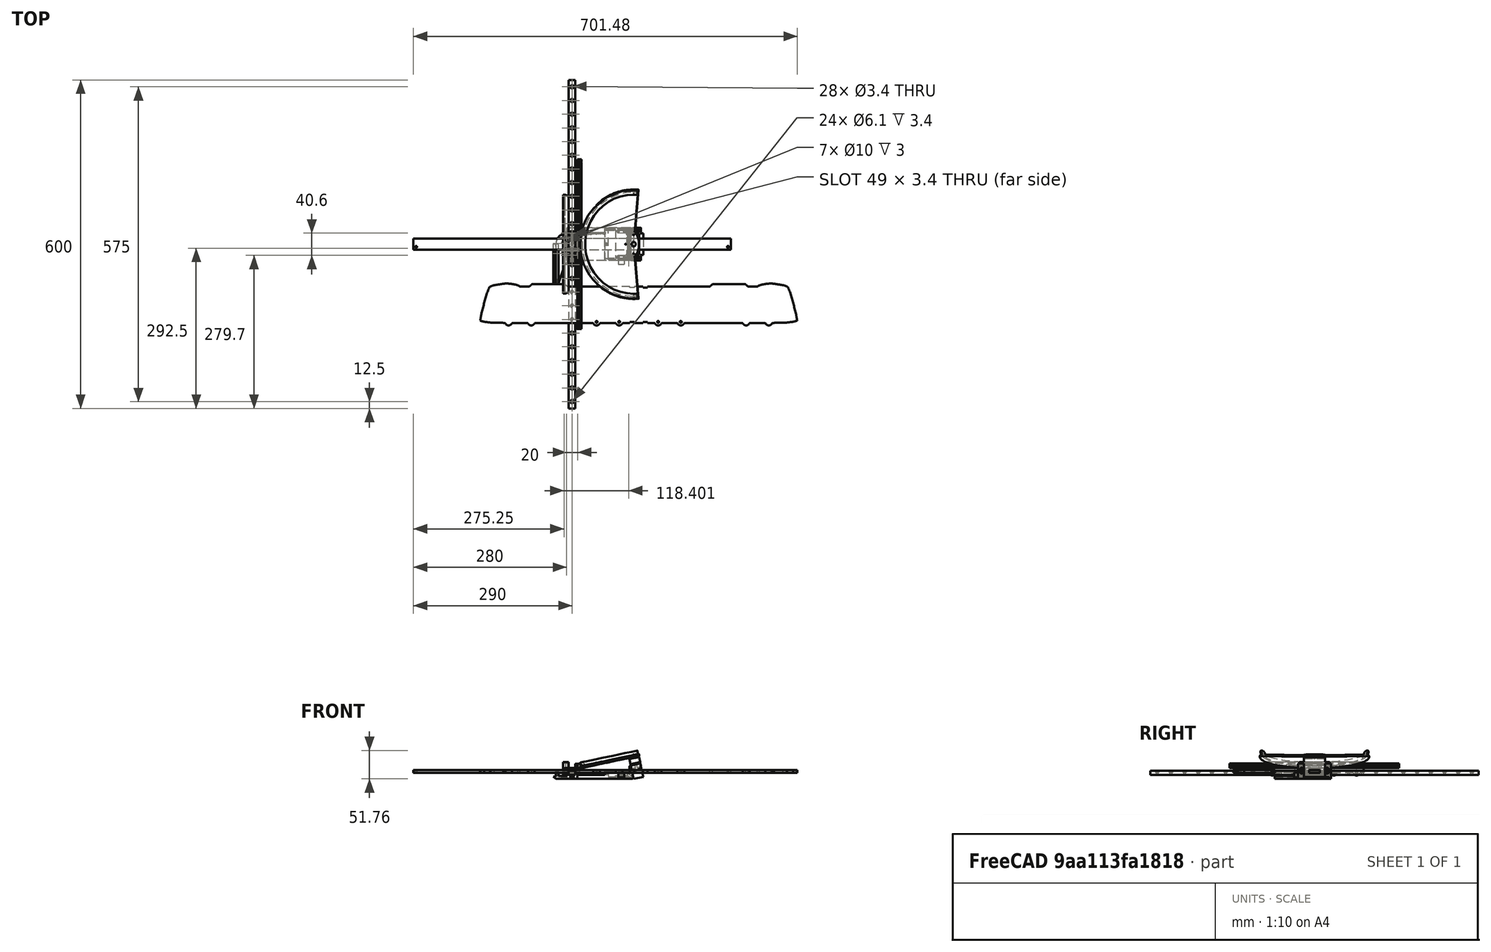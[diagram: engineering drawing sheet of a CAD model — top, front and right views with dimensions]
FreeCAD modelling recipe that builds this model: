
FCSTD DOCUMENT  (FreeCAD 1.0R39319 (Git))
Label: mechanism
License: All rights reserved
LicenseURL: https://en.wikipedia.org/wiki/All_rights_reserved
objects: Sketcher::SketchObject×61, PartDesign::Pad×27, PartDesign::SubShapeBinder×24, PartDesign::Pocket×22, App::Link×15, App::FeaturePython×15, PartDesign::Body×13, PartDesign::Hole×12, PartDesign::Mirrored×3, PartDesign::Fillet×3, PartDesign::LinearPattern×1, PartDesign::Revolution×1, PartDesign::SubtractivePipe×1, PartDesign::FeatureBase×1, Part::FeaturePython×1, Assembly::JointGroup×1, Assembly::AssemblyObject×1
note: 368 computed .brp shape members not serialized (recipe doc carries the construction recipe); baked Part::Feature solids carry a one-line shape summary decoded from their .brp

FEATURE [Sketcher::SketchObject] Sketch  label="Rail Cross-Section"
  ArcFitTolerance = 1e-06
  AttachmentSupport = -> [XZ_Plane]
  FullyConstrained = true
  MakeInternals = false
  MapMode = 5
  Placement = pos=(0,0,0) rot=(1,0,0;1.5708rad)
  sketch-geometry (11):
    g0: LineSegment StartX=-6 StartY=4 StartZ=0 EndX=-6 EndY=-3.35 EndZ=0
    g1: LineSegment StartX=-5.35 StartY=-4 StartZ=0 EndX=5.35 EndY=-4 EndZ=0
    g2: LineSegment StartX=6 StartY=-3.35 StartZ=0 EndX=6 EndY=4 EndZ=0
    g3: LineSegment StartX=6 StartY=4 StartZ=0 EndX=-6 EndY=4 EndZ=0
    g4: GeomPoint [constr] X=0 Y=0 Z=0
    g5: GeomPoint [constr] X=-6 Y=4 Z=0
    g6: GeomPoint [constr] X=6 Y=4 Z=0
    g7: ArcOfCircle CenterX=5.35 CenterY=-3.35 CenterZ=0 NormalX=0 NormalY=0 NormalZ=1 AngleXU=0 Radius=0.65 StartAngle=4.71239 EndAngle=6.28319
    g8: GeomPoint [constr] X=6 Y=-4 Z=0
    g9: ArcOfCircle CenterX=-5.35 CenterY=-3.35 CenterZ=0 NormalX=0 NormalY=0 NormalZ=1 AngleXU=0 Radius=0.65 StartAngle=3.14159 EndAngle=4.71239
    g10: GeomPoint [constr] X=-6 Y=-4 Z=0
  constraints (22):
    c: Vertical(g0)
    c: Vertical(g2)
    c: Horizontal(g1)
    c: Horizontal(g3)
    c: Symmetric(g8,g5,g4)
    c: Coincident(g4,g-1)
    c: DistanceX(g5,g6) = 12  'Wr'
    c: DistanceY(g8,g6) = 8  'Hr'
    c: PointOnObject(g8,g2)
    c: PointOnObject(g8,g1)
    c: Tangent(g2,g7) = -1.5708
    c: Tangent(g1,g7) = -1.5708
    c: PointOnObject(g10,g1)
    c: PointOnObject(g10,g0)
    c: Tangent(g1,g9) = -1.5708
    c: Tangent(g0,g9) = -1.5708
    c: Equal(g9,g7)
    c: Coincident(g2,g6)
    c: Coincident(g3,g2)
    c: Coincident(g0,g5)
    c: Coincident(g3,g0)
    c: Radius(g9) = 0.65  'radius'
FEATURE [PartDesign::Pad] Pad  label="Rail Extrusion"
  Direction = (0,-1,2e-16)
  Length = 600
  Length2 = 10
  Midplane = true
  Placement = pos=(0,0,0) rot=(1,0,0;1.5708rad)
  Profile = -> Sketch
  ReferenceAxis = -> Sketch [N_Axis]
  Refine = true
  Suppressed = false
  Type = 0
FEATURE [PartDesign::SubShapeBinder] Binder  label="SubShapeBinder"
  BindCopyOnChange = 0
  BindMode = 0
  ClaimChildren = false
  Context = -> Body001 [Binder.]
  Fuse = false
  MakeFace = true
  OffsetFill = false
  OffsetIntersection = false
  OffsetJoinType = 0
  OffsetOpenResult = false
  PartialLoad = false
  Refine = true
  Relative = true
  Support = -> [Body[Sketch.]]
  _Version = 2
FEATURE [Sketcher::SketchObject] Sketch001  label="Block Cross-Section"
  ArcFitTolerance = 1e-06
  AttachmentSupport = -> [Binder]
  ExternalGeometry = -> [Binder]
  FullyConstrained = true
  MakeInternals = false
  MapMode = 5
  Placement = pos=(0,0,0) rot=(0,0.707107,0.707107;3.14159rad)
  sketch-geometry (17):
    g0: LineSegment StartX=-13.5 StartY=8.5 StartZ=0 EndX=-13.5 EndY=-0.5 EndZ=0
    g1: LineSegment StartX=-13 StartY=-1 StartZ=0 EndX=-6 EndY=-1 EndZ=0
    g2: LineSegment StartX=13.5 StartY=-0.5 StartZ=0 EndX=13.5 EndY=8.5 EndZ=0
    g3: LineSegment StartX=13 StartY=9 StartZ=0 EndX=-13 EndY=9 EndZ=0
    g4: GeomPoint [constr] X=0 Y=4 Z=0
    g5: LineSegment StartX=-6 StartY=-1 StartZ=0 EndX=-6 EndY=4 EndZ=0
    g6: LineSegment StartX=-6 StartY=4 StartZ=0 EndX=6 EndY=4 EndZ=0
    g7: LineSegment StartX=6 StartY=4 StartZ=0 EndX=6 EndY=-1 EndZ=0
    g8: LineSegment StartX=6 StartY=-1 StartZ=0 EndX=13 EndY=-1 EndZ=0
    g9: ArcOfCircle CenterX=-13 CenterY=8.5 CenterZ=0 NormalX=0 NormalY=0 NormalZ=1 AngleXU=0 Radius=0.5 StartAngle=1.5708 EndAngle=3.14159
    g10: GeomPoint [constr] X=-13.5 Y=9 Z=0
    g11: ArcOfCircle CenterX=13 CenterY=8.5 CenterZ=0 NormalX=0 NormalY=0 NormalZ=1 AngleXU=0 Radius=0.5 StartAngle=-1.8e-15 EndAngle=1.5708
    g12: GeomPoint [constr] X=13.5 Y=9 Z=0
    g13: ArcOfCircle CenterX=13 CenterY=-0.5 CenterZ=0 NormalX=0 NormalY=0 NormalZ=1 AngleXU=0 Radius=0.5 StartAngle=4.71239 EndAngle=6.28319
    g14: GeomPoint [constr] X=13.5 Y=-1 Z=0
    g15: ArcOfCircle CenterX=-13 CenterY=-0.5 CenterZ=0 NormalX=0 NormalY=0 NormalZ=1 AngleXU=0 Radius=0.5 StartAngle=3.14159 EndAngle=4.71239
    g16: GeomPoint [constr] X=-13.5 Y=-1 Z=0
  constraints (41):
    c: Vertical(g0)
    c: Vertical(g2)
    c: Horizontal(g1)
    c: Horizontal(g3)
    c: Symmetric(g14,g10,g4)
    c: PointOnObject(g4,g-2)
    c: Vertical(g5)
    c: Coincident(g5,g6)
    c: Coincident(g6,g7)
    c: PointOnObject(g7,g8)
    c: Vertical(g7)
    c: Coincident(g1,g5)
    c: PointOnObject(g8,g7)
    c: Symmetric(g6,g5,g-2)
    c: PointOnObject(g1,g-3)
    c: PointOnObject(g5,g-4)
    c: DistanceY(g-5,g10) = 13  'Height'
    c: DistanceY(g-5,g16) = 3  'H1'
    c: Horizontal(g7,g1)
    c: Horizontal(g8)
    c: DistanceX(g10,g12) = 27  'W'
    c: PointOnObject(g10,g0)
    c: PointOnObject(g10,g3)
    c: Tangent(g0,g9) = -1.5708
    c: Tangent(g3,g9) = -1.5708
    c: PointOnObject(g12,g3)
    c: PointOnObject(g12,g2)
    c: Tangent(g3,g11) = -1.5708
    c: Tangent(g2,g11) = -1.5708
    c: PointOnObject(g14,g8)
    c: PointOnObject(g14,g2)
    c: Tangent(g8,g13) = -1.5708
    c: Tangent(g2,g13) = -1.5708
    c: PointOnObject(g16,g1)
    c: PointOnObject(g16,g0)
    c: Tangent(g1,g15) = -1.5708
    c: Tangent(g0,g15) = -1.5708
    c: Equal(g9,g15)
    c: Equal(g15,g11)
    c: Equal(g11,g13)
    c: Radius(g9) = 0.5
FEATURE [PartDesign::Pad] Pad001
  Direction = (0,1,-2e-16)
  Length = 32.4
  Length2 = 10
  Midplane = true
  Profile = -> Sketch001
  ReferenceAxis = -> Sketch001 [N_Axis]
  Refine = true
  Suppressed = false
  Type = 0
FEATURE [Sketcher::SketchObject] Sketch002
  ArcFitTolerance = 1e-06
  AttachmentSupport = -> [XZ_Plane001]
  ExternalGeometry = -> [Sketch001]
  FullyConstrained = true
  MakeInternals = false
  MapMode = 5
  Placement = pos=(0,0,0) rot=(1,0,0;1.5708rad)
  sketch-geometry (8):
    g0: LineSegment StartX=-13 StartY=8.5 StartZ=0 EndX=-13 EndY=-0.5 EndZ=0
    g1: LineSegment StartX=-13 StartY=-0.5 StartZ=0 EndX=-6 EndY=-0.5 EndZ=0
    g2: LineSegment StartX=-6 StartY=-0.5 StartZ=0 EndX=-6 EndY=4 EndZ=0
    g3: LineSegment StartX=-6 StartY=4 StartZ=0 EndX=6 EndY=4 EndZ=0
    g4: LineSegment StartX=6 StartY=4 StartZ=0 EndX=6 EndY=-0.5 EndZ=0
    g5: LineSegment StartX=6 StartY=-0.5 StartZ=0 EndX=13 EndY=-0.5 EndZ=0
    g6: LineSegment StartX=13 StartY=-0.5 StartZ=0 EndX=13 EndY=8.5 EndZ=0
    g7: LineSegment StartX=13 StartY=8.5 StartZ=0 EndX=-13 EndY=8.5 EndZ=0
  constraints (22):
    c: Vertical(g0)
    c: Coincident(g0,g1)
    c: PointOnObject(g1,g-7)
    c: Horizontal(g1)
    c: Coincident(g1,g2)
    c: Coincident(g2,g-7)
    c: Coincident(g2,g3)
    c: Coincident(g3,g-6)
    c: Coincident(g3,g4)
    c: Coincident(g4,g5)
    c: Horizontal(g5)
    c: Coincident(g5,g6)
    c: Vertical(g6)
    c: Coincident(g6,g7)
    c: Coincident(g7,g0)
    c: Horizontal(g7)
    c: Vertical(g-3,g0)
    c: Horizontal(g0,g-4)
    c: Horizontal(g-4,g0)
    c: Vertical(g4)
    c: Horizontal(g5,g-5)
    c: Vertical(g-3,g6)
FEATURE [PartDesign::Pad] Pad002  label="BlockExtent"
  BaseFeature = -> Pad001
  Direction = (0,-1,2e-16)
  Length = 45.4
  Length2 = 10
  Midplane = true
  Profile = -> Sketch002
  ReferenceAxis = -> Sketch002 [N_Axis]
  Refine = true
  Suppressed = false
  Type = 0
FEATURE [Sketcher::SketchObject] Sketch004
  ArcFitTolerance = 1e-06
  AttachmentSupport = -> [Pad001]
  FullyConstrained = false
  MakeInternals = false
  MapMode = 5
  Placement = pos=(0,2e-15,9) rot=(0,0,1;0rad)
  sketch-geometry (9):
    g0: Circle CenterX=-10 CenterY=10 CenterZ=0 NormalX=0 NormalY=0 NormalZ=1 AngleXU=0 Radius=2.53403
    g1: Circle CenterX=10 CenterY=10 CenterZ=0 NormalX=0 NormalY=0 NormalZ=1 AngleXU=0 Radius=2.44373
    g2: Circle CenterX=-10 CenterY=-10 CenterZ=0 NormalX=0 NormalY=0 NormalZ=1 AngleXU=0 Radius=2.20024
    g3: Circle CenterX=10 CenterY=-10 CenterZ=0 NormalX=0 NormalY=0 NormalZ=1 AngleXU=0 Radius=2.23133
    g4: LineSegment [constr] StartX=-10 StartY=10 StartZ=0 EndX=-10 EndY=-10 EndZ=0
    g5: LineSegment [constr] StartX=-10 StartY=-10 StartZ=0 EndX=10 EndY=-10 EndZ=0
    g6: LineSegment [constr] StartX=10 StartY=-10 StartZ=0 EndX=10 EndY=10 EndZ=0
    g7: LineSegment [constr] StartX=10 StartY=10 StartZ=0 EndX=-10 EndY=10 EndZ=0
    g8: GeomPoint [constr] X=0 Y=0 Z=0
  constraints (16):
    c: Coincident(g4,g5)
    c: Coincident(g5,g6)
    c: Coincident(g6,g7)
    c: Coincident(g7,g4)
    c: Vertical(g4)
    c: Vertical(g6)
    c: Horizontal(g5)
    c: Horizontal(g7)
    c: Symmetric(g6,g4,g8)
    c: Coincident(g8,g-1)
    c: DistanceX(g7,g7) = 20  'B'
    c: DistanceY(g6,g6) = 20  'C'
    c: Coincident(g0,g4)
    c: Coincident(g1,g6)
    c: Coincident(g5,g3)
    c: Coincident(g4,g2)
FEATURE [PartDesign::Hole] Hole
  BaseFeature = -> Pad002
  CustomThreadClearance = 0
  Depth = 3.5
  DepthType = 0
  Diameter = 2.5
  DrillForDepth = false
  DrillPoint = 1
  DrillPointAngle = 118
  HoleCutCountersinkAngle = 90
  HoleCutCustomValues = false
  HoleCutDepth = 0
  HoleCutDiameter = 6.1
  HoleCutType = 0
  ModelThread = false
  Profile = -> Sketch004
  Refine = true
  Suppressed = false
  Tapered = false
  TaperedAngle = 90
  ThreadClass = 0
  ThreadDepth = 3.5
  ThreadDepthType = 0
  ThreadDirection = 0
  ThreadFit = 0
  ThreadSize = 9
  ThreadType = 1
  Threaded = true
  UseCustomThreadClearance = false
FEATURE [PartDesign::Body] Body001  label="Block"
  AllowCompound = false
  Group = -> [Binder,Sketch001,Pad001,Sketch002,Pad002,Sketch004,Hole]
  Origin = -> Origin001
  Tip = -> Hole
FEATURE [Sketcher::SketchObject] Sketch005  label="RailHolePosition"
  ArcFitTolerance = 1e-06
  AttachmentSupport = -> [Pad]
  ExternalGeometry = -> [Pad]
  FullyConstrained = false
  MakeInternals = false
  MapMode = 5
  Placement = pos=(0,1.8e-15,4) rot=(0,0,1;3.14159rad)
  sketch-geometry (1):
    g0: Circle CenterX=0 CenterY=-287.5 CenterZ=0 NormalX=0 NormalY=0 NormalZ=1 AngleXU=0 Radius=2.44176
  constraints (2):
    c: PointOnObject(g0,g-2)
    c: DistanceY(g-3,g0) = 12.5  'E'
FEATURE [PartDesign::Hole] Hole001
  BaseFeature = -> Pad
  CustomThreadClearance = 0
  Depth = 1212.35
  DepthType = 1
  Diameter = 3.4
  DrillForDepth = false
  DrillPoint = 1
  DrillPointAngle = 118
  HoleCutCountersinkAngle = 90
  HoleCutCustomValues = false
  HoleCutDepth = 3.4
  HoleCutDiameter = 6.1
  HoleCutType = 1
  ModelThread = false
  Placement = pos=(0,0,0) rot=(1,0,0;1.5708rad)
  Profile = -> Sketch005
  Refine = true
  Suppressed = false
  Tapered = false
  TaperedAngle = 90
  ThreadClass = 0
  ThreadDepth = 1212.35
  ThreadDepthType = 0
  ThreadDirection = 0
  ThreadFit = 0
  ThreadSize = 9
  ThreadType = 1
  Threaded = false
  UseCustomThreadClearance = false
FEATURE [PartDesign::LinearPattern] LinearPattern
  BaseFeature = -> Hole001
  Direction = -> Y_Axis
  Length = 575
  Mode = 1
  Occurrences = 24
  Offset = 25
  Originals = -> [Hole001]
  Placement = pos=(0,0,0) rot=(1,0,0;1.5708rad)
  Refine = true
  Reversed = true
  Suppressed = false
  TransformMode = 0
  expr: Occurrences = <<Rail Extrusion>>.Length / 25
FEATURE [PartDesign::Body] Body  label="Rail"
  AllowCompound = false
  Group = -> [Sketch,Pad,Sketch005,Hole001,LinearPattern]
  Origin = -> Origin
  Tip = -> LinearPattern
FEATURE [PartDesign::SubShapeBinder] Binder001
  BindCopyOnChange = 0
  BindMode = 0
  ClaimChildren = false
  Context = -> Body002 [Binder001.]
  Fuse = false
  MakeFace = true
  OffsetFill = false
  OffsetIntersection = false
  OffsetJoinType = 0
  OffsetOpenResult = false
  PartialLoad = false
  Refine = true
  Relative = true
  Support = -> [Body[Sketch.]]
  _Version = 2
FEATURE [PartDesign::SubShapeBinder] Binder002
  BindCopyOnChange = 0
  BindMode = 0
  ClaimChildren = false
  Context = -> Body002 [Binder002.]
  Fuse = false
  MakeFace = true
  OffsetFill = false
  OffsetIntersection = false
  OffsetJoinType = 0
  OffsetOpenResult = false
  PartialLoad = false
  Refine = true
  Relative = true
  Support = -> [Body001[Sketch001.]]
  _Version = 2
FEATURE [Sketcher::SketchObject] Sketch006  label="FootProfile"
  ArcFitTolerance = 1e-06
  AttachmentSupport = -> [XZ_Plane002]
  ExternalGeometry = -> [Binder001,Binder002]
  FullyConstrained = true
  MakeInternals = false
  MapMode = 5
  Placement = pos=(0,0,0) rot=(1,0,0;1.5708rad)
  sketch-geometry (12):
    g0: LineSegment StartX=-9.7 StartY=-4 StartZ=0 EndX=-9.7 EndY=-11 EndZ=0
    g1: LineSegment StartX=-6.1 StartY=-4 StartZ=0 EndX=-6.1 EndY=-2.6 EndZ=0
    g2: LineSegment StartX=-6.7 StartY=-2 StartZ=0 EndX=-7.7 EndY=-2 EndZ=0
    g3: LineSegment StartX=-6.1 StartY=-4 StartZ=0 EndX=0 EndY=-4 EndZ=0
    g4: LineSegment StartX=0 StartY=-4 StartZ=0 EndX=0 EndY=-11 EndZ=0
    g5: LineSegment StartX=0 StartY=-11 StartZ=0 EndX=-9.7 EndY=-11 EndZ=0
    g6: ArcOfCircle [constr] CenterX=-6.7 CenterY=-2.6 CenterZ=0 NormalX=0 NormalY=0 NormalZ=1 AngleXU=0 Radius=0.6 StartAngle=1e-16 EndAngle=1.5708
    g7: GeomPoint [constr] X=-6.1 Y=-2 Z=0
    g8: LineSegment StartX=-6.1 StartY=-2.6 StartZ=0 EndX=-6.7 EndY=-2 EndZ=0
    g9: ArcOfCircle [constr] CenterX=-7.7 CenterY=-4 CenterZ=0 NormalX=0 NormalY=0 NormalZ=1 AngleXU=0 Radius=2 StartAngle=1.5708 EndAngle=3.14159
    g10: GeomPoint [constr] X=-9.7 Y=-2 Z=0
    g11: LineSegment StartX=-7.7 StartY=-2 StartZ=0 EndX=-9.7 EndY=-4 EndZ=0
  constraints (30):
    c: Vertical(g0)
    c: Vertical(g1)
    c: Horizontal(g2)
    c: Distance(g-3,g1) = 0.1
    c: Distance(g-4,g2) = 1
    c: Coincident(g3,g1)
    c: PointOnObject(g3,g-2)
    c: Horizontal(g3)
    c: Coincident(g4,g3)
    c: Vertical(g4)
    c: Coincident(g5,g4)
    c: Coincident(g5,g0)
    c: Horizontal(g5)
    c: Distance(g4,g4) = 7  'BaseThickness'
    c: PointOnObject(g1,g-5)
    c: PointOnObject(g7,g2)
    c: PointOnObject(g7,g1)
    c: Tangent(g2,g6) = -1.5708
    c: Tangent(g1,g6) = -1.5708
    c: Coincident(g8,g2)
    c: Coincident(g8,g1)
    c: PointOnObject(g10,g2)
    c: PointOnObject(g10,g0)
    c: Tangent(g2,g9) = -1.5708
    c: Tangent(g0,g9) = -1.5708
    c: Coincident(g11,g2)
    c: Coincident(g11,g0)
    c: Distance(g1,g7) = 0.6
    c: Distance(g2,g2) = 1
    c: Horizontal(g9,g1)
FEATURE [PartDesign::Pad] Pad003
  Direction = (0,-1,2e-16)
  Length = 20
  Length2 = 5
  Midplane = true
  Placement = pos=(0,0,0) rot=(1,0,0;1.5708rad)
  Profile = -> Sketch006
  ReferenceAxis = -> Sketch006 [N_Axis]
  Refine = true
  Suppressed = false
  Type = 4
FEATURE [PartDesign::Mirrored] Mirrored
  BaseFeature = -> Pad003
  MirrorPlane = -> Sketch006 [V_Axis]
  Originals = -> [Pad003]
  Placement = pos=(0,0,0) rot=(1,0,0;1.5708rad)
  Refine = true
  Suppressed = false
  TransformMode = 0
FEATURE [Sketcher::SketchObject] Sketch007
  ArcFitTolerance = 1e-06
  AttachmentSupport = -> [Mirrored]
  FullyConstrained = false
  MakeInternals = false
  MapMode = 5
  Placement = pos=(0,-1.8e-15,-4) rot=(0,0,1;3.14159rad)
  sketch-geometry (1):
    g0: Circle CenterX=0 CenterY=0 CenterZ=0 NormalX=0 NormalY=0 NormalZ=1 AngleXU=0 Radius=1.1986
  constraints (1):
    c: Coincident(g0,g-1)
FEATURE [PartDesign::Hole] Hole002  label="FootHole"
  BaseFeature = -> Mirrored
  CustomThreadClearance = 0
  Depth = 109.851
  DepthType = 1
  Diameter = 4.4
  DrillForDepth = false
  DrillPoint = 1
  DrillPointAngle = 118
  HoleCutCountersinkAngle = 90
  HoleCutCustomValues = false
  HoleCutDepth = 0
  HoleCutDiameter = 6.1
  HoleCutType = 0
  ModelThread = false
  Placement = pos=(0,0,0) rot=(1,0,0;1.5708rad)
  Profile = -> Sketch007
  Refine = true
  Suppressed = false
  Tapered = false
  TaperedAngle = 90
  ThreadClass = 0
  ThreadDepth = 109.851
  ThreadDepthType = 0
  ThreadDirection = 0
  ThreadFit = 0
  ThreadSize = 0
  ThreadType = 0
  Threaded = false
  UseCustomThreadClearance = false
FEATURE [PartDesign::SubShapeBinder] Binder003
  BindCopyOnChange = 0
  BindMode = 0
  ClaimChildren = false
  Context = -> Body003 [Binder003.]
  Fuse = false
  MakeFace = true
  OffsetFill = false
  OffsetIntersection = false
  OffsetJoinType = 0
  OffsetOpenResult = false
  PartialLoad = false
  Refine = true
  Relative = true
  Support = -> [Body002[Sketch006.]]
  _Version = 2
FEATURE [PartDesign::SubShapeBinder] Binder004
  BindCopyOnChange = 0
  BindMode = 0
  ClaimChildren = false
  Context = -> Body003 [Binder004.]
  Fuse = false
  MakeFace = true
  OffsetFill = false
  OffsetIntersection = false
  OffsetJoinType = 0
  OffsetOpenResult = false
  PartialLoad = false
  Refine = true
  Relative = true
  Support = -> [Body001[Sketch001.]]
  _Version = 2
FEATURE [Sketcher::SketchObject] Sketch008
  ArcFitTolerance = 1e-06
  AttachmentSupport = -> [XZ_Plane003]
  ExternalGeometry = -> [Binder004,Binder003]
  FullyConstrained = true
  MakeInternals = false
  MapMode = 5
  Placement = pos=(0,0,0) rot=(1,0,0;1.5708rad)
  sketch-geometry (7):
    g0: LineSegment StartX=-6 StartY=9 StartZ=0 EndX=-13.5 EndY=9 EndZ=0
    g1: LineSegment StartX=-13.5 StartY=9 StartZ=0 EndX=-13.5 EndY=-6 EndZ=0
    g2: LineSegment StartX=-13.5 StartY=-6 StartZ=0 EndX=-16.5 EndY=-6 EndZ=0
    g3: LineSegment StartX=-16.5 StartY=-6 StartZ=0 EndX=-16.5 EndY=19.5 EndZ=0
    g4: LineSegment StartX=-16.5 StartY=19.5 StartZ=0 EndX=-6 EndY=19.5 EndZ=0
    g5: LineSegment StartX=-6 StartY=19.5 StartZ=0 EndX=-6 EndY=9 EndZ=0
    g6: LineSegment [constr] StartX=-11.25 StartY=19.5 StartZ=0 EndX=-11.25 EndY=7 EndZ=0
  constraints (21):
    c: PointOnObject(g0,g-4)
    c: Horizontal(g0)
    c: Coincident(g0,g1)
    c: PointOnObject(g1,g-6)
    c: Vertical(g1)
    c: Coincident(g1,g2)
    c: Horizontal(g2)
    c: Coincident(g2,g3)
    c: Vertical(g3)
    c: Coincident(g3,g4)
    c: Horizontal(g4)
    c: Coincident(g4,g5)
    c: Coincident(g5,g0)
    c: Vertical(g5)
    c: Distance(g2,g-5) = 5
    c: Distance(g2,g2) = 3
    c: PointOnObject(g0,g-7)
    c: Symmetric(g4,g4,g6)
    c: Vertical(g6)
    c: Distance(g6,g0) = 2
    c: DistanceY(g6,g6) = 12.5
FEATURE [PartDesign::Pad] Pad004
  Direction = (0,-1,2e-16)
  Length = 180
  Length2 = 10
  Midplane = true
  Placement = pos=(0,0,0) rot=(1,0,0;1.5708rad)
  Profile = -> Sketch008
  ReferenceAxis = -> Sketch008 [N_Axis]
  Refine = true
  Suppressed = false
  Type = 0
FEATURE [PartDesign::SubShapeBinder] Binder005
  BindCopyOnChange = 0
  BindMode = 0
  ClaimChildren = false
  Context = -> Body003 [Binder005.]
  Fuse = false
  MakeFace = true
  OffsetFill = false
  OffsetIntersection = false
  OffsetJoinType = 0
  OffsetOpenResult = false
  PartialLoad = false
  Refine = true
  Relative = true
  Support = -> [Body001[Pad002.Face14,Pad002.Face19]]
  _Version = 2
FEATURE [PartDesign::SubShapeBinder] Binder006
  BindCopyOnChange = 0
  BindMode = 0
  ClaimChildren = false
  Context = -> Body003 [Binder006.]
  Fuse = false
  MakeFace = true
  OffsetFill = false
  OffsetIntersection = false
  OffsetJoinType = 0
  OffsetOpenResult = false
  PartialLoad = false
  Refine = true
  Relative = true
  Support = -> [Body001[Sketch004.]]
  _Version = 2
FEATURE [Sketcher::SketchObject] Sketch010
  ArcFitTolerance = 1e-06
  AttachmentSupport = -> [Pad004]
  ExternalGeometry = -> [Binder006]
  FullyConstrained = true
  MakeInternals = false
  MapMode = 5
  Placement = pos=(0,8.6e-15,19.5) rot=(0,0,1;3.14159rad)
  sketch-geometry (2):
    g0: Circle CenterX=10 CenterY=-10 CenterZ=0 NormalX=0 NormalY=0 NormalZ=1 AngleXU=0 Radius=2.53403
    g1: Circle CenterX=10 CenterY=10 CenterZ=0 NormalX=0 NormalY=0 NormalZ=1 AngleXU=0 Radius=2.20024
  constraints (4):
    c: Coincident(g0,g-3)
    c: Equal(g0,g-3)
    c: Coincident(g1,g-4)
    c: Equal(g1,g-4)
FEATURE [PartDesign::SubShapeBinder] Binder008
  BindCopyOnChange = 0
  BindMode = 0
  ClaimChildren = false
  Context = -> Body004 [Binder008.]
  Fuse = false
  MakeFace = true
  OffsetFill = false
  OffsetIntersection = false
  OffsetJoinType = 0
  OffsetOpenResult = false
  PartialLoad = false
  Refine = true
  Relative = true
  Support = -> [Body001[Sketch001.]]
  _Version = 2
FEATURE [Sketcher::SketchObject] Sketch012  label="RackProfile"
  ArcFitTolerance = 1e-06
  AttachmentSupport = -> [XZ_Plane004]
  ExternalGeometry = -> [Binder008]
  FullyConstrained = true
  MakeInternals = false
  MapMode = 5
  Placement = pos=(0,0,0) rot=(1,0,0;1.5708rad)
  sketch-geometry (6):
    g0: LineSegment StartX=13.5 StartY=9 StartZ=0 EndX=17 EndY=12.5 EndZ=0
    g1: ArcOfCircle CenterX=17.5 CenterY=13 CenterZ=0 NormalX=0 NormalY=0 NormalZ=1 AngleXU=0 Radius=0.707107 StartAngle=2.35619 EndAngle=3.92699
    g2: LineSegment StartX=17 StartY=13.5 StartZ=0 EndX=13.5 EndY=17 EndZ=0
    g3: ArcOfCircle CenterX=13.5 CenterY=13 CenterZ=0 NormalX=0 NormalY=0 NormalZ=1 AngleXU=0 Radius=4 StartAngle=1.5708 EndAngle=3.14159
    g4: LineSegment StartX=9.5 StartY=13 StartZ=0 EndX=9.5 EndY=9 EndZ=0
    g5: LineSegment StartX=9.5 StartY=9 StartZ=0 EndX=13.5 EndY=9 EndZ=0
  constraints (18):
    c: Perpendicular(g0,g1) = 4.71239
    c: Coincident(g1,g2)
    c: Coincident(g3,g2)
    c: PointOnObject(g1,g2)
    c: Equal(g2,g0)
    c: PointOnObject(g0,g-4)
    c: Vertical(g2,g0)
    c: Horizontal(g-3,g0)
    c: Distance(g1,g0) = 1
    c: DistanceY(g0,g2) = 8
    c: Symmetric(g2,g0,g3)
    c: Horizontal(g3,g3)
    c: Coincident(g3,g4)
    c: PointOnObject(g4,g-3)
    c: Vertical(g4)
    c: Coincident(g4,g5)
    c: Coincident(g5,g0)
    c: Angle(g5,g0) = 0.785398
FEATURE [PartDesign::Pad] Pad005  label="RackExtrusion"
  Direction = (0,-1,2e-16)
  Length = 310
  Length2 = 10
  Midplane = true
  Placement = pos=(0,0,0) rot=(1,0,0;1.5708rad)
  Profile = -> Sketch012
  ReferenceAxis = -> Sketch012 [N_Axis]
  Refine = true
  Suppressed = false
  Type = 0
FEATURE [PartDesign::SubShapeBinder] Binder009
  BindCopyOnChange = 0
  BindMode = 0
  ClaimChildren = false
  Context = -> Body004 [Binder009.]
  Fuse = false
  MakeFace = true
  OffsetFill = false
  OffsetIntersection = false
  OffsetJoinType = 0
  OffsetOpenResult = false
  PartialLoad = false
  Refine = true
  Relative = true
  Support = -> [Body001[Sketch004.]]
  _Version = 2
FEATURE [Sketcher::SketchObject] Sketch015
  ArcFitTolerance = 1e-06
  AttachmentSupport = -> [XZ_Plane004]
  ExternalGeometry = -> [Pad005,Binder008]
  FullyConstrained = true
  MakeInternals = false
  MapMode = 5
  Placement = pos=(0,0,0) rot=(1,0,0;1.5708rad)
  sketch-geometry (4):
    g0: LineSegment StartX=6 StartY=16.5 StartZ=0 EndX=6 EndY=9 EndZ=0
    g1: LineSegment StartX=6 StartY=9 StartZ=0 EndX=13.5 EndY=9 EndZ=0
    g2: LineSegment StartX=13.5 StartY=9 StartZ=0 EndX=13.5 EndY=16.5 EndZ=0
    g3: LineSegment StartX=13.5 StartY=16.5 StartZ=0 EndX=6 EndY=16.5 EndZ=0
  constraints (11):
    c: Coincident(g0,g1)
    c: Coincident(g1,g2)
    c: Coincident(g2,g3)
    c: Coincident(g3,g0)
    c: Vertical(g0)
    c: Vertical(g2)
    c: Horizontal(g1)
    c: Horizontal(g3)
    c: Coincident(g1,g-3)
    c: Vertical(g0,g-4)
    c: Distance(g0,g0) = 7.5
FEATURE [PartDesign::Pad] Pad006
  BaseFeature = -> Pad005
  Direction = (0,-1,2e-16)
  Length = 45.4
  Length2 = 10
  Midplane = true
  Placement = pos=(0,0,0) rot=(1,0,0;1.5708rad)
  Profile = -> Sketch015
  ReferenceAxis = -> Sketch015 [N_Axis]
  Refine = true
  Suppressed = false
  Type = 0
  expr: Length = <<BlockExtent>>.Length
FEATURE [Sketcher::SketchObject] Sketch016
  ArcFitTolerance = 1e-06
  AttachmentSupport = -> [Pad006]
  ExternalGeometry = -> [Binder009]
  FullyConstrained = true
  MakeInternals = false
  MapMode = 5
  Placement = pos=(0,7.3e-15,16.5) rot=(0,0,1;3.14159rad)
  sketch-geometry (2):
    g0: Circle CenterX=-10 CenterY=10 CenterZ=0 NormalX=0 NormalY=0 NormalZ=1 AngleXU=0 Radius=2.23133
    g1: Circle CenterX=-10 CenterY=-10 CenterZ=0 NormalX=0 NormalY=0 NormalZ=1 AngleXU=0 Radius=2.44373
  constraints (4):
    c: Coincident(g0,g-3)
    c: Equal(g0,g-3)
    c: Coincident(g1,g-4)
    c: Equal(g1,g-4)
FEATURE [PartDesign::Hole] Hole004
  BaseFeature = -> Pad006
  CustomThreadClearance = 0
  Depth = 25
  DepthType = 0
  Diameter = 3.4
  DrillForDepth = false
  DrillPoint = 1
  DrillPointAngle = 118
  HoleCutCountersinkAngle = 90
  HoleCutCustomValues = false
  HoleCutDepth = 2
  HoleCutDiameter = 6.1
  HoleCutType = 1
  ModelThread = false
  Placement = pos=(0,0,0) rot=(1,0,0;1.5708rad)
  Profile = -> Sketch016
  Refine = true
  Suppressed = false
  Tapered = false
  TaperedAngle = 90
  ThreadClass = 0
  ThreadDepth = 25
  ThreadDepthType = 0
  ThreadDirection = 0
  ThreadFit = 0
  ThreadSize = 9
  ThreadType = 1
  Threaded = false
  UseCustomThreadClearance = false
FEATURE [Sketcher::SketchObject] Sketch017
  ArcFitTolerance = 1e-06
  AttachmentSupport = -> [Hole004]
  ExternalGeometry = -> [Hole004]
  FullyConstrained = true
  MakeInternals = false
  MapMode = 5
  Placement = pos=(0,7.3e-15,16.5) rot=(0,0,1;3.14159rad)
  sketch-geometry (2):
    g0: Circle CenterX=-10 CenterY=10 CenterZ=0 NormalX=0 NormalY=0 NormalZ=1 AngleXU=0 Radius=3.05
    g1: Circle CenterX=-10 CenterY=-10 CenterZ=0 NormalX=0 NormalY=0 NormalZ=1 AngleXU=0 Radius=3.05
  constraints (4):
    c: Coincident(g0,g-3)
    c: Equal(g0,g-3)
    c: Coincident(g1,g-4)
    c: Equal(g1,g-4)
FEATURE [PartDesign::Pocket] Pocket002
  BaseFeature = -> Hole004
  Direction = (0,0,-1)
  Length = 5
  Length2 = 5
  Placement = pos=(0,0,0) rot=(1,0,0;1.5708rad)
  Profile = -> Sketch017
  ReferenceAxis = -> Sketch017 [N_Axis]
  Refine = true
  Reversed = true
  Suppressed = false
  Type = 1
FEATURE [Sketcher::SketchObject] Sketch018  label="RackStringEnds"
  ArcFitTolerance = 1e-06
  AttachmentSupport = -> [Pocket002]
  ExternalGeometry = -> [Pocket002]
  FullyConstrained = true
  MakeInternals = false
  MapMode = 5
  Placement = pos=(9.5,0,0) rot=(0.707107,0,-0.707107;3.14159rad)
  sketch-geometry (3):
    g0: Circle CenterX=-13 CenterY=150 CenterZ=0 NormalX=0 NormalY=0 NormalZ=1 AngleXU=0 Radius=0.75
    g1: Circle CenterX=-13 CenterY=-150 CenterZ=0 NormalX=0 NormalY=0 NormalZ=1 AngleXU=0 Radius=0.75
    g2: GeomPoint [constr] X=-13 Y=-155 Z=0
  constraints (6):
    c: Symmetric(g1,g0,g-1)
    c: Equal(g0,g1)
    c: Symmetric(g-4,g-3,g2)
    c: Vertical(g2,g1)
    c: Diameter(g1) = 1.5  'stringHoleDiameter'
    c: DistanceY(g1,g0) = 300  'Length'
FEATURE [PartDesign::Pocket] Pocket003
  BaseFeature = -> Pocket002
  Direction = (1,0,2e-16)
  Length = 5
  Length2 = 5
  Placement = pos=(0,0,0) rot=(1,0,0;1.5708rad)
  Profile = -> Sketch018
  ReferenceAxis = -> Sketch018 [N_Axis]
  Refine = true
  Suppressed = false
  Type = 1
FEATURE [PartDesign::SubShapeBinder] Binder010
  BindCopyOnChange = 0
  BindMode = 0
  ClaimChildren = false
  Context = -> Body005 [Binder010.]
  Fuse = false
  MakeFace = true
  OffsetFill = false
  OffsetIntersection = false
  OffsetJoinType = 0
  OffsetOpenResult = false
  PartialLoad = false
  Refine = true
  Relative = true
  Support = -> [Body004[Sketch012.]]
  _Version = 2
FEATURE [PartDesign::SubShapeBinder] Binder011
  BindCopyOnChange = 0
  BindMode = 0
  ClaimChildren = false
  Context = -> Body005 [Binder011.]
  Fuse = false
  MakeFace = true
  OffsetFill = false
  OffsetIntersection = false
  OffsetJoinType = 0
  OffsetOpenResult = false
  PartialLoad = false
  Refine = true
  Relative = true
  Support = -> [Body002[Sketch006.]]
  _Version = 2
FEATURE [Sketcher::SketchObject] Sketch019  label="PinionCrossSection"
  ArcFitTolerance = 1e-06
  AttachmentSupport = -> [XZ_Plane005]
  ExternalGeometry = -> [Binder010,Binder011]
  FullyConstrained = true
  MakeInternals = false
  MapMode = 5
  Placement = pos=(0,0,0) rot=(1,0,0;1.5708rad)
  expr: Constraints[46] = <<RackStringEnds>>.Constraints.Length / pi
  sketch-geometry (27):
    g0: LineSegment StartX=14.9142 StartY=17 StartZ=0 EndX=18.9142 EndY=13 EndZ=0
    g1: LineSegment StartX=18.9142 StartY=13 StartZ=0 EndX=15.2909 EndY=9.37671 EndZ=0
    g2: LineSegment StartX=15.7474 StartY=8.53387 StartZ=0 EndX=113.128 EndY=29.0174 EndZ=0
    g3: LineSegment StartX=113.128 StartY=29.0174 StartZ=0 EndX=112.51 EndY=31.9532 EndZ=0
    g4: LineSegment StartX=112.51 StartY=31.9532 StartZ=0 EndX=23.9043 EndY=13.3153 EndZ=0
    g5: ArcOfCircle CenterX=16.794 CenterY=11.8197 CenterZ=0 NormalX=0 NormalY=0 NormalZ=1 AngleXU=0 Radius=7.26587 StartAngle=0.207323 EndAngle=1.64585
    g6: LineSegment StartX=14.9849 StartY=18.4849 StartZ=0 EndX=14.9142 EndY=18.4142 EndZ=0
    g7: LineSegment [constr] StartX=13.5 StartY=17 StartZ=0 EndX=17.5 EndY=13 EndZ=0
    g8: LineSegment [constr] StartX=17.5 StartY=13 StartZ=0 EndX=13.5 EndY=9 EndZ=0
    g9: ArcOfCircle [constr] CenterX=13.5 CenterY=9 CenterZ=0 NormalX=0 NormalY=0 NormalZ=-1 AngleXU=2.35619 Radius=1 StartAngle=1.5708 EndAngle=4.71239
    g10: LineSegment [constr] StartX=16.0858 StartY=13 StartZ=0 EndX=12.7929 EndY=9.70711 EndZ=0
    g11: LineSegment [constr] StartX=12.7929 StartY=16.2929 StartZ=0 EndX=16.0858 EndY=13 EndZ=0
    g12: ArcOfCircle [constr] CenterX=13.5 CenterY=17 CenterZ=0 NormalX=0 NormalY=0 NormalZ=-1 AngleXU=-2.35619 Radius=1 StartAngle=1.5708 EndAngle=4.71239
    g13: LineSegment [constr] StartX=14.2071 StartY=17.7071 StartZ=0 EndX=18.2071 EndY=13.7071 EndZ=0
    g14: ArcOfCircle [constr] CenterX=17.5 CenterY=13 CenterZ=0 NormalX=0 NormalY=0 NormalZ=-1 AngleXU=0.785398 Radius=1 StartAngle=1.5708 EndAngle=3.14159
    g15: LineSegment [constr] StartX=18.2071 StartY=12.2929 StartZ=0 EndX=14.2071 EndY=8.29289 EndZ=0
    g16: ArcOfCircle CenterX=16.3991 CenterY=17.0707 CenterZ=0 NormalX=0 NormalY=0 NormalZ=1 AngleXU=0 Radius=2 StartAngle=1.64585 EndAngle=2.35619
    g17: ArcOfCircle CenterX=15.6213 CenterY=17.7071 CenterZ=0 NormalX=0 NormalY=0 NormalZ=1 AngleXU=0 Radius=1 StartAngle=2.35619 EndAngle=3.92699
    g18: GeomPoint [constr] X=14.2071 Y=17.7071 Z=0
    g19: ArcOfCircle CenterX=15.6445 CenterY=9.02316 CenterZ=0 NormalX=0 NormalY=0 NormalZ=1 AngleXU=0 Radius=0.5 StartAngle=2.35619 EndAngle=4.91971
    g20: GeomPoint [constr] X=14.102 Y=8.18776 Z=0
    g21: LineSegment [constr] StartX=104.732 StartY=25.2077 StartZ=0 EndX=122.347 EndY=28.9128 EndZ=0
    g22: LineSegment [constr] StartX=122.347 StartY=28.9128 StartZ=0 EndX=129.963 EndY=-7.29486 EndZ=0
    g23: LineSegment [constr] StartX=129.963 StartY=-7.29486 StartZ=0 EndX=112.348 EndY=-11 EndZ=0
    g24: LineSegment [constr] StartX=112.348 StartY=-11 StartZ=0 EndX=104.732 EndY=25.2077 EndZ=0
    g25: GeomPoint [constr] X=113.539 Y=27.0602 Z=0
    g26: LineSegment [constr] StartX=13.5 StartY=9 StartZ=0 EndX=15.2909 EndY=9.37671 EndZ=0
  constraints (66):
    c: Coincident(g0,g1)
    c: Coincident(g2,g3)
    c: Coincident(g3,g4)
    c: Perpendicular(g4,g5) = 4.71239
    c: Parallel(g2,g4)
    c: Perpendicular(g2,g3)
    c: Coincident(g-3,g7)
    c: Coincident(g7,g8)
    c: Coincident(g8,g-4)
    c: PointOnObject(g-4,g8)
    c: PointOnObject(g-3,g7)
    c: Tangent(g9,g10) = -1.5708
    c: Tangent(g9,g15) = 1.5708
    c: Coincident(g10,g11)
    c: Tangent(g11,g12) = -1.5708
    c: Tangent(g12,g13) = 1.5708
    c: Tangent(g13,g14) = 1.5708
    c: Tangent(g14,g15) = 1.5708
    c: Parallel(g15,g8)
    c: Coincident(g9,g8)
    c: Parallel(g10,g8)
    c: Parallel(g11,g7)
    c: Coincident(g12,g7)
    c: Parallel(g13,g7)
    c: Coincident(g14,g7)
    c: Distance(g14,g14) = 1
    c: PointOnObject(g18,g13)
    c: PointOnObject(g0,g13)
    c: PointOnObject(g20,g15)
    c: PointOnObject(g0,g15)
    c: PointOnObject(g12,g6)
    c: Perpendicular(g6,g0)
    c: Distance(g3,g3) = 3  'thickness'
    c: Tangent(g5,g16) = -1.5708
    c: Tangent(g6,g16) = -1.5708
    c: PointOnObject(g18,g0)
    c: PointOnObject(g18,g6)
    c: Tangent(g0,g17) = -1.5708
    c: Tangent(g6,g17) = -1.5708
    c: PointOnObject(g20,g1)
    c: PointOnObject(g20,g2)
    c: Tangent(g1,g19) = -1.5708
    c: Tangent(g2,g19) = -1.5708
    c: Radius(g19) = 0.5
    c: Radius(g17) = 1
    c: Radius(g16) = 2
    c: Distance(g0,g3) = 95.493
    c: Coincident(g21,g22)
    c: Coincident(g22,g23)
    c: Coincident(g23,g24)
    c: Coincident(g24,g21)
    c: Perpendicular(g21,g24)
    c: Perpendicular(g22,g23)
    c: Perpendicular(g22,g21)
    c: Distance(g22,g22) = 37  'ServoBodyHeight'
    c: Distance(g23,g23) = 18  'ServoBodyWidth'
    c: Symmetric(g21,g21,g25)
    c: Parallel(g2,g21)
    c: PointOnObject(g25,g3)
    c: Distance(g0,g4) = 5
    c: Distance(g6,g6) = 0.1
    c: Horizontal(g-5,g23)
    c: Distance(g3,g25) = 5  'ServoShaftLength'
    c: Coincident(g26,g8)
    c: Parallel(g26,g2)
    c: Coincident(g26,g1)
FEATURE [PartDesign::Revolution] Revolution
  Angle = 190
  Angle2 = 60
  Axis = (-0.205841,2e-16,0.978585)
  Base = (113.128,6.4e-15,29.0174)
  Midplane = true
  Placement = pos=(0,0,0) rot=(1,0,0;1.5708rad)
  Profile = -> Sketch019
  ReferenceAxis = -> Sketch019 [Edge5]
  Refine = true
  Reversed = true
  Suppressed = false
  Type = 0
FEATURE [Sketcher::SketchObject] Sketch020
  ArcFitTolerance = 1e-06
  AttachmentSupport = -> [XZ_Plane005]
  ExternalGeometry = -> [Revolution]
  FullyConstrained = true
  MakeInternals = false
  MapMode = 5
  Placement = pos=(0,0,0) rot=(1,0,0;1.5708rad)
  expr: Constraints[0] = <<RackStringEnds>>.Constraints.stringHoleDiameter
  sketch-geometry (2):
    g0: Circle CenterX=112.356 CenterY=32.6871 CenterZ=0 NormalX=0 NormalY=0 NormalZ=1 AngleXU=0 Radius=0.75
    g1: GeomPoint [constr] X=112.51 Y=31.9532 Z=0
  constraints (4):
    c: Diameter(g0) = 1.5
    c: PointOnObject(g0,g-3)
    c: PointOnObject(g1,g0)
    c: Coincident(g1,g-5)
FEATURE [PartDesign::Pocket] Pocket004
  BaseFeature = -> Revolution
  Direction = (0,1,-2e-16)
  Length = 5
  Length2 = 5
  Midplane = true
  Placement = pos=(0,0,0) rot=(1,0,0;1.5708rad)
  Profile = -> Sketch020
  ReferenceAxis = -> Sketch020 [N_Axis]
  Refine = true
  Suppressed = false
  Type = 1
FEATURE [Sketcher::SketchObject] Sketch021
  ArcFitTolerance = 1e-06
  AttachmentSupport = -> [Pocket004]
  ExternalGeometry = -> [Pocket004]
  FullyConstrained = true
  MakeInternals = false
  MapMode = 5
  Placement = pos=(-1.05178,2.2e-15,5.00023) rot=(0.994632,0,0.103476;3.14159rad)
  sketch-geometry (5):
    g0: Ellipse CenterX=116.678 CenterY=-1.42e-14 CenterZ=0 NormalX=0 NormalY=0 NormalZ=1 MajorRadius=21 MinorRadius=10 AngleXU=-1.5708
    g1: LineSegment [constr] StartX=116.678 StartY=-21 StartZ=0 EndX=116.678 EndY=21 EndZ=0
    g2: LineSegment [constr] StartX=126.678 StartY=-3.26795e-06 StartZ=0 EndX=106.678 EndY=3.26795e-06 EndZ=0
    g3: GeomPoint [constr] X=116.678 Y=-18.4662 Z=0
    g4: GeomPoint [constr] X=116.678 Y=18.4662 Z=0
  constraints (5):
    c: InternalAlignment(g1-g4 -> g0) x4
    c: Distance(g0,g1) = 21
    c: Angle(g1) = 1.5708
    c: Distance(g0,g2) = 10
    c: Coincident(g0,g-3)
FEATURE [PartDesign::Pad] Pad007
  BaseFeature = -> Pocket004
  Direction = (0.205841,0,-0.978585)
  Length = 3
  Length2 = 10
  Placement = pos=(0,0,0) rot=(1,0,0;1.5708rad)
  Profile = -> Sketch021
  ReferenceAxis = -> Sketch021 [N_Axis]
  Refine = true
  Reversed = true
  Suppressed = false
  Type = 0
  expr: Length = <<PinionCrossSection>>.Constraints.thickness
FEATURE [Sketcher::SketchObject] Sketch022  label="PinionServoMountingHoles"
  ArcFitTolerance = 1e-06
  AttachmentSupport = -> [Pad007]
  ExternalGeometry = -> [Pad007]
  FullyConstrained = true
  MakeInternals = false
  MapMode = 5
  Placement = pos=(-1.6693,3.5e-15,7.93599) rot=(-0.103476,0,0.994632;3.14159rad)
  sketch-geometry (4):
    g0: Circle CenterX=-116.678 CenterY=-1.26e-14 CenterZ=0 NormalX=0 NormalY=0 NormalZ=1 AngleXU=0 Radius=4
    g1: Circle CenterX=-116.678 CenterY=17 CenterZ=0 NormalX=0 NormalY=0 NormalZ=1 AngleXU=0 Radius=0.75
    g2: Circle CenterX=-101.678 CenterY=0 CenterZ=0 NormalX=0 NormalY=0 NormalZ=1 AngleXU=0 Radius=0.75
    g3: Circle CenterX=-116.678 CenterY=-17 CenterZ=0 NormalX=0 NormalY=0 NormalZ=1 AngleXU=0 Radius=0.75
  constraints (10):
    c: Diameter(g0) = 8  'ServoShaftDiameter'
    c: PointOnObject(g2,g-1)
    c: Equal(g2,g1)
    c: Equal(g1,g3)
    c: Diameter(g1) = 1.5
    c: DistanceX(g0,g2) = 15
    c: Symmetric(g1,g3,g0)
    c: DistanceY(g3,g1) = 34
    c: Vertical(g1,g3)
    c: Coincident(g0,g-3)
FEATURE [PartDesign::Pocket] Pocket005
  BaseFeature = -> Pad007
  Direction = (0.205841,0,-0.978585)
  Length = 5
  Length2 = 5
  Placement = pos=(0,0,0) rot=(1,0,0;1.5708rad)
  Profile = -> Sketch022
  ReferenceAxis = -> Sketch022 [N_Axis]
  Refine = true
  Suppressed = false
  Type = 1
FEATURE [PartDesign::Body] Body005  label="Pinion"
  AllowCompound = false
  Group = -> [Binder010,Binder011,Sketch019,Revolution,Sketch020,Pocket004,Sketch021,Pad007,Sketch022,Pocket005]
  Origin = -> Origin005
  Tip = -> Pocket005
FEATURE [PartDesign::SubShapeBinder] Binder012
  BindCopyOnChange = 0
  BindMode = 0
  ClaimChildren = false
  Context = -> Body006 [Binder012.]
  Fuse = false
  MakeFace = true
  OffsetFill = false
  OffsetIntersection = false
  OffsetJoinType = 0
  OffsetOpenResult = false
  PartialLoad = false
  Refine = true
  Relative = true
  Support = -> [Body002[Sketch006.]]
  _Version = 2
FEATURE [PartDesign::Pad] Pad008  label="StandFootPad"
  Direction = (0,1,0)
  Length = 60
  Length2 = 10
  Midplane = true
  Profile = -> Binder012
  Refine = true
  Suppressed = false
  Type = 0
FEATURE [PartDesign::Mirrored] Mirrored003
  BaseFeature = -> Pad008
  MirrorPlane = -> YZ_Plane006
  Originals = -> [Pad008]
  Refine = true
  Suppressed = false
  TransformMode = 0
FEATURE [PartDesign::SubShapeBinder] Binder013
  BindCopyOnChange = 0
  BindMode = 0
  ClaimChildren = false
  Context = -> Body006 [Binder013.]
  Fuse = false
  MakeFace = true
  OffsetFill = false
  OffsetIntersection = false
  OffsetJoinType = 0
  OffsetOpenResult = false
  PartialLoad = false
  Refine = true
  Relative = true
  Support = -> [Body005[Sketch019.]]
  _Version = 2
FEATURE [Sketcher::SketchObject] Sketch023  label="StandCrossSection"
  ArcFitTolerance = 1e-06
  AttachmentSupport = -> [XZ_Plane006]
  ExternalGeometry = -> [Mirrored003,Binder013]
  FullyConstrained = true
  MakeInternals = false
  MapMode = 5
  Placement = pos=(0,0,0) rot=(1,0,0;1.5708rad)
  expr: Constraints[18] = <<PinionCrossSection>>.Constraints.ServoBodyWidth
  expr: Constraints[8] = <<PinionCrossSection>>.Constraints.ServoShaftLength
  sketch-geometry (26):
    g0: LineSegment StartX=9.7 StartY=-11 StartZ=0 EndX=108.652 EndY=-11 EndZ=0
    g1: LineSegment StartX=59.8197 StartY=-4 StartZ=0 EndX=9.7 EndY=-4 EndZ=0
    g2: LineSegment StartX=9.7 StartY=-4 StartZ=0 EndX=9.7 EndY=-11 EndZ=0
    g3: LineSegment [constr] StartX=112.51 StartY=31.9532 StartZ=0 EndX=113.539 EndY=27.0602 EndZ=0
    g4: LineSegment [constr] StartX=104.732 StartY=25.2077 StartZ=0 EndX=122.347 EndY=28.9128 EndZ=0
    g5: LineSegment [constr] StartX=122.347 StartY=28.9128 StartZ=0 EndX=129.963 EndY=-7.29486 EndZ=0
    g6: LineSegment [constr] StartX=129.963 StartY=-7.29486 StartZ=0 EndX=112.348 EndY=-11 EndZ=0
    g7: LineSegment [constr] StartX=112.348 StartY=-11 StartZ=0 EndX=104.732 EndY=25.2077 EndZ=0
    g8: LineSegment [constr] StartX=106.688 StartY=15.9111 StartZ=0 EndX=124.302 EndY=19.6162 EndZ=0
    g9: LineSegment [constr] StartX=124.817 StartY=17.1698 StartZ=0 EndX=107.202 EndY=13.4646 EndZ=0
    g10: LineSegment StartX=107.202 StartY=13.4646 StartZ=0 EndX=124.817 EndY=17.1698 EndZ=0
    g11: LineSegment StartX=124.817 StartY=17.1698 StartZ=0 EndX=125.64 EndY=13.2554 EndZ=0
    g12: LineSegment StartX=123.187 StartY=7.04679 StartZ=0 EndX=112.054 EndY=-0.748697 EndZ=0
    g13: LineSegment StartX=110.839 StartY=-3.82368 StartZ=0 EndX=111.587 EndY=-7.38248 EndZ=0
    g14: ArcOfCircle CenterX=108.652 CenterY=-8 CenterZ=0 NormalX=0 NormalY=0 NormalZ=1 AngleXU=0 Radius=3 StartAngle=4.71239 EndAngle=6.49051
    g15: GeomPoint [constr] X=112.348 Y=-11 Z=0
    g16: ArcOfCircle CenterX=113.774 CenterY=-3.20615 CenterZ=0 NormalX=0 NormalY=0 NormalZ=1 AngleXU=0 Radius=3 StartAngle=2.18166 EndAngle=3.34892
    g17: GeomPoint [constr] X=110.431 Y=-1.88501 Z=0
    g18: ArcOfCircle CenterX=119.713 CenterY=12.0086 CenterZ=0 NormalX=0 NormalY=0 NormalZ=1 AngleXU=0 Radius=6.05726 StartAngle=5.32325 EndAngle=6.49051
    g19: GeomPoint [constr] X=126.463 Y=9.3411 Z=0
    g20: ArcOfCircle CenterX=107.82 CenterY=10.5289 CenterZ=0 NormalX=0 NormalY=0 NormalZ=1 AngleXU=0 Radius=3 StartAngle=1.77812 EndAngle=3.14159
    g21: LineSegment StartX=104.82 StartY=4 StartZ=0 EndX=61.8197 EndY=4 EndZ=0
    g22: LineSegment StartX=59.8197 StartY=-4 StartZ=0 EndX=59.8197 EndY=2 EndZ=0
    g23: ArcOfCircle CenterX=61.8197 CenterY=2 CenterZ=0 NormalX=0 NormalY=0 NormalZ=1 AngleXU=0 Radius=2 StartAngle=1.5708 EndAngle=3.14159
    g24: GeomPoint [constr] X=59.8197 Y=4 Z=0
    g25: LineSegment StartX=104.82 StartY=10.5289 StartZ=0 EndX=104.82 EndY=4 EndZ=0
  constraints (65):
    c: Coincident(g1,g2)
    c: Coincident(g2,g0)
    c: Horizontal(g0)
    c: Horizontal(g1)
    c: Coincident(g0,g-3)
    c: Coincident(g-3,g1)
    c: Coincident(g3,g-4)
    c: PointOnObject(g-4,g3)
    c: Distance(g3,g3) = 5
    c: Coincident(g4,g5)
    c: Coincident(g5,g6)
    c: Coincident(g6,g7)
    c: Coincident(g7,g4)
    c: Perpendicular(g4,g7)
    c: Perpendicular(g5,g4)
    c: Perpendicular(g6,g5)
    c: Parallel(g3,g7)
    c: Symmetric(g4,g4,g3)
    c: Distance(g6,g6) = 18
    c: PointOnObject(g8,g7)
    c: PointOnObject(g8,g5)
    c: PointOnObject(g9,g5)
    c: PointOnObject(g9,g7)
    c: Perpendicular(g8,g7)
    c: Perpendicular(g7,g9)
    c: Distance(g8,g9) = 2.5  'ServoFlangeThickness'
    c: Distance(g9,g5) = 25  'ServoUnderFlangeHeight'
    c: Coincident(g15,g6)
    c: Coincident(g10,g9)
    c: Coincident(g11,g9)
    c: PointOnObject(g19,g5)
    c: PointOnObject(g17,g7)
    c: Distance(g11,g19) = 8
    c: PointOnObject(g15,g0)
    c: PointOnObject(g15,g13)
    c: Tangent(g0,g14) = -1.5708
    c: Tangent(g13,g14) = 1.5708
    c: Radius(g14) = 3
    c: PointOnObject(g17,g13)
    c: PointOnObject(g17,g12)
    c: Tangent(g13,g16) = -1.5708
    c: Tangent(g12,g16) = -1.5708
    c: Radius(g16) = 3
    c: PointOnObject(g19,g12)
    c: Tangent(g11,g18) = 1.5708
    c: Tangent(g12,g18) = 1.5708
    c: Symmetric(g9,g19,g11)
    c: Horizontal(g21)
    c: Coincident(g22,g1)
    c: Vertical(g22)
    c: Coincident(g10,g9)
    c: Tangent(g20,g10) = 1.5708
    c: PointOnObject(g24,g22)
    c: PointOnObject(g24,g21)
    c: Tangent(g22,g23) = 1.5708
    c: Tangent(g21,g23) = -1.5708
    c: Radius(g23) = 2
    c: Distance(g24,g0) = 15
    c: Radius(g20) = 3
    c: Coincident(g25,g20)
    c: Coincident(g25,g21)
    c: Vertical(g25)
    c: DistanceX(g24,g21) = 45
    c: Horizontal(g20,g20)
    c: Angle(g12,g25) = 0.959931
FEATURE [PartDesign::Pad] Pad009
  BaseFeature = -> Mirrored003
  Direction = (0,-1,2e-16)
  Length = 60
  Length2 = 10
  Midplane = true
  Profile = -> Sketch023
  ReferenceAxis = -> Sketch023 [N_Axis]
  Refine = true
  Suppressed = false
  Type = 0
  expr: Length = <<StandFootPad>>.Length
FEATURE [Sketcher::SketchObject] Sketch024  label="ServoCutout"
  ArcFitTolerance = 1e-06
  AttachmentSupport = -> [Pad009]
  ExternalGeometry = -> [Pad009]
  FullyConstrained = true
  MakeInternals = false
  MapMode = 5
  Placement = pos=(1.83,-2e-15,-8.69996) rot=(0,-1,0;0.207323rad)
  sketch-geometry (4):
    g0: LineSegment StartX=107.678 StartY=19.5 StartZ=0 EndX=107.678 EndY=-19.5 EndZ=0
    g1: LineSegment StartX=107.678 StartY=-19.5 StartZ=0 EndX=125.678 EndY=-19.5 EndZ=0
    g2: LineSegment StartX=125.678 StartY=-19.5 StartZ=0 EndX=125.678 EndY=19.5 EndZ=0
    g3: LineSegment StartX=125.678 StartY=19.5 StartZ=0 EndX=107.678 EndY=19.5 EndZ=0
  constraints (11):
    c: Coincident(g0,g1)
    c: Coincident(g1,g2)
    c: Coincident(g2,g3)
    c: Coincident(g3,g0)
    c: Vertical(g0)
    c: Horizontal(g1)
    c: Horizontal(g3)
    c: PointOnObject(g0,g-3)
    c: PointOnObject(g1,g-4)
    c: DistanceY(g2,g2) = 39  'ServoDepth'
    c: Symmetric(g2,g1,g-1)
FEATURE [PartDesign::Pocket] Pocket006
  BaseFeature = -> Pad009
  Direction = (0.205841,0,-0.978585)
  Length = 5
  Length2 = 5
  Profile = -> Sketch024
  ReferenceAxis = -> Sketch024 [N_Axis]
  Refine = true
  Suppressed = false
  Type = 1
FEATURE [Sketcher::SketchObject] Sketch025
  ArcFitTolerance = 1e-06
  AttachmentSupport = -> [Pad009]
  ExternalGeometry = -> [Pad009]
  FullyConstrained = true
  MakeInternals = false
  MapMode = 5
  Placement = pos=(1.83,-2e-15,-8.69996) rot=(0,-1,0;0.207323rad)
  sketch-geometry (5):
    g0: LineSegment [constr] StartX=116.678 StartY=30 StartZ=0 EndX=116.678 EndY=-30 EndZ=0
    g1: Circle CenterX=111.678 CenterY=23.5 CenterZ=0 NormalX=0 NormalY=0 NormalZ=1 AngleXU=0 Radius=1.5
    g2: Circle CenterX=121.678 CenterY=23.5 CenterZ=0 NormalX=0 NormalY=0 NormalZ=1 AngleXU=0 Radius=1.5
    g3: Circle CenterX=111.678 CenterY=-23.5 CenterZ=0 NormalX=0 NormalY=0 NormalZ=1 AngleXU=0 Radius=1.5
    g4: Circle CenterX=121.678 CenterY=-23.5 CenterZ=0 NormalX=0 NormalY=0 NormalZ=1 AngleXU=0 Radius=1.5
  constraints (12):
    c: Vertical(g0)
    c: Symmetric(g-3,g-4,g0)
    c: Symmetric(g1,g2,g0)
    c: Symmetric(g3,g4,g0)
    c: Symmetric(g3,g1,g-1)
    c: DistanceY(g4,g2) = 47
    c: DistanceX(g1,g2) = 10
    c: Equal(g1,g2)
    c: Equal(g2,g4)
    c: Equal(g4,g3)
    c: Diameter(g1) = 3
    c: Horizontal(g0,g-4)
FEATURE [PartDesign::Hole] Hole005  label="ServoScrews"
  BaseFeature = -> Pocket006
  CustomThreadClearance = 0
  Depth = 303.612
  DepthType = 1
  Diameter = 5.5
  DrillForDepth = false
  DrillPoint = 1
  DrillPointAngle = 118
  HoleCutCountersinkAngle = 90
  HoleCutCustomValues = false
  HoleCutDepth = 6.5
  HoleCutDiameter = 6.5
  HoleCutType = 1
  ModelThread = false
  Profile = -> Sketch025
  Refine = true
  Suppressed = false
  Tapered = false
  TaperedAngle = 90
  ThreadClass = 0
  ThreadDepth = 303.612
  ThreadDepthType = 0
  ThreadDirection = 0
  ThreadFit = 0
  ThreadSize = 13
  ThreadType = 1
  Threaded = false
  UseCustomThreadClearance = false
FEATURE [Sketcher::SketchObject] Sketch026
  ArcFitTolerance = 1e-06
  AttachmentSupport = -> [XY_Plane006]
  FullyConstrained = true
  MakeInternals = false
  MapMode = 5
  sketch-geometry (1):
    g0: Circle CenterX=0 CenterY=0 CenterZ=0 NormalX=0 NormalY=0 NormalZ=1 AngleXU=0 Radius=1.5
  constraints (2):
    c: Diameter(g0) = 3
    c: Coincident(g0,g-1)
FEATURE [PartDesign::Hole] Hole006  label="Rail Screw"
  BaseFeature = -> Hole005
  CustomThreadClearance = 0
  Depth = 303.612
  DepthType = 1
  Diameter = 4.4
  DrillForDepth = false
  DrillPoint = 1
  DrillPointAngle = 118
  HoleCutCountersinkAngle = 90
  HoleCutCustomValues = false
  HoleCutDepth = 0
  HoleCutDiameter = 6.1
  HoleCutType = 0
  ModelThread = false
  Profile = -> Sketch026
  Refine = true
  Suppressed = false
  Tapered = false
  TaperedAngle = 90
  ThreadClass = 0
  ThreadDepth = 303.612
  ThreadDepthType = 0
  ThreadDirection = 0
  ThreadFit = 0
  ThreadSize = 0
  ThreadType = 0
  Threaded = false
  UseCustomThreadClearance = false
FEATURE [Sketcher::SketchObject] Sketch027
  ArcFitTolerance = 1e-06
  AttachmentSupport = -> [Hole006]
  ExternalGeometry = -> [Hole006]
  FullyConstrained = true
  MakeInternals = false
  MapMode = 5
  Placement = pos=(0,0,-11) rot=(1,0,0;3.14159rad)
  expr: Constraints[23] = <<FootPads>>.Constraints.FootDiameter
  sketch-geometry (11):
    g0: LineSegment [constr] StartX=0 StartY=20.3 StartZ=0 EndX=0 EndY=-20.3 EndZ=0
    g1: LineSegment [constr] StartX=0 StartY=-20.3 StartZ=0 EndX=103.652 EndY=-20.3 EndZ=0
    g2: LineSegment [constr] StartX=103.652 StartY=-20.3 StartZ=0 EndX=103.652 EndY=20.3 EndZ=0
    g3: LineSegment [constr] StartX=103.652 StartY=20.3 StartZ=0 EndX=0 EndY=20.3 EndZ=0
    g4: LineSegment [constr] StartX=0 StartY=20.3 StartZ=0 EndX=-9.7 EndY=20.3 EndZ=0
    g5: LineSegment [constr] StartX=0 StartY=20.3 StartZ=0 EndX=0 EndY=30 EndZ=0
    g6: Circle CenterX=0 CenterY=20.3 CenterZ=0 NormalX=0 NormalY=0 NormalZ=1 AngleXU=0 Radius=5
    g7: Circle CenterX=103.652 CenterY=20.3 CenterZ=0 NormalX=0 NormalY=0 NormalZ=1 AngleXU=0 Radius=5
    g8: Circle CenterX=103.652 CenterY=-20.3 CenterZ=0 NormalX=0 NormalY=0 NormalZ=1 AngleXU=0 Radius=5
    g9: Circle CenterX=0 CenterY=-20.3 CenterZ=0 NormalX=0 NormalY=0 NormalZ=1 AngleXU=0 Radius=5
    g10: GeomPoint [constr] X=108.652 Y=20.3 Z=0
  constraints (27):
    c: Coincident(g0,g1)
    c: Coincident(g1,g2)
    c: Coincident(g2,g3)
    c: Coincident(g3,g0)
    c: Vertical(g0)
    c: Horizontal(g1)
    c: Horizontal(g3)
    c: Symmetric(g2,g1,g-1)
    c: PointOnObject(g-1,g0)
    c: Coincident(g4,g0)
    c: PointOnObject(g4,g-3)
    c: Horizontal(g4)
    c: Coincident(g5,g0)
    c: PointOnObject(g5,g-2)
    c: Horizontal(g-3,g5)
    c: Equal(g4,g5)
    c: Coincident(g6,g0)
    c: Coincident(g7,g2)
    c: Coincident(g8,g1)
    c: Coincident(g9,g0)
    c: Equal(g9,g8)
    c: Equal(g8,g7)
    c: Equal(g7,g6)
    c: Diameter(g6) = 10
    c: PointOnObject(g10,g7)
    c: Horizontal(g2,g10)
    c: PointOnObject(g10,g-4)
FEATURE [PartDesign::Pocket] Pocket007  label="FootPads001"
  BaseFeature = -> Hole006
  Direction = (0,0,1)
  Length = 3
  Length2 = 5
  Profile = -> Sketch027
  ReferenceAxis = -> Sketch027 [N_Axis]
  Refine = true
  Suppressed = false
  Type = 0
  expr: Length = <<FootPadPocket>>.Length
FEATURE [Sketcher::SketchObject] Sketch028  label="FootPads"
  ArcFitTolerance = 1e-06
  AttachmentSupport = -> [Hole002]
  ExternalGeometry = -> [Hole002]
  FullyConstrained = true
  MakeInternals = false
  MapMode = 5
  Placement = pos=(0,-4.7e-15,-11) rot=(1,0,0;3.14159rad)
  sketch-geometry (3):
    g0: Circle CenterX=0 CenterY=12 CenterZ=0 NormalX=0 NormalY=0 NormalZ=1 AngleXU=0 Radius=5
    g1: GeomPoint X=0 Y=20 Z=0
    g2: GeomPoint X=0 Y=17 Z=0
  constraints (7):
    c: PointOnObject(g0,g-2)
    c: Diameter(g0) = 10  'FootDiameter'
    c: PointOnObject(g1,g-2)
    c: PointOnObject(g2,g0)
    c: PointOnObject(g2,g-2)
    c: Distance(g2,g1) = 3
    c: PointOnObject(g1,g-3)
FEATURE [PartDesign::Pocket] Pocket008  label="FootPadPocket"
  BaseFeature = -> Hole002
  Direction = (0,0,1)
  Length = 3
  Length2 = 5
  Placement = pos=(0,0,0) rot=(1,0,0;1.5708rad)
  Profile = -> Sketch028
  ReferenceAxis = -> Sketch028 [N_Axis]
  Refine = true
  Suppressed = false
  Type = 0
FEATURE [PartDesign::SubShapeBinder] Binder014
  BindCopyOnChange = 0
  BindMode = 0
  ClaimChildren = false
  Context = -> Body007 [Binder014.]
  Fuse = false
  MakeFace = true
  OffsetFill = false
  OffsetIntersection = false
  OffsetJoinType = 0
  OffsetOpenResult = false
  PartialLoad = false
  Refine = true
  Relative = true
  Support = -> [Body005[Sketch019.]]
  _Version = 2
FEATURE [Sketcher::SketchObject] Sketch029
  ArcFitTolerance = 1e-06
  AttachmentSupport = -> [XZ_Plane008]
  ExternalGeometry = -> [Binder014]
  FullyConstrained = true
  MakeInternals = false
  MapMode = 5
  Placement = pos=(0,0,0) rot=(1,0,0;1.5708rad)
  expr: Constraints[12] = <<PinionCrossSection>>.Constraints.ServoBodyHeight
  expr: Constraints[13] = <<PinionCrossSection>>.Constraints.ServoBodyWidth
  expr: Constraints[2] = <<PinionCrossSection>>.Constraints.ServoShaftLength
  sketch-geometry (5):
    g0: LineSegment [constr] StartX=112.51 StartY=31.9532 StartZ=0 EndX=113.539 EndY=27.0602 EndZ=0
    g1: LineSegment StartX=104.732 StartY=25.2077 StartZ=0 EndX=122.347 EndY=28.9128 EndZ=0
    g2: LineSegment StartX=122.347 StartY=28.9128 StartZ=0 EndX=129.963 EndY=-7.29486 EndZ=0
    g3: LineSegment StartX=129.963 StartY=-7.29486 StartZ=0 EndX=112.348 EndY=-11 EndZ=0
    g4: LineSegment StartX=112.348 StartY=-11 StartZ=0 EndX=104.732 EndY=25.2077 EndZ=0
  constraints (14):
    c: Coincident(g0,g-3)
    c: PointOnObject(g-3,g0)
    c: Distance(g0,g0) = 5
    c: Coincident(g1,g2)
    c: Coincident(g2,g3)
    c: Coincident(g3,g4)
    c: Coincident(g4,g1)
    c: Perpendicular(g1,g4)
    c: Perpendicular(g2,g1)
    c: Perpendicular(g3,g2)
    c: Parallel(g0,g2)
    c: Symmetric(g1,g1,g0)
    c: Distance(g2,g2) = 37
    c: Distance(g3,g3) = 18
FEATURE [PartDesign::Pad] Pad010
  Direction = (0,-1,2e-16)
  Length = 39
  Length2 = 10
  Midplane = true
  Placement = pos=(0,0,0) rot=(1,0,0;1.5708rad)
  Profile = -> Sketch029
  ReferenceAxis = -> Sketch029 [N_Axis]
  Refine = true
  Suppressed = false
  Type = 0
  expr: Length = <<ServoCutout>>.Constraints.ServoDepth
FEATURE [Sketcher::SketchObject] Sketch030
  ArcFitTolerance = 1e-06
  AttachmentSupport = -> [XZ_Plane008]
  ExternalGeometry = -> [Pad010]
  FullyConstrained = true
  MakeInternals = false
  MapMode = 5
  Placement = pos=(0,0,0) rot=(1,0,0;1.5708rad)
  expr: Constraints[10] = <<StandCrossSection>>.Constraints.ServoFlangeThickness
  expr: Constraints[11] = <<StandCrossSection>>.Constraints.ServoUnderFlangeHeight
  sketch-geometry (4):
    g0: LineSegment StartX=106.688 StartY=15.9111 StartZ=0 EndX=107.202 EndY=13.4646 EndZ=0
    g1: LineSegment StartX=107.202 StartY=13.4646 StartZ=0 EndX=124.817 EndY=17.1698 EndZ=0
    g2: LineSegment StartX=124.817 StartY=17.1698 StartZ=0 EndX=124.302 EndY=19.6162 EndZ=0
    g3: LineSegment StartX=124.302 StartY=19.6162 StartZ=0 EndX=106.688 EndY=15.9111 EndZ=0
  constraints (12):
    c: PointOnObject(g0,g-3)
    c: PointOnObject(g0,g-3)
    c: Coincident(g0,g1)
    c: PointOnObject(g1,g-4)
    c: Coincident(g1,g2)
    c: PointOnObject(g2,g-4)
    c: Coincident(g2,g3)
    c: Coincident(g3,g0)
    c: Perpendicular(g3,g-3)
    c: Perpendicular(g1,g-3)
    c: Distance(g2,g2) = 2.5
    c: Distance(g1,g-4) = 25
FEATURE [PartDesign::Pad] Pad011
  BaseFeature = -> Pad010
  Direction = (0,-1,2e-16)
  Length = 55
  Length2 = 10
  Midplane = true
  Placement = pos=(0,0,0) rot=(1,0,0;1.5708rad)
  Profile = -> Sketch030
  ReferenceAxis = -> Sketch030 [N_Axis]
  Refine = true
  Suppressed = false
  Type = 0
FEATURE [Sketcher::SketchObject] Sketch031
  ArcFitTolerance = 1e-06
  AttachmentSupport = -> [Pad011]
  ExternalGeometry = -> [Pad011]
  FullyConstrained = true
  MakeInternals = false
  MapMode = 5
  Placement = pos=(-0.640095,1.3e-15,3.04306) rot=(-0.103476,0,0.994632;3.14159rad)
  expr: Constraints[1] = <<PinionServoMountingHoles>>.Constraints.ServoShaftDiameter
  sketch-geometry (1):
    g0: Circle CenterX=-116.678 CenterY=-3.2e-15 CenterZ=0 NormalX=0 NormalY=0 NormalZ=1 AngleXU=0 Radius=4
  constraints (2):
    c: Symmetric(g-3,g-4,g0)
    c: Diameter(g0) = 8
FEATURE [PartDesign::Pad] Pad012
  BaseFeature = -> Pad011
  Direction = (-0.205841,0,0.978585)
  Length = 5
  Length2 = 10
  Placement = pos=(0,0,0) rot=(1,0,0;1.5708rad)
  Profile = -> Sketch031
  ReferenceAxis = -> Sketch031 [N_Axis]
  Refine = true
  Suppressed = false
  Type = 0
  expr: Length = <<PinionCrossSection>>.Constraints.ServoShaftLength
FEATURE [PartDesign::SubShapeBinder] Binder015
  BindCopyOnChange = 0
  BindMode = 0
  ClaimChildren = false
  Context = -> Body007 [Binder015.]
  Fuse = false
  MakeFace = true
  OffsetFill = false
  OffsetIntersection = false
  OffsetJoinType = 0
  OffsetOpenResult = false
  PartialLoad = false
  Refine = true
  Relative = true
  Support = -> [Body006[Pocket007.Edge105,Pocket007.Edge104,Pocket007.Edge91,Pocket007.Edge92]]
  _Version = 2
FEATURE [PartDesign::Pocket] Pocket009
  BaseFeature = -> Pad012
  Direction = (0.205841,0,-0.978585)
  Length = 5
  Length2 = 5
  Placement = pos=(0,0,0) rot=(1,0,0;1.5708rad)
  Profile = -> Binder015
  Refine = true
  Reversed = true
  Suppressed = false
  Type = 1
FEATURE [PartDesign::Body] Body007  label="Servo"
  AllowCompound = false
  Group = -> [Binder014,Sketch029,Pad010,Sketch030,Pad011,Sketch031,Pad012,Binder015,Pocket009]
  Origin = -> Origin008
  Tip = -> Pocket009
FEATURE [Sketcher::SketchObject] Sketch032  label="FootEndBlock"
  ArcFitTolerance = 1e-06
  AttachmentSupport = -> [Pocket008]
  ExternalGeometry = -> [Pocket008]
  FullyConstrained = true
  MakeInternals = false
  MapMode = 5
  Placement = pos=(0,-1.8e-15,-4) rot=(0,0,1;3.14159rad)
  expr: Constraints[11] = <<RailHolePosition>>.Constraints.E + 1 mm
  sketch-geometry (5):
    g0: LineSegment StartX=-9.7 StartY=20 StartZ=0 EndX=-9.7 EndY=8.5 EndZ=0
    g1: LineSegment StartX=-9.7 StartY=8.5 StartZ=0 EndX=9.7 EndY=8.5 EndZ=0
    g2: LineSegment StartX=9.7 StartY=8.5 StartZ=0 EndX=9.7 EndY=20 EndZ=0
    g3: LineSegment StartX=9.7 StartY=20 StartZ=0 EndX=-9.7 EndY=20 EndZ=0
    g4: LineSegment [constr] StartX=-9.7 StartY=13.5 StartZ=0 EndX=9.7 EndY=13.5 EndZ=0
  constraints (15):
    c: Coincident(g0,g1)
    c: Coincident(g1,g2)
    c: Coincident(g2,g3)
    c: Coincident(g3,g0)
    c: Vertical(g0)
    c: Vertical(g2)
    c: Horizontal(g1)
    c: Horizontal(g3)
    c: PointOnObject(g4,g0)
    c: PointOnObject(g4,g2)
    c: Horizontal(g4)
    c: DistanceY(g-1,g4) = 13.5
    c: DistanceY(g1,g4) = 5  'Overhang'
    c: Vertical(g0,g-3)
    c: Coincident(g-3,g2)
FEATURE [PartDesign::Pad] Pad013
  BaseFeature = -> Pocket008
  Direction = (0,0,1)
  Length = 13
  Length2 = 10
  Placement = pos=(0,0,0) rot=(1,0,0;1.5708rad)
  Profile = -> Sketch032
  ReferenceAxis = -> Sketch032 [N_Axis]
  Refine = true
  Suppressed = false
  Type = 0
  expr: Length = <<Block Cross-Section>>.Constraints.Height
FEATURE [PartDesign::Fillet] Fillet
  Base = -> Pocket003 [Edge59,Edge62]
  BaseFeature = -> Pocket003
  Placement = pos=(0,0,0) rot=(1,0,0;1.5708rad)
  Radius = 3
  Refine = true
  SupportTransform = false
  Suppressed = false
  UseAllEdges = false
FEATURE [PartDesign::Body] Body004  label="Rack"
  AllowCompound = false
  Group = -> [Binder008,Sketch012,Pad005,Binder009,Sketch015,Pad006,Sketch016,Hole004,Sketch017,Pocket002,Sketch018,Pocket003,Fillet]
  Origin = -> Origin004
  Tip = -> Fillet
FEATURE [Sketcher::SketchObject] Sketch033
  ArcFitTolerance = 1e-06
  AttachmentSupport = -> [Pad013]
  FullyConstrained = true
  MakeInternals = false
  MapMode = 5
  Placement = pos=(0,-8.5,1.9e-15) rot=(-1,0,0;1.5708rad)
  expr: Constraints[10] = <<Rail Cross-Section>>.Constraints.Hr + 0.5 mm
  sketch-geometry (4):
    g0: LineSegment StartX=-6.1 StartY=4 StartZ=0 EndX=-6.1 EndY=-4.5 EndZ=0
    g1: LineSegment StartX=-6.1 StartY=-4.5 StartZ=0 EndX=6.1 EndY=-4.5 EndZ=0
    g2: LineSegment StartX=6.1 StartY=-4.5 StartZ=0 EndX=6.1 EndY=4 EndZ=0
    g3: LineSegment StartX=6.1 StartY=4 StartZ=0 EndX=-6.1 EndY=4 EndZ=0
  constraints (11):
    c: Coincident(g0,g1)
    c: Coincident(g1,g2)
    c: Coincident(g2,g3)
    c: Coincident(g3,g0)
    c: Vertical(g0)
    c: Vertical(g2)
    c: Horizontal(g1)
    c: Horizontal(g3)
    c: Coincident(g0,g-3)
    c: PointOnObject(g-4,g2)
    c: DistanceY(g2,g2) = 8.5
FEATURE [PartDesign::Pocket] Pocket010
  BaseFeature = -> Pad013
  Direction = (0,-1,-2e-16)
  Length = 5
  Length2 = 5
  Placement = pos=(0,0,0) rot=(1,0,0;1.5708rad)
  Profile = -> Sketch033
  ReferenceAxis = -> Sketch033 [N_Axis]
  Refine = true
  Suppressed = false
  Type = 0
  expr: Length = <<FootEndBlock>>.Constraints.Overhang
FEATURE [Sketcher::SketchObject] Sketch034
  ArcFitTolerance = 1e-06
  AttachmentSupport = -> [XY_Plane009]
  FullyConstrained = true
  MakeInternals = false
  MapMode = 5
  sketch-geometry (14):
    g0: LineSegment StartX=-10.5 StartY=-25.5 StartZ=0 EndX=10.5 EndY=-25.5 EndZ=0
    g1: LineSegment StartX=10.5 StartY=-25.5 StartZ=0 EndX=10.5 EndY=25.5 EndZ=0
    g2: LineSegment StartX=10.5 StartY=25.5 StartZ=0 EndX=-10.5 EndY=25.5 EndZ=0
    g3: LineSegment StartX=-10.5 StartY=25.5 StartZ=0 EndX=-10.5 EndY=-25.5 EndZ=0
    g4: GeomPoint [constr] X=0 Y=0 Z=0
    g5: LineSegment [constr] StartX=-5.7 StartY=-23.5 StartZ=0 EndX=5.7 EndY=-23.5 EndZ=0
    g6: LineSegment [constr] StartX=5.7 StartY=-23.5 StartZ=0 EndX=5.7 EndY=23.5 EndZ=0
    g7: LineSegment [constr] StartX=5.7 StartY=23.5 StartZ=0 EndX=-5.7 EndY=23.5 EndZ=0
    g8: LineSegment [constr] StartX=-5.7 StartY=23.5 StartZ=0 EndX=-5.7 EndY=-23.5 EndZ=0
    g9: GeomPoint [constr] X=0 Y=0 Z=0
    g10: Circle CenterX=-5.7 CenterY=23.5 CenterZ=0 NormalX=0 NormalY=0 NormalZ=1 AngleXU=0 Radius=1.05
    g11: Circle CenterX=5.7 CenterY=23.5 CenterZ=0 NormalX=0 NormalY=0 NormalZ=1 AngleXU=0 Radius=1.05
    g12: Circle CenterX=-5.7 CenterY=-23.5 CenterZ=0 NormalX=0 NormalY=0 NormalZ=1 AngleXU=0 Radius=1.05
    g13: Circle CenterX=5.7 CenterY=-23.5 CenterZ=0 NormalX=0 NormalY=0 NormalZ=1 AngleXU=0 Radius=1.05
  constraints (32):
    c: Coincident(g0,g1)
    c: Coincident(g1,g2)
    c: Coincident(g2,g3)
    c: Coincident(g3,g0)
    c: Horizontal(g0)
    c: Horizontal(g2)
    c: Vertical(g1)
    c: Vertical(g3)
    c: Symmetric(g2,g0,g4)
    c: Distance(g1,g3) = 21
    c: Distance(g0,g2) = 51  'Height'
    c: Coincident(g4,g-1)
    c: Coincident(g5,g6)
    c: Coincident(g6,g7)
    c: Coincident(g7,g8)
    c: Coincident(g8,g5)
    c: Horizontal(g5)
    c: Horizontal(g7)
    c: Vertical(g6)
    c: Vertical(g8)
    c: Symmetric(g7,g5,g9)
    c: Distance(g6,g8) = 11.4
    c: Coincident(g9,g4)
    c: Distance(g5,g0) = 2
    c: Coincident(g10,g7)
    c: Coincident(g11,g6)
    c: Coincident(g12,g5)
    c: Coincident(g13,g5)
    c: Equal(g10,g11)
    c: Equal(g11,g12)
    c: Equal(g12,g13)
    c: Diameter(g10) = 2.1  'HoleDiameter'
FEATURE [PartDesign::Pad] Pad014  label="Board"
  Direction = (0,0,1)
  Length = 1
  Length2 = 10
  Profile = -> Sketch034
  ReferenceAxis = -> Sketch034 [N_Axis]
  Refine = true
  Suppressed = false
  Type = 0
FEATURE [Sketcher::SketchObject] Sketch035
  ArcFitTolerance = 1e-06
  AttachmentOffset = pos=(0,0,-0.3) rot=(0,0,1;0rad)
  AttachmentSupport = -> [Pad014]
  ExternalGeometry = -> [Pad014]
  FullyConstrained = true
  MakeInternals = false
  MapMode = 5
  Placement = pos=(0,0,0.7) rot=(0,0,1;0rad)
  sketch-geometry (5):
    g0: LineSegment StartX=-4 StartY=26.8 StartZ=0 EndX=-4 EndY=20.8 EndZ=0
    g1: LineSegment StartX=-4 StartY=20.8 StartZ=0 EndX=4 EndY=20.8 EndZ=0
    g2: LineSegment StartX=4 StartY=20.8 StartZ=0 EndX=4 EndY=26.8 EndZ=0
    g3: LineSegment StartX=4 StartY=26.8 StartZ=0 EndX=-4 EndY=26.8 EndZ=0
    g4: GeomPoint X=0 Y=26.8 Z=0
  constraints (13):
    c: Coincident(g0,g1)
    c: Coincident(g1,g2)
    c: Coincident(g2,g3)
    c: Coincident(g3,g0)
    c: Vertical(g0)
    c: Vertical(g2)
    c: Horizontal(g1)
    c: Horizontal(g3)
    c: Distance(g0,g2) = 8
    c: DistanceY(g0,g0) = 6
    c: Distance(g-3,g3) = 1.3
    c: Symmetric(g3,g3,g4)
    c: PointOnObject(g4,g-2)
FEATURE [PartDesign::Pad] Pad015  label="Socket"
  BaseFeature = -> Pad014
  Direction = (0,0,1)
  Length = 3
  Length2 = 10
  Profile = -> Sketch035
  ReferenceAxis = -> Sketch035 [N_Axis]
  Refine = true
  Suppressed = false
  Type = 0
FEATURE [Sketcher::SketchObject] Sketch036
  ArcFitTolerance = 1e-06
  AttachmentSupport = -> [Pad015]
  ExternalGeometry = -> [Pad015]
  FullyConstrained = true
  MakeInternals = false
  MapMode = 5
  Placement = pos=(0,26.8,0) rot=(0,0.707107,0.707107;3.14159rad)
  sketch-geometry (5):
    g0: LineSegment StartX=-5.5 StartY=-2.3 StartZ=0 EndX=5.5 EndY=-2.3 EndZ=0
    g1: LineSegment StartX=5.5 StartY=-2.3 StartZ=0 EndX=5.5 EndY=6.7 EndZ=0
    g2: LineSegment StartX=5.5 StartY=6.7 StartZ=0 EndX=-5.5 EndY=6.7 EndZ=0
    g3: LineSegment StartX=-5.5 StartY=6.7 StartZ=0 EndX=-5.5 EndY=-2.3 EndZ=0
    g4: GeomPoint [constr] X=1e-16 Y=2.2 Z=0
  constraints (12):
    c: Coincident(g0,g1)
    c: Coincident(g1,g2)
    c: Coincident(g2,g3)
    c: Coincident(g3,g0)
    c: Horizontal(g0)
    c: Horizontal(g2)
    c: Vertical(g1)
    c: Vertical(g3)
    c: Symmetric(g2,g0,g4)
    c: Distance(g1,g3) = 11
    c: Distance(g0,g2) = 9
    c: Symmetric(g-3,g-4,g4)
FEATURE [PartDesign::Pad] Pad016  label="Keepout"
  BaseFeature = -> Pad015
  Direction = (0,1,-2e-16)
  Length = 10
  Length2 = 10
  Profile = -> Sketch036
  ReferenceAxis = -> Sketch036 [N_Axis]
  Refine = true
  Suppressed = false
  Type = 0
FEATURE [PartDesign::Body] Body008  label="PicoW"
  AllowCompound = false
  Group = -> [Sketch034,Pad014,Sketch035,Pad015,Sketch036,Pad016]
  Origin = -> Origin009
  Placement = pos=(90,0,-6) rot=(0,0,1;3.14159rad)
  Tip = -> Pad016
FEATURE [PartDesign::SubShapeBinder] Binder016
  BindCopyOnChange = 0
  BindMode = 0
  ClaimChildren = false
  Context = -> Body006 [Binder016.]
  Fuse = false
  MakeFace = true
  OffsetFill = false
  OffsetIntersection = false
  OffsetJoinType = 0
  OffsetOpenResult = false
  PartialLoad = false
  Refine = true
  Relative = true
  Support = -> [Body008[Pad016.Face4]]
  _Version = 2
FEATURE [Sketcher::SketchObject] Sketch037
  ArcFitTolerance = 1e-06
  AttachmentSupport = -> [Pocket007]
  ExternalGeometry = -> [Binder016,Pocket007]
  FullyConstrained = true
  MakeInternals = false
  MapMode = 5
  Placement = pos=(0,9e-16,4) rot=(0,0,1;0rad)
  sketch-geometry (6):
    g0: LineSegment StartX=65.8197 StartY=26 StartZ=0 EndX=65.8197 EndY=-26 EndZ=0
    g1: LineSegment StartX=65.8197 StartY=-26 StartZ=0 EndX=100.82 EndY=-26 EndZ=0
    g2: LineSegment StartX=100.82 StartY=-26 StartZ=0 EndX=100.82 EndY=26 EndZ=0
    g3: LineSegment StartX=100.82 StartY=26 StartZ=0 EndX=65.8197 EndY=26 EndZ=0
    g4: LineSegment [constr] StartX=65.8197 StartY=-26 StartZ=0 EndX=61.8197 EndY=-26 EndZ=0
    g5: LineSegment [constr] StartX=100.82 StartY=-26 StartZ=0 EndX=104.82 EndY=-26 EndZ=0
  constraints (17):
    c: Coincident(g0,g1)
    c: Coincident(g1,g2)
    c: Coincident(g2,g3)
    c: Coincident(g3,g0)
    c: Vertical(g2)
    c: Horizontal(g1)
    c: Horizontal(g3)
    c: Symmetric(g0,g0,g-1)
    c: Distance(g1,g-4) = 0.5
    c: Coincident(g4,g0)
    c: Horizontal(g4)
    c: Coincident(g5,g1)
    c: Horizontal(g5)
    c: Vertical(g5,g-6)
    c: Vertical(g4,g-5)
    c: Equal(g4,g5)
    c: Distance(g-5,g0) = 4
FEATURE [PartDesign::Pocket] Pocket011  label="ElectronicsCarveOut"
  BaseFeature = -> Pocket007
  Direction = (0,0,-1)
  Length = 0
  Length2 = 5
  Offset = 1
  Profile = -> Sketch037
  ReferenceAxis = -> Sketch037 [N_Axis]
  Refine = true
  Suppressed = false
  Type = 3
  UpToFace = -> Binder016 [Face1]
FEATURE [Sketcher::SketchObject] Sketch038
  ArcFitTolerance = 1e-06
  AttachmentSupport = -> [Pocket011]
  ExternalGeometry = -> [Binder016]
  FullyConstrained = true
  MakeInternals = false
  MapMode = 5
  Placement = pos=(0,0,-7) rot=(0,0,1;0rad)
  sketch-geometry (6):
    g0: Circle CenterX=84.3 CenterY=23.5 CenterZ=0 NormalX=0 NormalY=0 NormalZ=1 AngleXU=0 Radius=2.35
    g1: Circle CenterX=95.7 CenterY=23.5 CenterZ=0 NormalX=0 NormalY=0 NormalZ=1 AngleXU=0 Radius=2.35
    g2: Circle CenterX=84.3 CenterY=-23.5 CenterZ=0 NormalX=0 NormalY=0 NormalZ=1 AngleXU=0 Radius=2.35
    g3: Circle CenterX=95.7 CenterY=-23.5 CenterZ=0 NormalX=0 NormalY=0 NormalZ=1 AngleXU=0 Radius=2.35
    g4: GeomPoint X=84.3 Y=24.55 Z=0
    g5: GeomPoint X=84.3 Y=25.85 Z=0
  constraints (12):
    c: Coincident(g0,g-3)
    c: Coincident(g1,g-4)
    c: Coincident(g2,g-5)
    c: Coincident(g3,g-6)
    c: Equal(g2,g3)
    c: Equal(g3,g0)
    c: Equal(g0,g1)
    c: PointOnObject(g4,g-3)
    c: PointOnObject(g5,g0)
    c: Vertical(g0,g4)
    c: Vertical(g4,g5)
    c: Distance(g4,g0) = 1.3
FEATURE [PartDesign::Pad] Pad017  label="PCBStandoff"
  BaseFeature = -> Pocket011
  Direction = (0,0,1)
  Length = 10
  Length2 = 10
  Profile = -> Sketch038
  ReferenceAxis = -> Sketch038 [N_Axis]
  Refine = true
  Suppressed = false
  Type = 3
  UpToFace = -> Binder016 [Face1]
FEATURE [Sketcher::SketchObject] Sketch039
  ArcFitTolerance = 1e-06
  AttachmentSupport = -> [Pad017]
  ExternalGeometry = -> [Binder016]
  FullyConstrained = true
  MakeInternals = false
  MapMode = 5
  Placement = pos=(0,0,-6) rot=(0,0,1;0rad)
  sketch-geometry (4):
    g0: Circle CenterX=84.3 CenterY=23.5 CenterZ=0 NormalX=0 NormalY=0 NormalZ=1 AngleXU=0 Radius=1.05
    g1: Circle CenterX=95.7 CenterY=23.5 CenterZ=0 NormalX=0 NormalY=0 NormalZ=1 AngleXU=0 Radius=1.05
    g2: Circle CenterX=84.3 CenterY=-23.5 CenterZ=0 NormalX=0 NormalY=0 NormalZ=1 AngleXU=0 Radius=1.05
    g3: Circle CenterX=95.7 CenterY=-23.5 CenterZ=0 NormalX=0 NormalY=0 NormalZ=1 AngleXU=0 Radius=1.05
  constraints (8):
    c: Coincident(g0,g-3)
    c: Equal(g0,g-3)
    c: Coincident(g1,g-4)
    c: Equal(g1,g-4)
    c: Coincident(g2,g-5)
    c: Equal(g2,g-5)
    c: Coincident(g3,g-6)
    c: Equal(g3,g-6)
FEATURE [PartDesign::Hole] Hole007  label="PCBMountHoles"
  BaseFeature = -> Pad017
  CustomThreadClearance = 0
  Depth = 3.5
  DepthType = 0
  Diameter = 3
  DrillForDepth = false
  DrillPoint = 0
  DrillPointAngle = 118
  HoleCutCountersinkAngle = 90
  HoleCutCustomValues = false
  HoleCutDepth = 0
  HoleCutDiameter = 6.1
  HoleCutType = 0
  ModelThread = false
  Profile = -> Sketch039
  Refine = true
  Suppressed = false
  Tapered = false
  TaperedAngle = 90
  ThreadClass = 0
  ThreadDepth = 3.5
  ThreadDepthType = 0
  ThreadDirection = 0
  ThreadFit = 0
  ThreadSize = 0
  ThreadType = 0
  Threaded = false
  UseCustomThreadClearance = false
FEATURE [PartDesign::SubShapeBinder] Binder017
  BindCopyOnChange = 0
  BindMode = 0
  ClaimChildren = false
  Context = -> Body006 [Binder017.]
  Fuse = false
  MakeFace = true
  OffsetFill = false
  OffsetIntersection = false
  OffsetJoinType = 0
  OffsetOpenResult = false
  PartialLoad = false
  Refine = true
  Relative = true
  Support = -> [Body008[Pad016.Face14,Pad016.Face15,Pad016.Face16]]
  _Version = 2
FEATURE [Sketcher::SketchObject] Sketch040
  ArcFitTolerance = 1e-06
  AttachmentSupport = -> [Hole007]
  ExternalGeometry = -> [Binder017]
  FullyConstrained = true
  MakeInternals = false
  MapMode = 5
  Placement = pos=(0,-30,8.1e-15) rot=(1,0,0;1.5708rad)
  sketch-geometry (10):
    g0: LineSegment StartX=84.5 StartY=-0.3 StartZ=0 EndX=84.5 EndY=-7.3 EndZ=0
    g1: LineSegment StartX=85.5 StartY=-8.3 StartZ=0 EndX=94.5 EndY=-8.3 EndZ=0
    g2: LineSegment StartX=95.5 StartY=-7.3 StartZ=0 EndX=95.5 EndY=-0.3 EndZ=0
    g3: LineSegment StartX=94.5 StartY=0.7 StartZ=0 EndX=85.5 EndY=0.7 EndZ=0
    g4: ArcOfCircle CenterX=85.5 CenterY=-0.3 CenterZ=0 NormalX=0 NormalY=0 NormalZ=1 AngleXU=0 Radius=1 StartAngle=1.5708 EndAngle=3.14159
    g5: ArcOfCircle CenterX=85.5 CenterY=-7.3 CenterZ=0 NormalX=0 NormalY=0 NormalZ=1 AngleXU=0 Radius=1 StartAngle=3.14159 EndAngle=4.71239
    g6: ArcOfCircle CenterX=94.5 CenterY=-7.3 CenterZ=0 NormalX=0 NormalY=0 NormalZ=1 AngleXU=0 Radius=1 StartAngle=4.71239 EndAngle=6.28319
    g7: ArcOfCircle CenterX=94.5 CenterY=-0.3 CenterZ=0 NormalX=0 NormalY=0 NormalZ=1 AngleXU=0 Radius=1 StartAngle=0 EndAngle=1.5708
    g8: GeomPoint [constr] X=84.5 Y=0.7 Z=0
    g9: GeomPoint [constr] X=95.5 Y=-8.3 Z=0
  constraints (22):
    c: Tangent(g0,g4) = -1.5708
    c: Tangent(g0,g5) = -1.5708
    c: Tangent(g1,g5) = -1.5708
    c: Tangent(g1,g6) = -1.5708
    c: Tangent(g2,g6) = -1.5708
    c: Tangent(g2,g7) = -1.5708
    c: Tangent(g3,g7) = -1.5708
    c: Tangent(g3,g4) = -1.5708
    c: Vertical(g0)
    c: Vertical(g2)
    c: Horizontal(g1)
    c: Horizontal(g3)
    c: Equal(g4,g5)
    c: Equal(g5,g6)
    c: Equal(g6,g7)
    c: PointOnObject(g8,g0)
    c: PointOnObject(g8,g3)
    c: PointOnObject(g9,g1)
    c: PointOnObject(g9,g2)
    c: Radius(g5) = 1
    c: Coincident(g8,g-3)
    c: Coincident(g9,g-4)
FEATURE [PartDesign::Pocket] Pocket012  label="USBPlugCarve"
  BaseFeature = -> Hole007
  Direction = (0,1,-2e-16)
  Length = 0
  Length2 = 5
  Profile = -> Sketch040
  ReferenceAxis = -> Sketch040 [N_Axis]
  Refine = true
  Suppressed = false
  Type = 3
  UpToFace = -> Binder017 [Face3]
FEATURE [Sketcher::SketchObject] Sketch041
  ArcFitTolerance = 1e-06
  AttachmentSupport = -> [Pocket012]
  ExternalGeometry = -> [Binder017]
  FullyConstrained = true
  MakeInternals = false
  MapMode = 5
  Placement = pos=(0,-26.8,0) rot=(1,0,0;1.5708rad)
  sketch-geometry (12):
    g0: LineSegment [constr] StartX=86 StartY=-2.3 StartZ=0 EndX=86 EndY=-5.3 EndZ=0
    g1: LineSegment [constr] StartX=86 StartY=-5.3 StartZ=0 EndX=94 EndY=-5.3 EndZ=0
    g2: LineSegment [constr] StartX=94 StartY=-5.3 StartZ=0 EndX=94 EndY=-2.3 EndZ=0
    g3: LineSegment [constr] StartX=94 StartY=-2.3 StartZ=0 EndX=86 EndY=-2.3 EndZ=0
    g4: LineSegment StartX=94.3 StartY=-5.3 StartZ=0 EndX=94.3 EndY=-2.3 EndZ=0
    g5: ArcOfCircle CenterX=94 CenterY=-2.3 CenterZ=0 NormalX=0 NormalY=0 NormalZ=-1 AngleXU=0 Radius=0.3 StartAngle=1.5708 EndAngle=3.14159
    g6: LineSegment StartX=94 StartY=-2 StartZ=0 EndX=86 EndY=-2 EndZ=0
    g7: ArcOfCircle CenterX=86 CenterY=-2.3 CenterZ=0 NormalX=0 NormalY=0 NormalZ=-1 AngleXU=-1.5708 Radius=0.3 StartAngle=1.5708 EndAngle=3.14159
    g8: LineSegment StartX=85.7 StartY=-2.3 StartZ=0 EndX=85.7 EndY=-5.3 EndZ=0
    g9: ArcOfCircle CenterX=86 CenterY=-5.3 CenterZ=0 NormalX=0 NormalY=0 NormalZ=-1 AngleXU=-3.14159 Radius=0.3 StartAngle=1.5708 EndAngle=3.14159
    g10: LineSegment StartX=86 StartY=-5.6 StartZ=0 EndX=94 EndY=-5.6 EndZ=0
    g11: ArcOfCircle CenterX=94 CenterY=-5.3 CenterZ=0 NormalX=0 NormalY=0 NormalZ=-1 AngleXU=1.5708 Radius=0.3 StartAngle=1.5708 EndAngle=3.14159
  constraints (26):
    c: Coincident(g0,g1)
    c: Coincident(g1,g2)
    c: Coincident(g2,g3)
    c: Coincident(g3,g0)
    c: Vertical(g0)
    c: Vertical(g2)
    c: Horizontal(g1)
    c: Horizontal(g3)
    c: Coincident(g0,g-3)
    c: Coincident(g1,g-4)
    c: Tangent(g4,g5) = -1.5708
    c: Tangent(g4,g11) = -1.5708
    c: Tangent(g5,g6) = -1.5708
    c: Tangent(g6,g7) = -1.5708
    c: Tangent(g7,g8) = -1.5708
    c: Tangent(g8,g9) = -1.5708
    c: Tangent(g9,g10) = -1.5708
    c: Tangent(g10,g11) = -1.5708
    c: Coincident(g11,g1)
    c: Parallel(g4,g2)
    c: Coincident(g5,g3)
    c: Parallel(g6,g3)
    c: Coincident(g7,g3)
    c: Parallel(g8,g0)
    c: Coincident(g9,g0)
    c: Distance(g10,g1) = 0.3
FEATURE [PartDesign::Pocket] Pocket013  label="USBSocketCarve"
  BaseFeature = -> Pocket012
  Direction = (0,1,-2e-16)
  Length = 5
  Length2 = 5
  Profile = -> Sketch041
  ReferenceAxis = -> Sketch041 [N_Axis]
  Refine = true
  Suppressed = false
  Type = 2
FEATURE [Sketcher::SketchObject] Sketch042
  ArcFitTolerance = 1e-06
  AttachmentSupport = -> [Pocket013]
  ExternalGeometry = -> [Pocket013]
  FullyConstrained = true
  MakeInternals = false
  MapMode = 5
  Placement = pos=(100.82,0,0) rot=(0.57735,-0.57735,-0.57735;2.0944rad)
  sketch-geometry (4):
    g0: LineSegment StartX=-26 StartY=4 StartZ=0 EndX=-28 EndY=2 EndZ=0
    g1: LineSegment StartX=-28 StartY=2 StartZ=0 EndX=28 EndY=2 EndZ=0
    g2: LineSegment StartX=28 StartY=2 StartZ=0 EndX=26 EndY=4 EndZ=0
    g3: LineSegment StartX=26 StartY=4 StartZ=0 EndX=-26 EndY=4 EndZ=0
  constraints (11):
    c: Distance(g-6,g-3) = 2
    c: Coincident(g0,g-5)
    c: PointOnObject(g0,g-6)
    c: Coincident(g0,g1)
    c: PointOnObject(g1,g-6)
    c: Coincident(g1,g2)
    c: Coincident(g2,g-4)
    c: Coincident(g2,g3)
    c: Coincident(g3,g0)
    c: Angle(g1,g0) = 0.785398
    c: Equal(g0,g2)
FEATURE [PartDesign::Pocket] Pocket014  label="LidSlot"
  BaseFeature = -> Pocket013
  Direction = (1,0,0)
  Length = 0
  Length2 = 5
  Profile = -> Sketch042
  ReferenceAxis = -> Sketch042 [N_Axis]
  Refine = true
  Suppressed = false
  Type = 3
  UpToFace = -> Pocket013 [Face17]
FEATURE [PartDesign::Pocket] Pocket015  label="LidOvershoot"
  BaseFeature = -> Pocket014
  Direction = (1,0,0)
  Length = 2
  Length2 = 5
  Profile = -> Sketch042
  ReferenceAxis = -> Sketch042 [N_Axis]
  Refine = true
  Suppressed = false
  Type = 0
FEATURE [Sketcher::SketchObject] Sketch043
  ArcFitTolerance = 1e-06
  AttachmentSupport = -> [Pocket015]
  ExternalGeometry = -> [Pocket015]
  FullyConstrained = true
  MakeInternals = false
  MapMode = 5
  Placement = pos=(0,0,2) rot=(0,0,1;0rad)
  sketch-geometry (3):
    g0: Circle CenterX=62.8197 CenterY=-1.9806e-12 CenterZ=0 NormalX=0 NormalY=0 NormalZ=1 AngleXU=0 Radius=1.5
    g1: GeomPoint X=59.8197 Y=-3.9648e-12 Z=0
    g2: GeomPoint X=65.8197 Y=3.6e-15 Z=0
  constraints (4):
    c: Symmetric(g-4,g-4,g1)
    c: Symmetric(g-3,g-3,g2)
    c: Symmetric(g1,g2,g0)
    c: Diameter(g0) = 3
FEATURE [PartDesign::Hole] Hole008  label="LidScrewHole"
  BaseFeature = -> Pocket015
  CustomThreadClearance = 0
  Depth = 6
  DepthType = 0
  Diameter = 3
  DrillForDepth = false
  DrillPoint = 0
  DrillPointAngle = 118
  HoleCutCountersinkAngle = 90
  HoleCutCustomValues = false
  HoleCutDepth = 0
  HoleCutDiameter = 6.1
  HoleCutType = 0
  ModelThread = false
  Profile = -> Sketch043
  Refine = true
  Suppressed = false
  Tapered = false
  TaperedAngle = 90
  ThreadClass = 0
  ThreadDepth = 6
  ThreadDepthType = 0
  ThreadDirection = 0
  ThreadFit = 0
  ThreadSize = 0
  ThreadType = 0
  Threaded = false
  UseCustomThreadClearance = false
FEATURE [Sketcher::SketchObject] Sketch044  label="SocketPipeSection"
  ArcFitTolerance = 1e-06
  AttachmentSupport = -> [Hole008]
  ExternalGeometry = -> [Hole008]
  FullyConstrained = true
  MakeInternals = false
  MapMode = 5
  Placement = pos=(100.82,0,0) rot=(0.57735,-0.57735,-0.57735;2.0944rad)
  expr: Constraints[10] = 7.62 + 2
  expr: Constraints[11] = 2.54 + 2
  sketch-geometry (4):
    g0: LineSegment StartX=-26 StartY=-4.54 StartZ=0 EndX=-16.38 EndY=-4.54 EndZ=0
    g1: LineSegment StartX=-16.38 StartY=-4.54 StartZ=0 EndX=-16.38 EndY=0 EndZ=0
    g2: LineSegment StartX=-16.38 StartY=0 StartZ=0 EndX=-26 EndY=0 EndZ=0
    g3: LineSegment StartX=-26 StartY=0 StartZ=0 EndX=-26 EndY=-4.54 EndZ=0
  constraints (12):
    c: Coincident(g0,g1)
    c: Coincident(g1,g2)
    c: Coincident(g2,g3)
    c: Coincident(g3,g0)
    c: Horizontal(g0)
    c: Horizontal(g2)
    c: Vertical(g1)
    c: Vertical(g3)
    c: PointOnObject(g0,g-4)
    c: PointOnObject(g1,g-1)
    c: DistanceX(g0,g0) = 9.62
    c: Distance(g1,g1) = 4.54
FEATURE [Sketcher::SketchObject] Sketch045  label="SocketPipePath"
  ArcFitTolerance = 1e-06
  AttachmentSupport = -> [Hole008]
  ExternalGeometry = -> [Sketch044,Hole008]
  FullyConstrained = true
  MakeInternals = false
  MapMode = 5
  Placement = pos=(0,26,0) rot=(1,0,0;1.5708rad)
  sketch-geometry (2):
    g0: LineSegment StartX=100.82 StartY=-1.9e-15 StartZ=0 EndX=111.652 EndY=-7.42652 EndZ=0
    g1: GeomPoint [constr] X=111.652 Y=-8 Z=0
  constraints (5):
    c: Coincident(g0,g-3)
    c: PointOnObject(g1,g-5)
    c: Horizontal(g-5,g1)
    c: PointOnObject(g-5,g0)
    c: Vertical(g0,g1)
FEATURE [PartDesign::SubtractivePipe] SubtractivePipe  label="ServoCablePipe"
  AuxilleryCurvelinear = true
  AuxillerySpineTangent = false
  BaseFeature = -> Hole008
  Binormal = (0,0,0)
  Mode = 0
  Profile = -> Sketch044
  Refine = true
  Spine = -> Sketch045
  SpineTangent = false
  Suppressed = false
  Transformation = 0
  Transition = 0
FEATURE [PartDesign::SubShapeBinder] Binder018
  BindCopyOnChange = 0
  BindMode = 0
  ClaimChildren = false
  Context = -> Body009 [Binder018.]
  Fuse = false
  MakeFace = true
  OffsetFill = false
  OffsetIntersection = false
  OffsetJoinType = 0
  OffsetOpenResult = false
  PartialLoad = false
  Refine = true
  Relative = true
  Support = -> [Body006[Sketch042.]]
  _Version = 2
FEATURE [PartDesign::SubShapeBinder] Binder019
  BindCopyOnChange = 0
  BindMode = 0
  ClaimChildren = false
  Context = -> Body009 [Binder019.]
  Fuse = false
  MakeFace = true
  OffsetFill = false
  OffsetIntersection = false
  OffsetJoinType = 0
  OffsetOpenResult = false
  PartialLoad = false
  Refine = true
  Relative = true
  Support = -> [Body006[Sketch023.]]
  _Version = 2
FEATURE [Sketcher::SketchObject] Sketch046
  ArcFitTolerance = 1e-06
  AttachmentSupport = -> [Binder018]
  ExternalGeometry = -> [Binder018]
  FullyConstrained = true
  MakeInternals = false
  MapMode = 5
  Placement = pos=(100.82,0,0) rot=(0.57735,0.57735,0.57735;2.0944rad)
  sketch-geometry (4):
    g0: LineSegment StartX=-25.8 StartY=4 StartZ=0 EndX=-27.8 EndY=2 EndZ=0
    g1: LineSegment StartX=-27.8 StartY=2 StartZ=0 EndX=27.8 EndY=2 EndZ=0
    g2: LineSegment StartX=27.8 StartY=2 StartZ=0 EndX=25.8 EndY=4 EndZ=0
    g3: LineSegment StartX=25.8 StartY=4 StartZ=0 EndX=-25.8 EndY=4 EndZ=0
  constraints (11):
    c: PointOnObject(g0,g-3)
    c: PointOnObject(g0,g-5)
    c: Coincident(g0,g1)
    c: PointOnObject(g1,g-5)
    c: Coincident(g1,g2)
    c: Coincident(g2,g3)
    c: Coincident(g3,g0)
    c: Equal(g-4,g0)
    c: Equal(g-6,g2)
    c: Symmetric(g0,g2,g-2)
    c: Distance(g2,g-6) = 0.2
FEATURE [PartDesign::Pad] Pad018
  Direction = (1,0,0)
  Length = 1.9
  Length2 = 10
  Profile = -> Sketch046
  ReferenceAxis = -> Sketch046 [N_Axis]
  Refine = true
  Suppressed = false
  Type = 0
  expr: Length = <<LidOvershoot>>.Length - 0.1 mm
FEATURE [PartDesign::SubShapeBinder] Binder020
  BindCopyOnChange = 0
  BindMode = 0
  ClaimChildren = false
  Context = -> Body009 [Binder020.]
  Fuse = false
  MakeFace = true
  OffsetFill = false
  OffsetIntersection = false
  OffsetJoinType = 0
  OffsetOpenResult = false
  PartialLoad = false
  Refine = true
  Relative = true
  Support = -> [Body006[SubtractivePipe.Face17]]
  _Version = 2
FEATURE [PartDesign::Pad] Pad019
  BaseFeature = -> Pad018
  Direction = (1,0,0)
  Length = 10
  Length2 = 10
  Profile = -> Sketch046
  ReferenceAxis = -> Sketch046 [N_Axis]
  Refine = true
  Suppressed = false
  Type = 3
  UpToFace = -> SubtractivePipe [Face17]
FEATURE [Sketcher::SketchObject] Sketch049
  ArcFitTolerance = 1e-06
  AttachmentSupport = -> [XZ_Plane006]
  ExternalGeometry = -> [SubtractivePipe]
  FullyConstrained = true
  MakeInternals = false
  MapMode = 5
  Placement = pos=(0,0,0) rot=(1,0,0;1.5708rad)
  sketch-geometry (3):
    g0: LineSegment StartX=101.665 StartY=4 StartZ=0 EndX=102.82 EndY=2 EndZ=0
    g1: LineSegment StartX=102.82 StartY=2 StartZ=0 EndX=102.82 EndY=4 EndZ=0
    g2: LineSegment StartX=102.82 StartY=4 StartZ=0 EndX=101.665 EndY=4 EndZ=0
  constraints (7):
    c: Coincident(g0,g1)
    c: Coincident(g1,g2)
    c: Coincident(g2,g0)
    c: Horizontal(g2)
    c: Angle(g0,g-1) = 1.0472
    c: Coincident(g1,g-3)
    c: Coincident(g0,g-3)
FEATURE [PartDesign::Pad] Pad020  label="LidRearLip"
  BaseFeature = -> SubtractivePipe
  Direction = (0,-1,2e-16)
  Length = 10
  Length2 = 10
  Profile = -> Sketch049
  ReferenceAxis = -> Sketch049 [N_Axis]
  Refine = true
  Suppressed = false
  Type = 2
FEATURE [PartDesign::SubShapeBinder] Binder022
  BindCopyOnChange = 0
  BindMode = 0
  ClaimChildren = false
  Context = -> Body009 [Binder022.]
  Fuse = false
  MakeFace = true
  OffsetFill = false
  OffsetIntersection = false
  OffsetJoinType = 0
  OffsetOpenResult = false
  PartialLoad = false
  Refine = true
  Relative = true
  Support = -> [Body006[Sketch049.]]
  _Version = 2
FEATURE [Sketcher::SketchObject] Sketch047
  ArcFitTolerance = 1e-06
  AttachmentSupport = -> [Binder019]
  ExternalGeometry = -> [Binder019,Binder022]
  FullyConstrained = true
  MakeInternals = false
  MapMode = 5
  Placement = pos=(0,-6e-16,0) rot=(0,0.707107,0.707107;3.14159rad)
  sketch-geometry (7):
    g0: LineSegment StartX=-61.8197 StartY=4 StartZ=0 EndX=-59.8197 EndY=4 EndZ=0
    g1: LineSegment StartX=-59.8197 StartY=4 StartZ=0 EndX=-59.8197 EndY=2 EndZ=0
    g2: ArcOfCircle CenterX=-61.8197 CenterY=2 CenterZ=0 NormalX=0 NormalY=0 NormalZ=1 AngleXU=0 Radius=2 StartAngle=9.81107e-09 EndAngle=1.5708
    g3: LineSegment StartX=-102.82 StartY=2 StartZ=0 EndX=-102.82 EndY=4 EndZ=0
    g4: LineSegment StartX=-102.82 StartY=4 StartZ=0 EndX=-101.55 EndY=4 EndZ=0
    g5: LineSegment StartX=-101.55 StartY=4 StartZ=0 EndX=-102.704 EndY=2 EndZ=0
    g6: LineSegment StartX=-102.704 StartY=2 StartZ=0 EndX=-102.82 EndY=2 EndZ=0
  constraints (18):
    c: Coincident(g-3,g0)
    c: Coincident(g0,g1)
    c: Coincident(g1,g-3)
    c: Vertical(g1)
    c: Horizontal(g0)
    c: Coincident(g2,g0)
    c: Coincident(g2,g1)
    c: Tangent(g2,g-3)
    c: Coincident(g-5,g3)
    c: Coincident(g3,g-5)
    c: Coincident(g3,g4)
    c: Horizontal(g4)
    c: Coincident(g4,g5)
    c: Coincident(g5,g6)
    c: Coincident(g6,g3)
    c: Horizontal(g6)
    c: Parallel(g-4,g5)
    c: Distance(g5,g-4) = 0.1
FEATURE [PartDesign::Pocket] Pocket016
  BaseFeature = -> Pad019
  Direction = (0,-1,2e-16)
  Length = 5
  Length2 = 5
  Midplane = true
  Profile = -> Sketch047
  ReferenceAxis = -> Sketch047 [N_Axis]
  Refine = true
  Suppressed = false
  Type = 1
FEATURE [PartDesign::Mirrored] Mirrored004  label="LidRearLipReflection"
  BaseFeature = -> Pad020
  MirrorPlane = -> XZ_Plane006
  Originals = -> [Pad020]
  Refine = true
  Suppressed = false
  TransformMode = 0
FEATURE [PartDesign::SubShapeBinder] Binder023
  BindCopyOnChange = 0
  BindMode = 0
  ClaimChildren = false
  Context = -> Body009 [Binder023.]
  Fuse = false
  MakeFace = true
  OffsetFill = false
  OffsetIntersection = false
  OffsetJoinType = 0
  OffsetOpenResult = false
  PartialLoad = false
  Refine = true
  Relative = true
  Support = -> [Body006[Sketch043.]]
  _Version = 2
FEATURE [Sketcher::SketchObject] Sketch048
  ArcFitTolerance = 1e-06
  AttachmentSupport = -> [Pocket016]
  ExternalGeometry = -> [Binder023]
  FullyConstrained = true
  MakeInternals = false
  MapMode = 5
  Placement = pos=(0,0,4) rot=(0,0,1;0rad)
  sketch-geometry (1):
    g0: Circle CenterX=62.8197 CenterY=0 CenterZ=0 NormalX=0 NormalY=0 NormalZ=1 AngleXU=0 Radius=1.5
  constraints (2):
    c: Coincident(g0,g-3)
    c: Equal(g0,g-3)
FEATURE [PartDesign::Hole] Hole009
  BaseFeature = -> Pocket016
  CustomThreadClearance = 0
  Depth = 141.896
  DepthType = 1
  Diameter = 2.4
  DrillForDepth = false
  DrillPoint = 1
  DrillPointAngle = 118
  HoleCutCountersinkAngle = 90
  HoleCutCustomValues = false
  HoleCutDepth = 1
  HoleCutDiameter = 4
  HoleCutType = 1
  ModelThread = false
  Profile = -> Sketch048
  Refine = true
  Suppressed = false
  Tapered = false
  TaperedAngle = 90
  ThreadClass = 0
  ThreadDepth = 141.896
  ThreadDepthType = 0
  ThreadDirection = 0
  ThreadFit = 0
  ThreadSize = 6
  ThreadType = 1
  Threaded = false
  UseCustomThreadClearance = false
FEATURE [PartDesign::Body] Body009  label="ElectronicsLid"
  AllowCompound = false
  Group = -> [Binder018,Binder019,Sketch046,Pad018,Binder020,Pad019,Sketch047,Pocket016,Sketch048,Hole009,Binder022,Binder023]
  Origin = -> Origin010
  Tip = -> Hole009
FEATURE [PartDesign::Hole] Hole010
  BaseFeature = -> Pad004
  CustomThreadClearance = 0
  Depth = 367.842
  DepthType = 1
  Diameter = 3.4
  DrillForDepth = false
  DrillPoint = 1
  DrillPointAngle = 118
  HoleCutCountersinkAngle = 90
  HoleCutCustomValues = false
  HoleCutDepth = 2.5
  HoleCutDiameter = 6.1
  HoleCutType = 1
  ModelThread = false
  Placement = pos=(0,0,0) rot=(1,0,0;1.5708rad)
  Profile = -> Sketch010
  Refine = true
  Suppressed = false
  Tapered = false
  TaperedAngle = 90
  ThreadClass = 0
  ThreadDepth = 367.842
  ThreadDepthType = 0
  ThreadDirection = 0
  ThreadFit = 0
  ThreadSize = 9
  ThreadType = 1
  Threaded = false
  UseCustomThreadClearance = false
FEATURE [Sketcher::SketchObject] Sketch052  label="Tram"
  ArcFitTolerance = 1e-06
  AttachmentOffset = pos=(-3,0,0) rot=(0,0,1;1.5708rad)
  AttachmentSupport = -> [Hole010]
  FullyConstrained = false
  MakeInternals = false
  MapMode = 5
  Placement = pos=(-16.5,0,3) rot=(0.57735,-0.57735,-0.57735;2.0944rad)
  sketch-geometry (102):
    g0: BSplineCurve PolesCount=4 KnotsCount=2 Degree=3 IsPeriodic=0
    g1: BSplineCurve PolesCount=4 KnotsCount=2 Degree=3 IsPeriodic=0
    g2: BSplineCurve PolesCount=4 KnotsCount=2 Degree=3 IsPeriodic=0
    g3: BSplineCurve PolesCount=2 KnotsCount=2 Degree=1 IsPeriodic=0
    g4: BSplineCurve PolesCount=2 KnotsCount=2 Degree=1 IsPeriodic=0
    g5: BSplineCurve PolesCount=2 KnotsCount=2 Degree=1 IsPeriodic=0
    g6: BSplineCurve PolesCount=2 KnotsCount=2 Degree=1 IsPeriodic=0
    g7: BSplineCurve PolesCount=2 KnotsCount=2 Degree=1 IsPeriodic=0
    g8: BSplineCurve PolesCount=4 KnotsCount=2 Degree=3 IsPeriodic=0
    g9: BSplineCurve PolesCount=4 KnotsCount=2 Degree=3 IsPeriodic=0
    g10: BSplineCurve PolesCount=2 KnotsCount=2 Degree=1 IsPeriodic=0
    g11: BSplineCurve PolesCount=4 KnotsCount=2 Degree=3 IsPeriodic=0
    g12: BSplineCurve PolesCount=4 KnotsCount=2 Degree=3 IsPeriodic=0
    g13: BSplineCurve PolesCount=2 KnotsCount=2 Degree=1 IsPeriodic=0
    g14: BSplineCurve PolesCount=2 KnotsCount=2 Degree=1 IsPeriodic=0
    g15: BSplineCurve PolesCount=4 KnotsCount=2 Degree=3 IsPeriodic=0
    g16: BSplineCurve PolesCount=4 KnotsCount=2 Degree=3 IsPeriodic=0
    g17: BSplineCurve PolesCount=2 KnotsCount=2 Degree=1 IsPeriodic=0
    g18: BSplineCurve PolesCount=4 KnotsCount=2 Degree=3 IsPeriodic=0
    g19: BSplineCurve PolesCount=4 KnotsCount=2 Degree=3 IsPeriodic=0
    g20: BSplineCurve PolesCount=2 KnotsCount=2 Degree=1 IsPeriodic=0
    g21: BSplineCurve PolesCount=2 KnotsCount=2 Degree=1 IsPeriodic=0
    g22: BSplineCurve PolesCount=2 KnotsCount=2 Degree=1 IsPeriodic=0
    g23: BSplineCurve PolesCount=2 KnotsCount=2 Degree=1 IsPeriodic=0
    g24: BSplineCurve PolesCount=2 KnotsCount=2 Degree=1 IsPeriodic=0
    g25: BSplineCurve PolesCount=2 KnotsCount=2 Degree=1 IsPeriodic=0
    g26: BSplineCurve PolesCount=2 KnotsCount=2 Degree=1 IsPeriodic=0
    g27: BSplineCurve PolesCount=2 KnotsCount=2 Degree=1 IsPeriodic=0
    g28: BSplineCurve PolesCount=2 KnotsCount=2 Degree=1 IsPeriodic=0
    g29: BSplineCurve PolesCount=4 KnotsCount=2 Degree=3 IsPeriodic=0
    g30: BSplineCurve PolesCount=4 KnotsCount=2 Degree=3 IsPeriodic=0
    g31: BSplineCurve PolesCount=2 KnotsCount=2 Degree=1 IsPeriodic=0
    g32: BSplineCurve PolesCount=4 KnotsCount=2 Degree=3 IsPeriodic=0
    g33: BSplineCurve PolesCount=4 KnotsCount=2 Degree=3 IsPeriodic=0
    g34: BSplineCurve PolesCount=2 KnotsCount=2 Degree=1 IsPeriodic=0
    g35: BSplineCurve PolesCount=2 KnotsCount=2 Degree=1 IsPeriodic=0
    g36: BSplineCurve PolesCount=4 KnotsCount=2 Degree=3 IsPeriodic=0
    g37: BSplineCurve PolesCount=4 KnotsCount=2 Degree=3 IsPeriodic=0
    g38: BSplineCurve PolesCount=2 KnotsCount=2 Degree=1 IsPeriodic=0
    g39: BSplineCurve PolesCount=4 KnotsCount=2 Degree=3 IsPeriodic=0
    g40: BSplineCurve PolesCount=4 KnotsCount=2 Degree=3 IsPeriodic=0
    g41: BSplineCurve PolesCount=2 KnotsCount=2 Degree=1 IsPeriodic=0
    g42: BSplineCurve PolesCount=2 KnotsCount=2 Degree=1 IsPeriodic=0
    g43: BSplineCurve PolesCount=2 KnotsCount=2 Degree=1 IsPeriodic=0
    g44: BSplineCurve PolesCount=2 KnotsCount=2 Degree=1 IsPeriodic=0
    g45: BSplineCurve PolesCount=2 KnotsCount=2 Degree=1 IsPeriodic=0
    g46: BSplineCurve PolesCount=4 KnotsCount=2 Degree=3 IsPeriodic=0
    g47: BSplineCurve PolesCount=4 KnotsCount=2 Degree=3 IsPeriodic=0
    g48: BSplineCurve PolesCount=4 KnotsCount=2 Degree=3 IsPeriodic=0
    g49: BSplineCurve PolesCount=4 KnotsCount=2 Degree=3 IsPeriodic=0
    g50: BSplineCurve PolesCount=4 KnotsCount=2 Degree=3 IsPeriodic=0
    g51: BSplineCurve PolesCount=2 KnotsCount=2 Degree=1 IsPeriodic=0
    g52: BSplineCurve PolesCount=4 KnotsCount=2 Degree=3 IsPeriodic=0
    g53: BSplineCurve PolesCount=2 KnotsCount=2 Degree=1 IsPeriodic=0
    g54: BSplineCurve PolesCount=4 KnotsCount=2 Degree=3 IsPeriodic=0
    g55: BSplineCurve PolesCount=2 KnotsCount=2 Degree=1 IsPeriodic=0
    g56: BSplineCurve PolesCount=2 KnotsCount=2 Degree=1 IsPeriodic=0
    g57: BSplineCurve PolesCount=2 KnotsCount=2 Degree=1 IsPeriodic=0
    g58: BSplineCurve PolesCount=2 KnotsCount=2 Degree=1 IsPeriodic=0
    g59: BSplineCurve PolesCount=2 KnotsCount=2 Degree=1 IsPeriodic=0
    g60: BSplineCurve PolesCount=2 KnotsCount=2 Degree=1 IsPeriodic=0
    g61: BSplineCurve PolesCount=2 KnotsCount=2 Degree=1 IsPeriodic=0
    g62: BSplineCurve PolesCount=2 KnotsCount=2 Degree=1 IsPeriodic=0
    g63: BSplineCurve PolesCount=2 KnotsCount=2 Degree=1 IsPeriodic=0
    g64: BSplineCurve PolesCount=4 KnotsCount=2 Degree=3 IsPeriodic=0
    g65: BSplineCurve PolesCount=2 KnotsCount=2 Degree=1 IsPeriodic=0
    g66: BSplineCurve PolesCount=4 KnotsCount=2 Degree=3 IsPeriodic=0
    g67: BSplineCurve PolesCount=2 KnotsCount=2 Degree=1 IsPeriodic=0
    g68: BSplineCurve PolesCount=4 KnotsCount=2 Degree=3 IsPeriodic=0
    g69: BSplineCurve PolesCount=4 KnotsCount=2 Degree=3 IsPeriodic=0
    g70: BSplineCurve PolesCount=7 KnotsCount=4 Degree=2 IsPeriodic=0
    g71: BSplineCurve PolesCount=7 KnotsCount=4 Degree=2 IsPeriodic=0
    g72: BSplineCurve PolesCount=7 KnotsCount=4 Degree=2 IsPeriodic=0
    g73: BSplineCurve PolesCount=7 KnotsCount=4 Degree=2 IsPeriodic=0
    g74: BSplineCurve PolesCount=2 KnotsCount=2 Degree=1 IsPeriodic=0
    g75: BSplineCurve PolesCount=2 KnotsCount=2 Degree=1 IsPeriodic=0
    g76: BSplineCurve PolesCount=2 KnotsCount=2 Degree=1 IsPeriodic=0
    g77: BSplineCurve PolesCount=2 KnotsCount=2 Degree=1 IsPeriodic=0
    g78: BSplineCurve PolesCount=2 KnotsCount=2 Degree=1 IsPeriodic=0
    g79: BSplineCurve PolesCount=2 KnotsCount=2 Degree=1 IsPeriodic=0
    g80: BSplineCurve PolesCount=2 KnotsCount=2 Degree=1 IsPeriodic=0
    g81: BSplineCurve PolesCount=2 KnotsCount=2 Degree=1 IsPeriodic=0
    g82: BSplineCurve PolesCount=2 KnotsCount=2 Degree=1 IsPeriodic=0
    g83: BSplineCurve PolesCount=2 KnotsCount=2 Degree=1 IsPeriodic=0
    g84: BSplineCurve PolesCount=2 KnotsCount=2 Degree=1 IsPeriodic=0
    g85: BSplineCurve PolesCount=2 KnotsCount=2 Degree=1 IsPeriodic=0
    g86: BSplineCurve PolesCount=2 KnotsCount=2 Degree=1 IsPeriodic=0
    g87: BSplineCurve PolesCount=2 KnotsCount=2 Degree=1 IsPeriodic=0
    g88: BSplineCurve PolesCount=2 KnotsCount=2 Degree=1 IsPeriodic=0
    g89: BSplineCurve PolesCount=2 KnotsCount=2 Degree=1 IsPeriodic=0
    g90: BSplineCurve PolesCount=2 KnotsCount=2 Degree=1 IsPeriodic=0
    g91: BSplineCurve PolesCount=2 KnotsCount=2 Degree=1 IsPeriodic=0
    g92: BSplineCurve PolesCount=2 KnotsCount=2 Degree=1 IsPeriodic=0
    g93: BSplineCurve PolesCount=2 KnotsCount=2 Degree=1 IsPeriodic=0
    g94: BSplineCurve PolesCount=2 KnotsCount=2 Degree=1 IsPeriodic=0
    g95: BSplineCurve PolesCount=2 KnotsCount=2 Degree=1 IsPeriodic=0
    g96: BSplineCurve PolesCount=2 KnotsCount=2 Degree=1 IsPeriodic=0
    g97: BSplineCurve PolesCount=2 KnotsCount=2 Degree=1 IsPeriodic=0
    g98: BSplineCurve PolesCount=2 KnotsCount=2 Degree=1 IsPeriodic=0
    g99: BSplineCurve PolesCount=2 KnotsCount=2 Degree=1 IsPeriodic=0
    g100: BSplineCurve PolesCount=2 KnotsCount=2 Degree=1 IsPeriodic=0
    g101: BSplineCurve PolesCount=2 KnotsCount=2 Degree=1 IsPeriodic=0
  constraints (92):
    c: Coincident(g0,g1)
    c: Coincident(g1,g2)
    c: Coincident(g2,g3)
    c: Coincident(g3,g4)
    c: Coincident(g4,g5)
    c: Coincident(g5,g6)
    c: Coincident(g6,g7)
    c: Coincident(g7,g8)
    c: Coincident(g8,g9)
    c: Coincident(g9,g10)
    c: Coincident(g10,g11)
    c: Coincident(g11,g12)
    c: Coincident(g12,g13)
    c: Coincident(g13,g14)
    c: Coincident(g14,g15)
    c: Coincident(g15,g16)
    c: Coincident(g16,g17)
    c: Coincident(g17,g18)
    c: Coincident(g18,g19)
    c: Coincident(g19,g20)
    c: Coincident(g20,g21)
    c: Coincident(g21,g22)
    c: Coincident(g22,g23)
    c: Coincident(g23,g24)
    c: Coincident(g24,g25)
    c: Coincident(g25,g26)
    c: Coincident(g26,g27)
    c: Coincident(g27,g28)
    c: Coincident(g28,g29)
    c: Coincident(g29,g30)
    c: Coincident(g30,g31)
    c: Coincident(g31,g32)
    c: Coincident(g32,g33)
    c: Coincident(g33,g34)
    c: Coincident(g34,g35)
    c: Coincident(g35,g36)
    c: Coincident(g36,g37)
    c: Coincident(g37,g38)
    c: Coincident(g38,g39)
    c: Coincident(g39,g40)
    c: Coincident(g40,g41)
    c: Coincident(g41,g42)
    c: Coincident(g42,g43)
    c: Coincident(g43,g44)
    c: Coincident(g44,g45)
    c: Coincident(g45,g46)
    c: Coincident(g46,g47)
    c: Coincident(g47,g48)
    c: Coincident(g48,g49)
    c: Coincident(g49,g50)
    c: Coincident(g50,g51)
    c: Coincident(g51,g52)
    c: Coincident(g52,g53)
    c: Coincident(g53,g54)
    c: Coincident(g54,g55)
    c: Coincident(g55,g56)
    c: Coincident(g56,g57)
    c: Coincident(g57,g58)
    c: Coincident(g58,g59)
    c: Coincident(g59,g60)
    c: Coincident(g60,g61)
    c: Coincident(g61,g62)
    c: Coincident(g62,g63)
    c: Coincident(g63,g64)
    c: Coincident(g64,g65)
    c: Coincident(g65,g66)
    c: Coincident(g66,g67)
    c: Coincident(g67,g68)
    c: Coincident(g68,g69)
    c: Coincident(g69,g0)
    c: Coincident(g78,g79)
    c: Coincident(g79,g80)
    c: Coincident(g80,g81)
    c: Coincident(g81,g82)
    c: Coincident(g82,g83)
    c: Coincident(g83,g84)
    c: Coincident(g84,g85)
    c: Coincident(g85,g86)
    c: Coincident(g86,g87)
    c: Coincident(g87,g88)
    c: Coincident(g88,g89)
    c: Coincident(g90,g91)
    c: Coincident(g91,g92)
    c: Coincident(g92,g93)
    c: Coincident(g93,g94)
    c: Coincident(g94,g95)
    c: Coincident(g95,g96)
    c: Coincident(g96,g97)
    c: Coincident(g97,g98)
    c: Coincident(g98,g99)
    c: Coincident(g99,g100)
    c: Coincident(g100,g101)
FEATURE [Sketcher::SketchObject] Sketch053
  ArcFitTolerance = 1e-06
  AttachmentSupport = -> [Hole010]
  ExternalGeometry = -> [Sketch052]
  FullyConstrained = true
  MakeInternals = false
  MapMode = 5
  Placement = pos=(-16.5,0,0) rot=(0.707107,0,-0.707107;3.14159rad)
  sketch-geometry (4):
    g0: Circle CenterX=-1.15 CenterY=77.0838 CenterZ=0 NormalX=0 NormalY=0 NormalZ=1 AngleXU=0 Radius=1.75
    g1: Circle CenterX=-1.15 CenterY=35.6538 CenterZ=0 NormalX=0 NormalY=0 NormalZ=1 AngleXU=0 Radius=1.75
    g2: Circle CenterX=-1.15 CenterY=-35.5538 CenterZ=0 NormalX=0 NormalY=0 NormalZ=1 AngleXU=0 Radius=1.75
    g3: Circle CenterX=-1.15 CenterY=-76.9519 CenterZ=0 NormalX=0 NormalY=0 NormalZ=1 AngleXU=0 Radius=1.75
  constraints (8):
    c: Coincident(g0,g-3)
    c: PointOnObject(g-3,g0)
    c: Coincident(g1,g-4)
    c: PointOnObject(g-4,g1)
    c: Coincident(g2,g-5)
    c: PointOnObject(g-5,g2)
    c: Coincident(g3,g-6)
    c: PointOnObject(g-6,g3)
FEATURE [PartDesign::Hole] Hole011
  BaseFeature = -> Hole010
  CustomThreadClearance = 0
  Depth = 367.043
  DepthType = 1
  Diameter = 3.4
  DrillForDepth = false
  DrillPoint = 1
  DrillPointAngle = 118
  HoleCutCountersinkAngle = 90
  HoleCutCustomValues = false
  HoleCutDepth = 0
  HoleCutDiameter = 6.1
  HoleCutType = 0
  ModelThread = false
  Placement = pos=(0,0,0) rot=(1,0,0;1.5708rad)
  Profile = -> Sketch053
  Refine = true
  Suppressed = false
  Tapered = false
  TaperedAngle = 90
  ThreadClass = 0
  ThreadDepth = 367.043
  ThreadDepthType = 0
  ThreadDirection = 0
  ThreadFit = 0
  ThreadSize = 9
  ThreadType = 1
  Threaded = false
  UseCustomThreadClearance = false
FEATURE [PartDesign::Fillet] Fillet003
  Base = -> Hole011 [Edge9,Edge8]
  BaseFeature = -> Hole011
  Placement = pos=(0,0,0) rot=(1,0,0;1.5708rad)
  Radius = 7
  Refine = true
  SupportTransform = false
  Suppressed = false
  UseAllEdges = false
FEATURE [Sketcher::SketchObject] Sketch054
  ArcFitTolerance = 1e-06
  AttachmentSupport = -> [Fillet003]
  ExternalGeometry = -> [Fillet003,Sketch052]
  FullyConstrained = true
  MakeInternals = false
  MapMode = 5
  Placement = pos=(-16.5,0,0) rot=(0.707107,0,-0.707107;3.14159rad)
  sketch-geometry (14):
    g0: ArcOfCircle CenterX=-1.15 CenterY=77.0838 CenterZ=0 NormalX=0 NormalY=0 NormalZ=1 AngleXU=0 Radius=5.98816 StartAngle=4.93602 EndAngle=7.63036
    g1: LineSegment StartX=6 StartY=90 StartZ=0 EndX=0.17798 EndY=90 EndZ=0
    g2: LineSegment StartX=0.17798 StartY=90 StartZ=0 EndX=0.17798 EndY=82.9228 EndZ=0
    g3: GeomPoint X=0.67798 Y=90 Z=0
    g4: GeomPoint X=4.83816 Y=77.0838 Z=0
    g5: LineSegment StartX=0.17798 StartY=71.2447 StartZ=0 EndX=0.17798 EndY=41.4928 EndZ=0
    g6: ArcOfCircle CenterX=-1.15 CenterY=35.6538 CenterZ=0 NormalX=0 NormalY=0 NormalZ=1 AngleXU=0 Radius=5.98816 StartAngle=4.93602 EndAngle=7.63036
    g7: ArcOfCircle CenterX=-1.15 CenterY=-35.5538 CenterZ=0 NormalX=0 NormalY=0 NormalZ=1 AngleXU=0 Radius=5.98816 StartAngle=4.93602 EndAngle=7.63036
    g8: ArcOfCircle CenterX=-1.15 CenterY=-76.9519 CenterZ=0 NormalX=0 NormalY=0 NormalZ=1 AngleXU=0 Radius=5.98816 StartAngle=4.93602 EndAngle=7.63036
    g9: LineSegment StartX=0.17798 StartY=29.8147 StartZ=0 EndX=0.17798 EndY=-29.7147 EndZ=0
    g10: LineSegment StartX=0.17798 StartY=-41.3928 StartZ=0 EndX=0.17798 EndY=-71.1129 EndZ=0
    g11: LineSegment StartX=0.17798 StartY=-82.791 StartZ=0 EndX=0.17798 EndY=-90 EndZ=0
    g12: LineSegment StartX=0.17798 StartY=-90 StartZ=0 EndX=6 EndY=-90 EndZ=0
    g13: LineSegment StartX=6 StartY=-90 StartZ=0 EndX=6 EndY=90 EndZ=0
  constraints (38):
    c: Coincident(g0,g-13)
    c: Coincident(g-3,g1)
    c: PointOnObject(g1,g-3)
    c: Coincident(g1,g2)
    c: Vertical(g2)
    c: Coincident(g2,g0)
    c: PointOnObject(g3,g1)
    c: PointOnObject(g3,g-4)
    c: Distance(g1,g3) = 0.5
    c: PointOnObject(g4,g0)
    c: Horizontal(g0,g4)
    c: Distance(g4,g-14) = 0.5
    c: Coincident(g5,g0)
    c: Vertical(g5)
    c: Vertical(g0,g0)
    c: Coincident(g6,g-11)
    c: Coincident(g7,g-9)
    c: Coincident(g8,g-10)
    c: Coincident(g6,g5)
    c: Equal(g6,g0)
    c: Vertical(g5,g6)
    c: Coincident(g9,g6)
    c: Coincident(g9,g7)
    c: Vertical(g9)
    c: Equal(g7,g6)
    c: Vertical(g7,g7)
    c: Coincident(g10,g7)
    c: Coincident(g10,g8)
    c: Vertical(g10)
    c: Vertical(g8,g8)
    c: Equal(g8,g7)
    c: Coincident(g11,g8)
    c: PointOnObject(g11,g-5)
    c: Vertical(g11)
    c: Coincident(g12,g11)
    c: Coincident(g12,g-5)
    c: Coincident(g13,g12)
    c: Coincident(g13,g1)
FEATURE [PartDesign::Pocket] Pocket  label="TrimOffBelowWheels"
  BaseFeature = -> Fillet003
  Direction = (1,0,2e-16)
  Length = 5
  Length2 = 5
  Placement = pos=(0,0,0) rot=(1,0,0;1.5708rad)
  Profile = -> Sketch054
  ReferenceAxis = -> Sketch054 [N_Axis]
  Refine = true
  Suppressed = false
  Type = 1
FEATURE [PartDesign::FeatureBase] Clone
  BaseFeature = -> Mirrored
  Placement = pos=(0,0,0) rot=(1,0,0;1.5708rad)
  Suppressed = false
FEATURE [Sketcher::SketchObject] Sketch056
  ArcFitTolerance = 1e-06
  AttachmentSupport = -> [XZ_Plane012]
  FullyConstrained = true
  MakeInternals = false
  MapMode = 5
  Placement = pos=(0,0,0) rot=(1,0,0;1.5708rad)
  sketch-geometry (10):
    g0: LineSegment StartX=-1.7 StartY=-5.97022 StartZ=0 EndX=-2.9 EndY=-6.52978 EndZ=0
    g1: LineSegment StartX=-2.9 StartY=-6.52978 StartZ=0 EndX=-2.9 EndY=-9.02978 EndZ=0
    g2: LineSegment StartX=-2.9 StartY=-9.02978 StartZ=0 EndX=-1.7 EndY=-9.02978 EndZ=0
    g3: LineSegment StartX=1.7 StartY=-9.02978 StartZ=0 EndX=2.9 EndY=-9.02978 EndZ=0
    g4: LineSegment StartX=2.9 StartY=-9.02978 StartZ=0 EndX=2.9 EndY=-6.52978 EndZ=0
    g5: LineSegment StartX=2.9 StartY=-6.52978 StartZ=0 EndX=1.7 EndY=-5.97022 EndZ=0
    g6: LineSegment StartX=1.7 StartY=-5.97022 StartZ=0 EndX=-1.7 EndY=-5.97022 EndZ=0
    g7: LineSegment StartX=-1.7 StartY=-9.02978 StartZ=0 EndX=1.7 EndY=-9.02978 EndZ=0
    g8: LineSegment [constr] StartX=1.7 StartY=-5.97022 StartZ=0 EndX=1.7 EndY=-4 EndZ=0
    g9: LineSegment [constr] StartX=1.7 StartY=-9.02978 StartZ=0 EndX=1.7 EndY=-11 EndZ=0
  constraints (28):
    c: PointOnObject(g0,g-3)
    c: Coincident(g0,g1)
    c: Vertical(g1)
    c: Coincident(g1,g2)
    c: Horizontal(g2)
    c: PointOnObject(g2,g-3)
    c: PointOnObject(g3,g-4)
    c: Horizontal(g3)
    c: Coincident(g3,g4)
    c: Vertical(g4)
    c: Coincident(g4,g5)
    c: PointOnObject(g5,g-4)
    c: Coincident(g5,g6)
    c: Coincident(g6,g0)
    c: Horizontal(g6)
    c: Horizontal(g2,g3)
    c: Equal(g1,g4)
    c: Equal(g0,g5)
    c: Angle(g-4,g5) = 1.13446
    c: DistanceY(g1,g1) = 2.5
    c: Distance(g4,g1) = 5.8
    c: Coincident(g7,g2)
    c: Coincident(g7,g3)
    c: Coincident(g8,g5)
    c: Coincident(g8,g-4)
    c: Coincident(g9,g3)
    c: Coincident(g9,g-4)
    c: Equal(g9,g8)
FEATURE [PartDesign::SubShapeBinder] Binder024  label="CarriageBinder"
  BindCopyOnChange = 0
  BindMode = 0
  ClaimChildren = false
  Context = -> Body011 [Binder024.]
  Fuse = false
  MakeFace = true
  OffsetFill = false
  OffsetIntersection = false
  OffsetJoinType = 0
  OffsetOpenResult = false
  PartialLoad = false
  Refine = true
  Relative = true
  Support = -> [Body003[Pocket.Face11]]
  _Version = 2
FEATURE [PartDesign::SubShapeBinder] Binder025  label="TramBinder"
  BindCopyOnChange = 0
  BindMode = 0
  ClaimChildren = false
  Context = -> Body011 [Binder025.]
  Fuse = false
  MakeFace = true
  OffsetFill = false
  OffsetIntersection = false
  OffsetJoinType = 0
  OffsetOpenResult = false
  PartialLoad = false
  Placement = pos=(0,-217,0) rot=(0,0,1;0rad)
  Refine = true
  Relative = true
  Support = -> [Body003[Sketch052.]]
  _Version = 2
FEATURE [Sketcher::SketchObject] Sketch057  label="CountdownShapeBack"
  ArcFitTolerance = 1e-06
  AttachmentOffset = pos=(0,0,13) rot=(0,0,1;0rad)
  AttachmentSupport = -> [Binder024]
  ExternalGeometry = -> [Binder025]
  FullyConstrained = true
  MakeInternals = false
  MapMode = 5
  Placement = pos=(-29.5,0,0) rot=(0.57735,-0.57735,-0.57735;2.0944rad)
  sketch-geometry (5):
    g0: LineSegment StartX=-72.6664 StartY=12.9462 StartZ=0 EndX=-72.6664 EndY=-7.05384 EndZ=0
    g1: LineSegment StartX=-72.6664 StartY=-7.05384 StartZ=0 EndX=507.334 EndY=-7.05384 EndZ=0
    g2: LineSegment StartX=507.334 StartY=-7.05384 StartZ=0 EndX=507.334 EndY=12.9462 EndZ=0
    g3: LineSegment StartX=507.334 StartY=12.9462 StartZ=0 EndX=-72.6664 EndY=12.9462 EndZ=0
    g4: Circle CenterX=-67.6664 CenterY=-2.05384 CenterZ=0 NormalX=0 NormalY=0 NormalZ=1 AngleXU=0 Radius=1.7
  constraints (15):
    c: Coincident(g0,g1)
    c: Coincident(g1,g2)
    c: Coincident(g2,g3)
    c: Coincident(g3,g0)
    c: Vertical(g0)
    c: Vertical(g2)
    c: Horizontal(g1)
    c: Horizontal(g3)
    c: Distance(g0,g0) = 20
    c: DistanceX(g3,g3) = 580
    c: PointOnObject(g-3,g3)
    c: PointOnObject(g-4,g0)
    c: Diameter(g4) = 3.4
    c: Distance(g4,g0) = 5
    c: Distance(g4,g1) = 5
FEATURE [Sketcher::SketchObject] Sketch064
  ArcFitTolerance = 1e-06
  AttachmentSupport = -> [Pocket]
  ExternalGeometry = -> [Pocket]
  FullyConstrained = true
  MakeInternals = false
  MapMode = 5
  Placement = pos=(-13.5,0,0) rot=(0.707107,0,0.707107;3.14159rad)
  sketch-geometry (28):
    g0: LineSegment StartX=4.6141 StartY=77.0838 StartZ=0 EndX=2.88205 EndY=80.0838 EndZ=0
    g1: LineSegment StartX=2.88205 StartY=80.0838 StartZ=0 EndX=-0.582053 EndY=80.0838 EndZ=0
    g2: LineSegment StartX=-0.582053 StartY=80.0838 StartZ=0 EndX=-2.3141 EndY=77.0838 EndZ=0
    g3: LineSegment StartX=-2.3141 StartY=77.0838 StartZ=0 EndX=-0.582053 EndY=74.0838 EndZ=0
    g4: LineSegment StartX=-0.582053 StartY=74.0838 StartZ=0 EndX=2.88205 EndY=74.0838 EndZ=0
    g5: LineSegment StartX=2.88205 StartY=74.0838 StartZ=0 EndX=4.6141 EndY=77.0838 EndZ=0
    g6: Circle [constr] CenterX=1.15 CenterY=77.0838 CenterZ=0 NormalX=0 NormalY=0 NormalZ=1 AngleXU=0 Radius=3.4641
    g7: LineSegment StartX=4.6141 StartY=35.6538 StartZ=0 EndX=2.88205 EndY=38.6538 EndZ=0
    g8: LineSegment StartX=2.88205 StartY=38.6538 StartZ=0 EndX=-0.582053 EndY=38.6538 EndZ=0
    g9: LineSegment StartX=-0.582053 StartY=38.6538 StartZ=0 EndX=-2.3141 EndY=35.6538 EndZ=0
    g10: LineSegment StartX=-2.3141 StartY=35.6538 StartZ=0 EndX=-0.582053 EndY=32.6538 EndZ=0
    g11: LineSegment StartX=-0.582053 StartY=32.6538 StartZ=0 EndX=2.88205 EndY=32.6538 EndZ=0
    g12: LineSegment StartX=2.88205 StartY=32.6538 StartZ=0 EndX=4.6141 EndY=35.6538 EndZ=0
    g13: Circle [constr] CenterX=1.15 CenterY=35.6538 CenterZ=0 NormalX=0 NormalY=0 NormalZ=1 AngleXU=0 Radius=3.4641
    g14: LineSegment StartX=4.6141 StartY=-35.5538 StartZ=0 EndX=2.88205 EndY=-32.5538 EndZ=0
    g15: LineSegment StartX=2.88205 StartY=-32.5538 StartZ=0 EndX=-0.582053 EndY=-32.5538 EndZ=0
    g16: LineSegment StartX=-0.582053 StartY=-32.5538 StartZ=0 EndX=-2.3141 EndY=-35.5538 EndZ=0
    g17: LineSegment StartX=-2.3141 StartY=-35.5538 StartZ=0 EndX=-0.582053 EndY=-38.5538 EndZ=0
    g18: LineSegment StartX=-0.582053 StartY=-38.5538 StartZ=0 EndX=2.88205 EndY=-38.5538 EndZ=0
    g19: LineSegment StartX=2.88205 StartY=-38.5538 StartZ=0 EndX=4.6141 EndY=-35.5538 EndZ=0
    g20: Circle [constr] CenterX=1.15 CenterY=-35.5538 CenterZ=0 NormalX=0 NormalY=0 NormalZ=1 AngleXU=0 Radius=3.4641
    g21: LineSegment StartX=4.6141 StartY=-76.9519 StartZ=0 EndX=2.88205 EndY=-73.9519 EndZ=0
    g22: LineSegment StartX=2.88205 StartY=-73.9519 StartZ=0 EndX=-0.582053 EndY=-73.9519 EndZ=0
    g23: LineSegment StartX=-0.582053 StartY=-73.9519 StartZ=0 EndX=-2.3141 EndY=-76.9519 EndZ=0
    g24: LineSegment StartX=-2.3141 StartY=-76.9519 StartZ=0 EndX=-0.582053 EndY=-79.9519 EndZ=0
    g25: LineSegment StartX=-0.582053 StartY=-79.9519 StartZ=0 EndX=2.88205 EndY=-79.9519 EndZ=0
    g26: LineSegment StartX=2.88205 StartY=-79.9519 StartZ=0 EndX=4.6141 EndY=-76.9519 EndZ=0
    g27: Circle [constr] CenterX=1.15 CenterY=-76.9519 CenterZ=0 NormalX=0 NormalY=0 NormalZ=1 AngleXU=0 Radius=3.4641
  constraints (64):
    c: Coincident(g0,g1)
    c: Coincident(g1,g2)
    c: Coincident(g2,g3)
    c: Coincident(g3,g4)
    c: Coincident(g4,g5)
    c: Coincident(g5,g0)
    c: Equal(g0, g1-g5) x5
    c: PointOnObject(g0,g6)
    c: PointOnObject(g1,g6)
    c: PointOnObject(g2,g6)
    c: PointOnObject(g3,g6)
    c: PointOnObject(g4,g6)
    c: PointOnObject(g5,g6)
    c: Coincident(g6,g-3)
    c: Horizontal(g1)
    c: Distance(g4,g1) = 6
    c: Coincident(g7,g8)
    c: Coincident(g8,g9)
    c: Coincident(g9,g10)
    c: Coincident(g10,g11)
    c: Coincident(g11,g12)
    c: Coincident(g12,g7)
    c: Equal(g7, g8-g12) x5
    c: PointOnObject(g7,g13)
    c: PointOnObject(g8,g13)
    c: PointOnObject(g9,g13)
    c: PointOnObject(g10,g13)
    c: PointOnObject(g11,g13)
    c: PointOnObject(g12,g13)
    c: Coincident(g13,g-4)
    c: Coincident(g14,g15)
    c: Coincident(g15,g16)
    c: Coincident(g16,g17)
    c: Coincident(g17,g18)
    c: Coincident(g18,g19)
    c: Coincident(g19,g14)
    c: Equal(g14, g15-g19) x5
    c: PointOnObject(g14,g20)
    c: PointOnObject(g15,g20)
    c: PointOnObject(g16,g20)
    c: PointOnObject(g17,g20)
    c: PointOnObject(g18,g20)
    c: PointOnObject(g19,g20)
    c: Coincident(g20,g-5)
    c: Coincident(g21,g22)
    c: Coincident(g22,g23)
    c: Coincident(g23,g24)
    c: Coincident(g24,g25)
    c: Coincident(g25,g26)
    c: Coincident(g26,g21)
    c: Equal(g21, g22-g26) x5
    c: PointOnObject(g21,g27)
    c: PointOnObject(g22,g27)
    c: PointOnObject(g23,g27)
    c: PointOnObject(g24,g27)
    c: PointOnObject(g25,g27)
    c: PointOnObject(g26,g27)
    c: Coincident(g27,g-6)
    c: Horizontal(g22)
    c: Equal(g22,g15)
    c: Horizontal(g15)
    c: Equal(g15,g8)
    c: Horizontal(g8)
    c: Equal(g8,g1)
FEATURE [PartDesign::Pocket] Pocket022  label="HexNutHole001"
  BaseFeature = -> Pocket
  Direction = (-1,0,2e-16)
  Length = 1
  Length2 = 5
  Placement = pos=(0,0,0) rot=(1,0,0;1.5708rad)
  Profile = -> Sketch064
  ReferenceAxis = -> Sketch064 [N_Axis]
  Refine = true
  Suppressed = false
  Type = 0
FEATURE [PartDesign::Body] Body003  label="TramCarriage"
  AllowCompound = false
  Group = -> [Binder003,Binder004,Sketch008,Pad004,Binder005,Binder006,Sketch010,Sketch052,Hole010,Sketch053,Hole011,Fillet003,Sketch054,Pocket,Sketch064,Pocket022]
  Origin = -> Origin003
  Tip = -> Pocket022
FEATURE [PartDesign::Fillet] Fillet004
  Base = -> Pocket010 [Edge24,Edge50,Edge33,Edge25,Edge32]
  BaseFeature = -> Pocket010
  Placement = pos=(0,0,0) rot=(1,0,0;1.5708rad)
  Radius = 5
  Refine = true
  SupportTransform = false
  Suppressed = false
  UseAllEdges = false
FEATURE [PartDesign::Body] Body002  label="Foot"
  AllowCompound = false
  Group = -> [Binder001,Binder002,Sketch006,Pad003,Mirrored,Sketch007,Hole002,Sketch028,Pocket008,Sketch032,Pad013,Sketch033,Pocket010,Fillet004]
  Origin = -> Origin002
  Tip = -> Fillet004
FEATURE [PartDesign::Pad] Pad024
  BaseFeature = -> Clone
  Direction = (0,1,-3e-16)
  Length = 30
  Length2 = 10
  Placement = pos=(0,0,0) rot=(1,0,0;1.5708rad)
  Profile = -> Clone [Face12]
  Refine = true
  Suppressed = false
  Type = 0
FEATURE [Sketcher::SketchObject] Sketch055
  ArcFitTolerance = 1e-06
  AttachmentSupport = -> [Pad024]
  ExternalGeometry = -> [Pad024]
  FullyConstrained = true
  MakeInternals = false
  MapMode = 5
  Placement = pos=(0,-1.9e-15,-4) rot=(0,0,1;3.14159rad)
  sketch-geometry (6):
    g0: ArcOfCircle CenterX=0 CenterY=15.3 CenterZ=0 NormalX=0 NormalY=0 NormalZ=1 AngleXU=0 Radius=1.7 StartAngle=0 EndAngle=3.14159
    g1: ArcOfCircle CenterX=1.07e-14 CenterY=-30.3 CenterZ=0 NormalX=0 NormalY=0 NormalZ=1 AngleXU=0 Radius=1.7 StartAngle=3.14159 EndAngle=6.28319
    g2: LineSegment StartX=1.7 StartY=15.3 StartZ=0 EndX=1.7 EndY=-30.3 EndZ=0
    g3: LineSegment StartX=-1.7 StartY=15.3 StartZ=0 EndX=-1.7 EndY=-30.3 EndZ=0
    g4: GeomPoint X=0 Y=17 Z=0
    g5: GeomPoint X=0 Y=-32 Z=0
  constraints (14):
    c: Tangent(g0,g2) = 1.5708
    c: Tangent(g0,g3) = -1.5708
    c: Tangent(g1,g2) = 1.5708
    c: Tangent(g1,g3) = -1.5708
    c: Equal(g0,g1)
    c: Vertical(g3)
    c: PointOnObject(g0,g-2)
    c: Diameter(g0) = 3.4
    c: PointOnObject(g4,g0)
    c: PointOnObject(g5,g1)
    c: PointOnObject(g4,g-2)
    c: PointOnObject(g5,g-2)
    c: Distance(g4,g-3) = 3
    c: Distance(g5,g-4) = 3
FEATURE [PartDesign::Pocket] Pocket018  label="ScrewSlot"
  BaseFeature = -> Pad024
  Direction = (0,0,-1)
  Length = 5
  Length2 = 5
  Placement = pos=(0,0,0) rot=(1,0,0;1.5708rad)
  Profile = -> Sketch055
  ReferenceAxis = -> Sketch055 [N_Axis]
  Refine = true
  Suppressed = false
  Type = 1
FEATURE [PartDesign::Pocket] Pocket019  label="NutSlot"
  BaseFeature = -> Pocket018
  Direction = (0,1,-2e-16)
  Length = 0
  Length2 = 5
  Midplane = true
  Placement = pos=(0,0,0) rot=(1,0,0;1.5708rad)
  Profile = -> Sketch056
  ReferenceAxis = -> Sketch056 [N_Axis]
  Refine = true
  Suppressed = false
  Type = 1
FEATURE [Sketcher::SketchObject] Sketch058
  ArcFitTolerance = 1e-06
  AttachmentSupport = -> [Pocket019]
  ExternalGeometry = -> [Sketch057,Binder025,Pocket019]
  FullyConstrained = true
  MakeInternals = false
  MapMode = 5
  Placement = pos=(0,-5.4e-15,-11) rot=(1,0,0;3.14159rad)
  sketch-geometry (11):
    g0: LineSegment StartX=-29.5 StartY=-72.6664 StartZ=0 EndX=-26.4004 EndY=-72.6664 EndZ=0
    g1: LineSegment StartX=-29.5 StartY=-72.6664 StartZ=0 EndX=-29.5 EndY=0.2 EndZ=0
    g2: ArcOfCircle CenterX=-9.7 CenterY=0.2 CenterZ=0 NormalX=0 NormalY=0 NormalZ=1 AngleXU=0 Radius=19.8 StartAngle=1.5708 EndAngle=3.14159
    g3: ArcOfCircle CenterX=-26.4004 CenterY=-70.6664 CenterZ=0 NormalX=0 NormalY=0 NormalZ=1 AngleXU=0 Radius=2 StartAngle=4.71239 EndAngle=5.96626
    g4: LineSegment StartX=-24.5 StartY=-71.2897 StartZ=0 EndX=-13.5008 EndY=-37.7534 EndZ=0
    g5: ArcOfCircle CenterX=-9.7 CenterY=-39 CenterZ=0 NormalX=0 NormalY=0 NormalZ=1 AngleXU=0 Radius=4 StartAngle=1.5708 EndAngle=2.82467
    g6: LineSegment [constr] StartX=-16.5 StartY=-72.6664 StartZ=0 EndX=-16.5 EndY=74.3613 EndZ=0
    g7: LineSegment [constr] StartX=-16.5 StartY=74.3613 StartZ=0 EndX=-21.5 EndY=74.3613 EndZ=0
    g8: LineSegment [constr] StartX=-21.5 StartY=74.3613 StartZ=0 EndX=-21.5 EndY=-72.6664 EndZ=0
    g9: LineSegment [constr] StartX=-21.5 StartY=-72.6664 StartZ=0 EndX=-16.5 EndY=-72.6664 EndZ=0
    g10: LineSegment StartX=-9.7 StartY=20 StartZ=0 EndX=-9.7 EndY=-35 EndZ=0
  constraints (27):
    c: Coincident(g0,g-4)
    c: Horizontal(g0)
    c: Coincident(g1,g0)
    c: Tangent(g1,g2) = 1.5708
    c: Tangent(g0,g3) = -1.5708
    c: Radius(g3) = 2
    c: DistanceX(g0,g3) = 5
    c: PointOnObject(g1,g-4)
    c: Tangent(g5,g4) = 1.5708
    c: Coincident(g6,g7)
    c: Coincident(g7,g8)
    c: Coincident(g8,g9)
    c: Coincident(g9,g6)
    c: Vertical(g8)
    c: Horizontal(g7)
    c: Horizontal(g9)
    c: Distance(g6,g8) = 5
    c: Coincident(g6,g-5)
    c: Coincident(g6,g-6)
    c: Tangent(g4,g3) = -1.5708
    c: Radius(g5) = 4
    c: Coincident(g-7,g2)
    c: PointOnObject(g2,g-7)
    c: Coincident(g5,g-7)
    c: Vertical(g5,g5)
    c: Coincident(g10,g5)
    c: Coincident(g2,g10)
FEATURE [PartDesign::Pad] Pad021  label="Arm"
  BaseFeature = -> Pocket019
  Direction = (0,0,-1)
  Length = 10
  Length2 = 10
  Placement = pos=(0,0,0) rot=(1,0,0;1.5708rad)
  Profile = -> Sketch058
  ReferenceAxis = -> Sketch058 [N_Axis]
  Refine = true
  Suppressed = false
  Type = 3
  UpToFace = -> Pocket019 [Face18]
FEATURE [Sketcher::SketchObject] Sketch059
  ArcFitTolerance = 1e-06
  AttachmentSupport = -> [Pad021]
  ExternalGeometry = -> [Pad021]
  FullyConstrained = true
  MakeInternals = false
  MapMode = 5
  Placement = pos=(0,-2.6e-15,-5.97022) rot=(0,0,1;3.14159rad)
  sketch-geometry (7):
    g0: LineSegment StartX=29.5 StartY=0.2 StartZ=0 EndX=29.5 EndY=-72.6664 EndZ=0
    g1: LineSegment StartX=29.5 StartY=-72.6664 StartZ=0 EndX=26.4004 EndY=-72.6664 EndZ=0
    g2: LineSegment StartX=24.5 StartY=-71.2897 StartZ=0 EndX=24.5 EndY=-1.8 EndZ=0
    g3: LineSegment StartX=26.5 StartY=0.2 StartZ=0 EndX=29.5 EndY=0.2 EndZ=0
    g4: ArcOfCircle CenterX=26.4004 CenterY=-70.6664 CenterZ=0 NormalX=0 NormalY=0 NormalZ=1 AngleXU=0 Radius=2 StartAngle=3.45852 EndAngle=4.71239
    g5: ArcOfCircle CenterX=26.5 CenterY=-1.8 CenterZ=0 NormalX=0 NormalY=0 NormalZ=1 AngleXU=0 Radius=2 StartAngle=1.5708 EndAngle=3.14159
    g6: GeomPoint [constr] X=24.5 Y=0.2 Z=0
  constraints (17):
    c: Coincident(g0,g1)
    c: Vertical(g2)
    c: Coincident(g3,g0)
    c: Horizontal(g3)
    c: Coincident(g4,g1)
    c: Coincident(g4,g2)
    c: PointOnObject(g6,g2)
    c: PointOnObject(g6,g3)
    c: Tangent(g2,g5) = 1.5708
    c: Tangent(g3,g5) = 1.5708
    c: Equal(g5,g4)
    c: Vertical(g0)
    c: Horizontal(g1)
    c: Equal(g4,g-4)
    c: Coincident(g1,g-4)
    c: Coincident(g2,g-4)
    c: Coincident(g0,g-3)
FEATURE [PartDesign::Pad] Pad022
  BaseFeature = -> Pad021
  Direction = (0,0,1)
  Length = 9
  Length2 = 10
  Placement = pos=(0,0,0) rot=(1,0,0;1.5708rad)
  Profile = -> Sketch059
  ReferenceAxis = -> Sketch059 [N_Axis]
  Refine = true
  Suppressed = false
  Type = 0
FEATURE [Sketcher::SketchObject] Sketch060
  ArcFitTolerance = 1e-06
  AttachmentSupport = -> [Pad022]
  ExternalGeometry = -> [Sketch057]
  FullyConstrained = true
  MakeInternals = false
  MapMode = 5
  Placement = pos=(-29.5,0,0) rot=(0.707107,0,-0.707107;3.14159rad)
  sketch-geometry (1):
    g0: Circle CenterX=2.05384 CenterY=-67.6664 CenterZ=0 NormalX=0 NormalY=0 NormalZ=1 AngleXU=0 Radius=1.7
  constraints (2):
    c: Coincident(g0,g-3)
    c: Equal(g0,g-3)
FEATURE [PartDesign::Hole] Hole012
  BaseFeature = -> Pad022
  CustomThreadClearance = 0
  Depth = 222.393
  DepthType = 1
  Diameter = 3.4
  DrillForDepth = false
  DrillPoint = 1
  DrillPointAngle = 118
  HoleCutCountersinkAngle = 90
  HoleCutCustomValues = false
  HoleCutDepth = 0
  HoleCutDiameter = 6.1
  HoleCutType = 0
  ModelThread = false
  Placement = pos=(0,0,0) rot=(1,0,0;1.5708rad)
  Profile = -> Sketch060
  Refine = true
  Suppressed = false
  Tapered = false
  TaperedAngle = 90
  ThreadClass = 0
  ThreadDepth = 222.393
  ThreadDepthType = 0
  ThreadDirection = 0
  ThreadFit = 0
  ThreadSize = 9
  ThreadType = 1
  Threaded = false
  UseCustomThreadClearance = false
FEATURE [Sketcher::SketchObject] Sketch061
  ArcFitTolerance = 1e-06
  AttachmentSupport = -> [Hole012]
  ExternalGeometry = -> [Sketch057]
  FullyConstrained = true
  MakeInternals = false
  MapMode = 5
  Placement = pos=(0,72.6664,0) rot=(-1,0,0;1.5708rad)
  sketch-geometry (3):
    g0: LineSegment StartX=-29.5 StartY=11 StartZ=0 EndX=-34 EndY=7.05384 EndZ=0
    g1: LineSegment StartX=-34 StartY=7.05384 StartZ=0 EndX=-29.5 EndY=7.05384 EndZ=0
    g2: LineSegment StartX=-29.5 StartY=11 StartZ=0 EndX=-29.5 EndY=7.05384 EndZ=0
  constraints (9):
    c: Coincident(g-3,g0)
    c: Coincident(g0,g1)
    c: PointOnObject(g1,g-3)
    c: Horizontal(g1)
    c: Distance(g1,g1) = 4.5
    c: Angle(g0,g-3) = 0.850877
    c: PointOnObject(g-4,g1)
    c: Coincident(g2,g0)
    c: Coincident(g2,g1)
FEATURE [PartDesign::Pad] Pad023
  BaseFeature = -> Hole012
  Direction = (0,1,2e-16)
  Length = 10
  Length2 = 10
  Placement = pos=(0,0,0) rot=(1,0,0;1.5708rad)
  Profile = -> Sketch061
  ReferenceAxis = -> Sketch061 [N_Axis]
  Refine = true
  Reversed = true
  Suppressed = false
  Type = 3
  UpToFace = -> Hole012 [Face37]
FEATURE [Sketcher::SketchObject] Sketch062
  ArcFitTolerance = 1e-06
  AttachmentSupport = -> [Pad023]
  ExternalGeometry = -> [Pad023]
  FullyConstrained = true
  MakeInternals = false
  MapMode = 5
  Placement = pos=(-24.5,0,0) rot=(0.707107,0,0.707107;3.14159rad)
  sketch-geometry (7):
    g0: LineSegment StartX=-3.78589 StartY=-64.6664 StartZ=0 EndX=-5.51794 EndY=-67.6664 EndZ=0
    g1: LineSegment StartX=-5.51794 StartY=-67.6664 StartZ=0 EndX=-3.78589 EndY=-70.6664 EndZ=0
    g2: LineSegment StartX=-3.78589 StartY=-70.6664 StartZ=0 EndX=-0.321787 EndY=-70.6664 EndZ=0
    g3: LineSegment StartX=-0.321787 StartY=-70.6664 StartZ=0 EndX=1.41026 EndY=-67.6664 EndZ=0
    g4: LineSegment StartX=1.41026 StartY=-67.6664 StartZ=0 EndX=-0.321787 EndY=-64.6664 EndZ=0
    g5: LineSegment StartX=-0.321787 StartY=-64.6664 StartZ=0 EndX=-3.78589 EndY=-64.6664 EndZ=0
    g6: Circle [constr] CenterX=-2.05384 CenterY=-67.6664 CenterZ=0 NormalX=0 NormalY=0 NormalZ=1 AngleXU=0 Radius=3.4641
  constraints (16):
    c: Coincident(g0,g1)
    c: Coincident(g1,g2)
    c: Coincident(g2,g3)
    c: Coincident(g3,g4)
    c: Coincident(g4,g5)
    c: Coincident(g5,g0)
    c: Equal(g0, g1-g5) x5
    c: PointOnObject(g0,g6)
    c: PointOnObject(g1,g6)
    c: PointOnObject(g2,g6)
    c: PointOnObject(g3,g6)
    c: PointOnObject(g4,g6)
    c: PointOnObject(g5,g6)
    c: Coincident(g6,g-3)
    c: Horizontal(g5)
    c: Distance(g2,g5) = 6
FEATURE [PartDesign::Pocket] Pocket020  label="HexNutHole"
  BaseFeature = -> Pad023
  Direction = (-1,0,2e-16)
  Length = 2.5
  Length2 = 5
  Placement = pos=(0,0,0) rot=(1,0,0;1.5708rad)
  Profile = -> Sketch062
  ReferenceAxis = -> Sketch062 [N_Axis]
  Refine = true
  Suppressed = false
  Type = 0
FEATURE [Sketcher::SketchObject] Sketch063
  ArcFitTolerance = 1e-06
  AttachmentSupport = -> [Pocket020]
  ExternalGeometry = -> [Pocket020]
  FullyConstrained = true
  MakeInternals = false
  MapMode = 5
  Placement = pos=(0,-3.2e-15,-11) rot=(1,0,0;3.14159rad)
  expr: Constraints[0] = <<FootPads>>.Constraints.FootDiameter
  sketch-geometry (7):
    g0: Circle CenterX=-14.75 CenterY=1.23011 CenterZ=0 NormalX=0 NormalY=0 NormalZ=1 AngleXU=0 Radius=5
    g1: LineSegment [constr] StartX=-29.5 StartY=0.2 StartZ=0 EndX=0 EndY=0.2 EndZ=0
    g2: Circle CenterX=-14.75 CenterY=-16.8849 CenterZ=0 NormalX=0 NormalY=0 NormalZ=1 AngleXU=0 Radius=5
    g3: GeomPoint X=-14.75 Y=0.2 Z=0
    g4: LineSegment [constr] StartX=-14.75 StartY=1.23011 StartZ=0 EndX=-14.75 EndY=19.3452 EndZ=0
    g5: LineSegment [constr] StartX=-14.75 StartY=1.23011 StartZ=0 EndX=-14.75 EndY=-16.8849 EndZ=0
    g6: LineSegment [constr] StartX=-14.75 StartY=-16.8849 StartZ=0 EndX=-14.75 EndY=-35 EndZ=0
  constraints (18):
    c: Diameter(g0) = 10
    c: Horizontal(g1)
    c: PointOnObject(g1,g-2)
    c: Symmetric(g1,g1,g3)
    c: Vertical(g3,g2)
    c: Vertical(g0,g3)
    c: Equal(g0,g2)
    c: Coincident(g4,g0)
    c: Vertical(g4)
    c: Coincident(g5,g0)
    c: Coincident(g5,g2)
    c: Coincident(g6,g2)
    c: Vertical(g6)
    c: Equal(g6,g5)
    c: Equal(g6,g4)
    c: Horizontal(g6,g-4)
    c: PointOnObject(g4,g-3)
    c: Coincident(g1,g-3)
FEATURE [PartDesign::Pocket] Pocket021  label="FootPad"
  BaseFeature = -> Pocket020
  Direction = (0,0,1)
  Length = 3
  Length2 = 5
  Placement = pos=(0,0,0) rot=(1,0,0;1.5708rad)
  Profile = -> Sketch063
  ReferenceAxis = -> Sketch063 [N_Axis]
  Refine = true
  Suppressed = false
  Type = 0
  expr: Length = <<FootPadPocket>>.Length
FEATURE [PartDesign::Body] Body011  label="CountdownBracketL"
  AllowCompound = false
  Group = -> [Clone,Pad024,Sketch055,Pocket018,Sketch056,Pocket019,Binder024,Sketch057,Binder025,Sketch058,Pad021,Sketch059,Pad022,Sketch060,Hole012,Sketch061,Pad023,Sketch062,Pocket020,Sketch063,Pocket021]
  Origin = -> Origin012
  Tip = -> Pocket021
FEATURE [Sketcher::SketchObject] Sketch065
  ArcFitTolerance = 1e-06
  FullyConstrained = false
  MakeInternals = false
  Placement = pos=(0,0,-11) rot=(0,0,-1;3.14159rad)
  sketch-geometry (193):
    g0: LineSegment StartX=-17 StartY=-18.5371 StartZ=0 EndX=-17 EndY=-21.5 EndZ=0
    g1: LineSegment StartX=-17 StartY=-21.5 StartZ=0 EndX=-17.7681 EndY=-21.5 EndZ=0
    g2: LineSegment StartX=-17.7681 StartY=-21.5 StartZ=0 EndX=-17.7681 EndY=-19.7222 EndZ=0
    g3: BSplineCurve PolesCount=4 KnotsCount=2 Degree=3 IsPeriodic=0
    g4: BSplineCurve PolesCount=4 KnotsCount=2 Degree=3 IsPeriodic=0
    g5: LineSegment StartX=-18.7119 StartY=-19.5246 StartZ=0 EndX=-18.7119 EndY=-21.5 EndZ=0
    g6: LineSegment StartX=-18.7119 StartY=-21.5 StartZ=0 EndX=-19.4801 EndY=-21.5 EndZ=0
    g7: LineSegment StartX=-19.4801 StartY=-21.5 StartZ=0 EndX=-19.4801 EndY=-19.7222 EndZ=0
    g8: BSplineCurve PolesCount=4 KnotsCount=2 Degree=3 IsPeriodic=0
    g9: BSplineCurve PolesCount=4 KnotsCount=2 Degree=3 IsPeriodic=0
    g10: LineSegment StartX=-20.424 StartY=-19.5246 StartZ=0 EndX=-20.424 EndY=-21.5 EndZ=0
    g11: LineSegment StartX=-20.424 StartY=-21.5 StartZ=0 EndX=-21.1922 EndY=-21.5 EndZ=0
    g12: LineSegment StartX=-21.1922 StartY=-21.5 StartZ=0 EndX=-21.1922 EndY=-19.4041 EndZ=0
    g13: BSplineCurve PolesCount=4 KnotsCount=2 Degree=3 IsPeriodic=0
    g14: BSplineCurve PolesCount=4 KnotsCount=2 Degree=3 IsPeriodic=0
    g15: BSplineCurve PolesCount=4 KnotsCount=2 Degree=3 IsPeriodic=0
    g16: BSplineCurve PolesCount=4 KnotsCount=2 Degree=3 IsPeriodic=0
    g17: LineSegment StartX=-17.7627 StartY=-18.9047 StartZ=0 EndX=-17.7627 EndY=-18.5371 EndZ=0
    g18: LineSegment StartX=-17.7627 StartY=-18.5371 StartZ=0 EndX=-17 EndY=-18.5371 EndZ=0
    g19: BSplineCurve PolesCount=4 KnotsCount=2 Degree=3 IsPeriodic=0
    g20: BSplineCurve PolesCount=4 KnotsCount=2 Degree=3 IsPeriodic=0
    g21: LineSegment StartX=-23.536 StartY=-21.5 StartZ=0 EndX=-24.3702 EndY=-21.5 EndZ=0
    g22: LineSegment StartX=-24.3702 StartY=-21.5 StartZ=0 EndX=-24.3702 EndY=-21.4068 EndZ=0
    g23: BSplineCurve PolesCount=4 KnotsCount=2 Degree=3 IsPeriodic=0
    g24: LineSegment StartX=-24.1946 StartY=-21.0447 StartZ=0 EndX=-24.1946 EndY=-19.3985 EndZ=0
    g25: BSplineCurve PolesCount=4 KnotsCount=2 Degree=3 IsPeriodic=0
    g26: BSplineCurve PolesCount=4 KnotsCount=2 Degree=3 IsPeriodic=0
    g27: LineSegment StartX=-21.7143 StartY=-19.5138 StartZ=0 EndX=-22.455 EndY=-19.5138 EndZ=0
    g28: BSplineCurve PolesCount=4 KnotsCount=2 Degree=3 IsPeriodic=0
    g29: BSplineCurve PolesCount=4 KnotsCount=2 Degree=3 IsPeriodic=0
    g30: BSplineCurve PolesCount=4 KnotsCount=2 Degree=3 IsPeriodic=0
    g31: LineSegment StartX=-22.8282 StartY=-19.7497 StartZ=0 EndX=-22.5209 EndY=-19.8045 EndZ=0
    g32: BSplineCurve PolesCount=4 KnotsCount=2 Degree=3 IsPeriodic=0
    g33: BSplineCurve PolesCount=4 KnotsCount=2 Degree=3 IsPeriodic=0
    g34: BSplineCurve PolesCount=4 KnotsCount=2 Degree=3 IsPeriodic=0
    g35: BSplineCurve PolesCount=4 KnotsCount=2 Degree=3 IsPeriodic=0
    g36: BSplineCurve PolesCount=4 KnotsCount=2 Degree=3 IsPeriodic=0
    g37: LineSegment StartX=-22.8557 StartY=-20.2436 StartZ=0 EndX=-23.1191 EndY=-20.1941 EndZ=0
    g38: BSplineCurve PolesCount=4 KnotsCount=2 Degree=3 IsPeriodic=0
    g39: LineSegment StartX=-23.4428 StartY=-20.1009 StartZ=0 EndX=-23.4428 EndY=-20.3093 EndZ=0
    g40: LineSegment StartX=-25.6028 StartY=-18.5371 StartZ=0 EndX=-24.8348 EndY=-18.5371 EndZ=0
    g41: LineSegment StartX=-24.8348 StartY=-18.5371 StartZ=0 EndX=-24.8348 EndY=-21.5 EndZ=0
    g42: LineSegment StartX=-24.8348 StartY=-21.5 StartZ=0 EndX=-25.6028 EndY=-21.5 EndZ=0
    g43: LineSegment StartX=-25.6028 StartY=-21.5 StartZ=0 EndX=-25.6028 EndY=-18.5371 EndZ=0
    g44: LineSegment StartX=-25.6028 StartY=-17.5 StartZ=0 EndX=-24.8348 EndY=-17.5 EndZ=0
    g45: LineSegment StartX=-24.8348 StartY=-17.5 StartZ=0 EndX=-24.8348 EndY=-18.1859 EndZ=0
    g46: LineSegment StartX=-24.8348 StartY=-18.1859 StartZ=0 EndX=-25.6028 EndY=-18.1859 EndZ=0
    g47: LineSegment StartX=-25.6028 StartY=-18.1859 StartZ=0 EndX=-25.6028 EndY=-17.5 EndZ=0
    g48: LineSegment StartX=-27.0432 StartY=-17.5 StartZ=0 EndX=-26.2752 EndY=-17.5 EndZ=0
    g49: LineSegment StartX=-26.2752 StartY=-17.5 StartZ=0 EndX=-26.2752 EndY=-21.5 EndZ=0
    g50: LineSegment StartX=-26.2752 StartY=-21.5 StartZ=0 EndX=-27.0432 EndY=-21.5 EndZ=0
    g51: LineSegment StartX=-27.0432 StartY=-21.5 StartZ=0 EndX=-27.0432 EndY=-17.5 EndZ=0
    g52: BSplineCurve PolesCount=4 KnotsCount=2 Degree=3 IsPeriodic=0
    g53: BSplineCurve PolesCount=4 KnotsCount=2 Degree=3 IsPeriodic=0
    g54: BSplineCurve PolesCount=4 KnotsCount=2 Degree=3 IsPeriodic=0
    g55: BSplineCurve PolesCount=4 KnotsCount=2 Degree=3 IsPeriodic=0
    g56: BSplineCurve PolesCount=4 KnotsCount=2 Degree=3 IsPeriodic=0
    g57: BSplineCurve PolesCount=4 KnotsCount=2 Degree=3 IsPeriodic=0
    g58: BSplineCurve PolesCount=4 KnotsCount=2 Degree=3 IsPeriodic=0
    g59: BSplineCurve PolesCount=4 KnotsCount=2 Degree=3 IsPeriodic=0
    g60: BSplineCurve PolesCount=4 KnotsCount=2 Degree=3 IsPeriodic=0
    g61: LineSegment StartX=-31.384 StartY=-22.005 StartZ=0 EndX=-31.2304 EndY=-21.6043 EndZ=0
    g62: BSplineCurve PolesCount=4 KnotsCount=2 Degree=3 IsPeriodic=0
    g63: BSplineCurve PolesCount=4 KnotsCount=2 Degree=3 IsPeriodic=0
    g64: BSplineCurve PolesCount=4 KnotsCount=2 Degree=3 IsPeriodic=0
    g65: BSplineCurve PolesCount=4 KnotsCount=2 Degree=3 IsPeriodic=0
    g66: BSplineCurve PolesCount=4 KnotsCount=2 Degree=3 IsPeriodic=0
    g67: BSplineCurve PolesCount=4 KnotsCount=2 Degree=3 IsPeriodic=0
    g68: BSplineCurve PolesCount=4 KnotsCount=2 Degree=3 IsPeriodic=0
    g69: BSplineCurve PolesCount=4 KnotsCount=2 Degree=3 IsPeriodic=0
    g70: LineSegment StartX=-31.0275 StartY=-20.249 StartZ=0 EndX=-31.4555 EndY=-18.7126 EndZ=0
    g71: LineSegment StartX=-31.4555 StartY=-18.7126 StartZ=0 EndX=-30.9616 EndY=-18.7126 EndZ=0
    g72: LineSegment StartX=-30.9616 StartY=-18.7126 StartZ=0 EndX=-30.8737 EndY=-19.0529 EndZ=0
    g73: BSplineCurve PolesCount=4 KnotsCount=2 Degree=3 IsPeriodic=0
    g74: BSplineCurve PolesCount=4 KnotsCount=2 Degree=3 IsPeriodic=0
    g75: BSplineCurve PolesCount=4 KnotsCount=2 Degree=3 IsPeriodic=0
    g76: BSplineCurve PolesCount=4 KnotsCount=2 Degree=3 IsPeriodic=0
    g77: BSplineCurve PolesCount=4 KnotsCount=2 Degree=3 IsPeriodic=0
    g78: BSplineCurve PolesCount=4 KnotsCount=2 Degree=3 IsPeriodic=0
    g79: LineSegment StartX=-33.9302 StartY=-18.5371 StartZ=0 EndX=-33.162 EndY=-18.5371 EndZ=0
    g80: LineSegment StartX=-33.162 StartY=-18.5371 StartZ=0 EndX=-33.162 EndY=-21.8458 EndZ=0
    g81: BSplineCurve PolesCount=4 KnotsCount=2 Degree=3 IsPeriodic=0
    g82: BSplineCurve PolesCount=4 KnotsCount=2 Degree=3 IsPeriodic=0
    g83: LineSegment StartX=-32.7998 StartY=-22.0543 StartZ=0 EndX=-32.7998 EndY=-22.6689 EndZ=0
    g84: BSplineCurve PolesCount=4 KnotsCount=2 Degree=3 IsPeriodic=0
    g85: BSplineCurve PolesCount=4 KnotsCount=2 Degree=3 IsPeriodic=0
    g86: LineSegment StartX=-33.9302 StartY=-22.0159 StartZ=0 EndX=-33.9302 EndY=-18.5371 EndZ=0
    g87: LineSegment StartX=-33.9302 StartY=-17.5 StartZ=0 EndX=-33.162 EndY=-17.5 EndZ=0
    g88: LineSegment StartX=-33.162 StartY=-17.5 StartZ=0 EndX=-33.162 EndY=-18.1859 EndZ=0
    g89: LineSegment StartX=-33.162 StartY=-18.1859 StartZ=0 EndX=-33.9302 EndY=-18.1859 EndZ=0
    g90: LineSegment StartX=-33.9302 StartY=-18.1859 StartZ=0 EndX=-33.9302 EndY=-17.5 EndZ=0
    g91: LineSegment StartX=-36.3843 StartY=-19.6893 StartZ=0 EndX=-36.3843 EndY=-21.5 EndZ=0
    g92: LineSegment StartX=-36.3843 StartY=-21.5 StartZ=0 EndX=-37.1525 EndY=-21.5 EndZ=0
    g93: LineSegment StartX=-37.1525 StartY=-21.5 StartZ=0 EndX=-37.1525 EndY=-19.5138 EndZ=0
    g94: BSplineCurve PolesCount=4 KnotsCount=2 Degree=3 IsPeriodic=0
    g95: BSplineCurve PolesCount=4 KnotsCount=2 Degree=3 IsPeriodic=0
    g96: LineSegment StartX=-35.3197 StartY=-18.965 StartZ=0 EndX=-35.3197 EndY=-17.5 EndZ=0
    g97: LineSegment StartX=-35.3197 StartY=-17.5 StartZ=0 EndX=-34.5517 EndY=-17.5 EndZ=0
    g98: LineSegment StartX=-34.5517 StartY=-17.5 StartZ=0 EndX=-34.5517 EndY=-21.5 EndZ=0
    g99: LineSegment StartX=-34.5517 StartY=-21.5 StartZ=0 EndX=-35.3197 EndY=-21.5 EndZ=0
    g100: LineSegment StartX=-35.3197 StartY=-21.5 StartZ=0 EndX=-35.3197 EndY=-19.7222 EndZ=0
    g101: BSplineCurve PolesCount=4 KnotsCount=2 Degree=3 IsPeriodic=0
    g102: BSplineCurve PolesCount=4 KnotsCount=2 Degree=3 IsPeriodic=0
    g103: LineSegment StartX=-37.742 StartY=-18.5371 StartZ=0 EndX=-37.742 EndY=-21.5 EndZ=0
    g104: LineSegment StartX=-37.742 StartY=-21.5 StartZ=0 EndX=-38.5102 EndY=-21.5 EndZ=0
    g105: LineSegment StartX=-38.5102 StartY=-21.5 StartZ=0 EndX=-38.5102 EndY=-19.7222 EndZ=0
    g106: BSplineCurve PolesCount=4 KnotsCount=2 Degree=3 IsPeriodic=0
    g107: BSplineCurve PolesCount=4 KnotsCount=2 Degree=3 IsPeriodic=0
    g108: LineSegment StartX=-39.6241 StartY=-19.6729 StartZ=0 EndX=-39.6241 EndY=-21.5 EndZ=0
    g109: LineSegment StartX=-39.6241 StartY=-21.5 StartZ=0 EndX=-40.3922 EndY=-21.5 EndZ=0
    g110: LineSegment StartX=-40.3922 StartY=-21.5 StartZ=0 EndX=-40.3922 EndY=-19.5138 EndZ=0
    g111: BSplineCurve PolesCount=4 KnotsCount=2 Degree=3 IsPeriodic=0
    g112: BSplineCurve PolesCount=4 KnotsCount=2 Degree=3 IsPeriodic=0
    g113: LineSegment StartX=-38.5102 StartY=-18.965 StartZ=0 EndX=-38.5102 EndY=-18.5371 EndZ=0
    g114: LineSegment StartX=-38.5102 StartY=-18.5371 StartZ=0 EndX=-37.742 EndY=-18.5371 EndZ=0
    g115: BSplineCurve PolesCount=4 KnotsCount=2 Degree=3 IsPeriodic=0
    g116: BSplineCurve PolesCount=4 KnotsCount=2 Degree=3 IsPeriodic=0
    g117: BSplineCurve PolesCount=4 KnotsCount=2 Degree=3 IsPeriodic=0
    g118: LineSegment StartX=-43.5707 StartY=-20.666 StartZ=0 EndX=-42.8135 EndY=-20.666 EndZ=0
    g119: BSplineCurve PolesCount=4 KnotsCount=2 Degree=3 IsPeriodic=0
    g120: BSplineCurve PolesCount=4 KnotsCount=2 Degree=3 IsPeriodic=0
    g121: LineSegment StartX=-41.6118 StartY=-20.26 StartZ=0 EndX=-43.5982 EndY=-20.26 EndZ=0
    g122: BSplineCurve PolesCount=4 KnotsCount=2 Degree=3 IsPeriodic=0
    g123: BSplineCurve PolesCount=4 KnotsCount=2 Degree=3 IsPeriodic=0
    g124: LineSegment StartX=-42.8024 StartY=-19.7497 StartZ=0 EndX=-41.6228 EndY=-19.7497 EndZ=0
    g125: BSplineCurve PolesCount=4 KnotsCount=2 Degree=3 IsPeriodic=0
    g126: BSplineCurve PolesCount=4 KnotsCount=2 Degree=3 IsPeriodic=0
    g127: LineSegment StartX=-45.4039 StartY=-18.5974 StartZ=0 EndX=-44.9759 EndY=-18.5974 EndZ=0
    g128: LineSegment StartX=-44.9759 StartY=-18.5974 StartZ=0 EndX=-44.9759 EndY=-17.8017 EndZ=0
    g129: LineSegment StartX=-44.9759 StartY=-17.8017 StartZ=0 EndX=-44.2076 EndY=-17.8017 EndZ=0
    g130: LineSegment StartX=-44.2076 StartY=-17.8017 StartZ=0 EndX=-44.2076 EndY=-18.5974 EndZ=0
    g131: LineSegment StartX=-44.2076 StartY=-18.5974 StartZ=0 EndX=-43.8292 EndY=-18.5974 EndZ=0
    g132: LineSegment StartX=-43.8292 StartY=-18.5974 StartZ=0 EndX=-43.8292 EndY=-19.1078 EndZ=0
    g133: LineSegment StartX=-43.8292 StartY=-19.1078 StartZ=0 EndX=-44.2076 EndY=-19.1078 EndZ=0
    g134: LineSegment StartX=-44.2076 StartY=-19.1078 StartZ=0 EndX=-44.2076 EndY=-20.9295 EndZ=0
    g135: BSplineCurve PolesCount=4 KnotsCount=2 Degree=3 IsPeriodic=0
    g136: BSplineCurve PolesCount=4 KnotsCount=2 Degree=3 IsPeriodic=0
    g137: LineSegment StartX=-45.4039 StartY=-21.5659 StartZ=0 EndX=-45.4039 EndY=-21.0283 EndZ=0
    g138: BSplineCurve PolesCount=4 KnotsCount=2 Degree=3 IsPeriodic=0
    g139: BSplineCurve PolesCount=4 KnotsCount=2 Degree=3 IsPeriodic=0
    g140: LineSegment StartX=-44.9759 StartY=-20.7209 StartZ=0 EndX=-44.9759 EndY=-19.1078 EndZ=0
    g141: LineSegment StartX=-44.9759 StartY=-19.1078 StartZ=0 EndX=-45.4039 EndY=-19.1078 EndZ=0
    g142: LineSegment StartX=-45.4039 StartY=-19.1078 StartZ=0 EndX=-45.4039 EndY=-18.5974 EndZ=0
    g143: LineSegment StartX=-46.7556 StartY=-20.6989 StartZ=0 EndX=-45.9326 EndY=-20.6989 EndZ=0
    g144: LineSegment StartX=-45.9326 StartY=-20.6989 StartZ=0 EndX=-45.9326 EndY=-21.5 EndZ=0
    g145: LineSegment StartX=-45.9326 StartY=-21.5 StartZ=0 EndX=-46.7556 EndY=-21.5 EndZ=0
    g146: LineSegment StartX=-46.7556 StartY=-21.5 StartZ=0 EndX=-46.7556 EndY=-20.6989 EndZ=0
    g147: BSplineCurve PolesCount=4 KnotsCount=2 Degree=3 IsPeriodic=0
    g148: LineSegment StartX=-49.2308 StartY=-19.6454 StartZ=0 EndX=-49.966 EndY=-19.6454 EndZ=0
    g149: BSplineCurve PolesCount=4 KnotsCount=2 Degree=3 IsPeriodic=0
    g150: BSplineCurve PolesCount=4 KnotsCount=2 Degree=3 IsPeriodic=0
    g151: BSplineCurve PolesCount=4 KnotsCount=2 Degree=3 IsPeriodic=0
    g152: BSplineCurve PolesCount=4 KnotsCount=2 Degree=3 IsPeriodic=0
    g153: LineSegment StartX=-49.966 StartY=-20.474 StartZ=0 EndX=-49.2308 EndY=-20.474 EndZ=0
    g154: BSplineCurve PolesCount=4 KnotsCount=2 Degree=3 IsPeriodic=0
    g155: BSplineCurve PolesCount=4 KnotsCount=2 Degree=3 IsPeriodic=0
    g156: BSplineCurve PolesCount=4 KnotsCount=2 Degree=3 IsPeriodic=0
    g157: BSplineCurve PolesCount=4 KnotsCount=2 Degree=3 IsPeriodic=0
    g158: BSplineCurve PolesCount=4 KnotsCount=2 Degree=3 IsPeriodic=0
    g159: BSplineCurve PolesCount=4 KnotsCount=2 Degree=3 IsPeriodic=0
    g160: BSplineCurve PolesCount=4 KnotsCount=2 Degree=3 IsPeriodic=0
    g161: BSplineCurve PolesCount=4 KnotsCount=2 Degree=3 IsPeriodic=0
    g162: BSplineCurve PolesCount=4 KnotsCount=2 Degree=3 IsPeriodic=0
    g163: BSplineCurve PolesCount=4 KnotsCount=2 Degree=3 IsPeriodic=0
    g164: BSplineCurve PolesCount=4 KnotsCount=2 Degree=3 IsPeriodic=0
    g165: LineSegment StartX=-54.5406 StartY=-20.6989 StartZ=0 EndX=-53.7175 EndY=-20.6989 EndZ=0
    g166: LineSegment StartX=-53.7175 StartY=-20.6989 StartZ=0 EndX=-53.7175 EndY=-21.5 EndZ=0
    g167: LineSegment StartX=-53.7175 StartY=-21.5 StartZ=0 EndX=-54.5406 EndY=-21.5 EndZ=0
    g168: LineSegment StartX=-54.5406 StartY=-21.5 StartZ=0 EndX=-54.5406 EndY=-20.6989 EndZ=0
    g169: LineSegment StartX=-57.8552 StartY=-21.5 StartZ=0 EndX=-57.8552 EndY=-18.5371 EndZ=0
    g170: LineSegment StartX=-57.8552 StartY=-18.5371 StartZ=0 EndX=-57.087 EndY=-18.5371 EndZ=0
    g171: LineSegment StartX=-57.087 StartY=-18.5371 StartZ=0 EndX=-57.087 EndY=-20.3917 EndZ=0
    g172: BSplineCurve PolesCount=4 KnotsCount=2 Degree=3 IsPeriodic=0
    g173: BSplineCurve PolesCount=4 KnotsCount=2 Degree=3 IsPeriodic=0
    g174: LineSegment StartX=-55.9731 StartY=-20.4411 StartZ=0 EndX=-55.9731 EndY=-18.5371 EndZ=0
    g175: LineSegment StartX=-55.9731 StartY=-18.5371 StartZ=0 EndX=-55.2049 EndY=-18.5371 EndZ=0
    g176: LineSegment StartX=-55.2049 StartY=-18.5371 StartZ=0 EndX=-55.2049 EndY=-20.6001 EndZ=0
    g177: BSplineCurve PolesCount=4 KnotsCount=2 Degree=3 IsPeriodic=0
    g178: BSplineCurve PolesCount=4 KnotsCount=2 Degree=3 IsPeriodic=0
    g179: LineSegment StartX=-57.087 StartY=-21.1488 StartZ=0 EndX=-57.087 EndY=-21.5 EndZ=0
    g180: LineSegment StartX=-57.087 StartY=-21.5 StartZ=0 EndX=-57.8552 EndY=-21.5 EndZ=0
    g181: LineSegment StartX=-59.3281 StartY=-19.6893 StartZ=0 EndX=-59.3281 EndY=-17.5 EndZ=0
    g182: LineSegment StartX=-59.3281 StartY=-17.5 StartZ=0 EndX=-58.5599 EndY=-17.5 EndZ=0
    g183: LineSegment StartX=-58.5599 StartY=-17.5 StartZ=0 EndX=-58.5599 EndY=-21.5 EndZ=0
    g184: LineSegment StartX=-58.5599 StartY=-21.5 StartZ=0 EndX=-59.3281 EndY=-21.5 EndZ=0
    g185: LineSegment StartX=-59.3281 StartY=-21.5 StartZ=0 EndX=-59.3281 EndY=-20.5288 EndZ=0
    g186: LineSegment StartX=-59.3281 StartY=-20.5288 StartZ=0 EndX=-59.6353 EndY=-20.1941 EndZ=0
    g187: LineSegment StartX=-59.6353 StartY=-20.1941 StartZ=0 EndX=-60.3432 EndY=-21.5 EndZ=0
    g188: LineSegment StartX=-60.3432 StartY=-21.5 StartZ=0 EndX=-61.2431 EndY=-21.5 EndZ=0
    g189: LineSegment StartX=-61.2431 StartY=-21.5 StartZ=0 EndX=-60.1621 EndY=-19.6565 EndZ=0
    g190: LineSegment StartX=-60.1621 StartY=-19.6565 StartZ=0 EndX=-61.1718 EndY=-18.5371 EndZ=0
    g191: LineSegment StartX=-61.1718 StartY=-18.5371 StartZ=0 EndX=-60.2993 EndY=-18.5371 EndZ=0
    g192: LineSegment StartX=-60.2993 StartY=-18.5371 StartZ=0 EndX=-59.3281 EndY=-19.6893 EndZ=0
  constraints (286):
    c: Vertical(g0)
    c: Coincident(g0,g1)
    c: Horizontal(g1)
    c: Coincident(g1,g2)
    c: Vertical(g2)
    c: Coincident(g2,g3)
    c: Coincident(g3,g4)
    c: Coincident(g4,g5)
    c: Vertical(g5)
    c: Coincident(g5,g6)
    c: Horizontal(g6)
    c: Coincident(g6,g7)
    c: Vertical(g7)
    c: Coincident(g7,g8)
    c: Coincident(g8,g9)
    c: Coincident(g9,g10)
    c: Vertical(g10)
    c: Coincident(g10,g11)
    c: Horizontal(g11)
    c: Coincident(g11,g12)
    c: Vertical(g12)
    c: Coincident(g12,g13)
    c: Coincident(g13,g14)
    c: Coincident(g14,g15)
    c: Coincident(g15,g16)
    c: Coincident(g16,g17)
    c: Vertical(g17)
    c: Coincident(g17,g18)
    c: Horizontal(g18)
    c: Coincident(g18,g0)
    c: Coincident(g19,g20)
    c: Coincident(g20,g21)
    c: Horizontal(g21)
    c: Coincident(g21,g22)
    c: Vertical(g22)
    c: Coincident(g22,g23)
    c: Coincident(g23,g24)
    c: Vertical(g24)
    c: Coincident(g24,g25)
    c: Coincident(g25,g26)
    c: Coincident(g26,g27)
    c: Horizontal(g27)
    c: Coincident(g27,g28)
    c: Coincident(g28,g29)
    c: Coincident(g29,g30)
    c: Coincident(g30,g31)
    c: Coincident(g31,g32)
    c: Coincident(g32,g33)
    c: Coincident(g33,g19)
    c: Coincident(g34,g35)
    c: Coincident(g35,g36)
    c: Coincident(g36,g37)
    c: Coincident(g37,g38)
    c: Coincident(g38,g39)
    c: Vertical(g39)
    c: Coincident(g39,g34)
    c: Horizontal(g40)
    c: Coincident(g40,g41)
    c: Vertical(g41)
    c: Coincident(g41,g42)
    c: Horizontal(g42)
    c: Coincident(g42,g43)
    c: Vertical(g43)
    c: Coincident(g43,g40)
    c: Horizontal(g44)
    c: Coincident(g44,g45)
    c: Vertical(g45)
    c: Coincident(g45,g46)
    c: Horizontal(g46)
    c: Coincident(g46,g47)
    c: Vertical(g47)
    c: Coincident(g47,g44)
    c: Horizontal(g48)
    c: Coincident(g48,g49)
    c: Vertical(g49)
    c: Coincident(g49,g50)
    c: Horizontal(g50)
    c: Coincident(g50,g51)
    c: Vertical(g51)
    c: Coincident(g51,g48)
    c: Coincident(g52,g53)
    c: Coincident(g53,g54)
    c: Coincident(g54,g55)
    c: Coincident(g55,g56)
    c: Coincident(g56,g57)
    c: Coincident(g57,g58)
    c: Coincident(g58,g59)
    c: Coincident(g59,g60)
    c: Coincident(g60,g61)
    c: Coincident(g61,g62)
    c: Coincident(g62,g63)
    c: Coincident(g63,g64)
    c: Coincident(g64,g65)
    c: Coincident(g65,g66)
    c: Coincident(g66,g67)
    c: Coincident(g67,g68)
    c: Coincident(g68,g69)
    c: Coincident(g69,g70)
    c: Coincident(g70,g71)
    c: Horizontal(g71)
    c: Coincident(g71,g72)
    c: Coincident(g72,g73)
    c: Coincident(g73,g74)
    c: Coincident(g74,g52)
    c: Coincident(g75,g76)
    c: Coincident(g76,g77)
    c: Coincident(g77,g78)
    c: Coincident(g78,g75)
    c: Horizontal(g79)
    c: Coincident(g79,g80)
    c: Vertical(g80)
    c: Coincident(g80,g81)
    c: Coincident(g81,g82)
    c: Coincident(g82,g83)
    c: Vertical(g83)
    c: Coincident(g83,g84)
    c: Coincident(g84,g85)
    c: Coincident(g85,g86)
    c: Vertical(g86)
    c: Coincident(g86,g79)
    c: Horizontal(g87)
    c: Coincident(g87,g88)
    c: Vertical(g88)
    c: Coincident(g88,g89)
    c: Horizontal(g89)
    c: Coincident(g89,g90)
    c: Vertical(g90)
    c: Coincident(g90,g87)
    c: Vertical(g91)
    c: Coincident(g91,g92)
    c: Horizontal(g92)
    c: Coincident(g92,g93)
    c: Vertical(g93)
    c: Coincident(g93,g94)
    c: Coincident(g94,g95)
    c: Coincident(g95,g96)
    c: Vertical(g96)
    c: Coincident(g96,g97)
    c: Horizontal(g97)
    c: Coincident(g97,g98)
    c: Vertical(g98)
    c: Coincident(g98,g99)
    c: Horizontal(g99)
    c: Coincident(g99,g100)
    c: Vertical(g100)
    c: Coincident(g100,g101)
    c: Coincident(g101,g102)
    c: Coincident(g102,g91)
    c: Vertical(g103)
    c: Coincident(g103,g104)
    c: Horizontal(g104)
    c: Coincident(g104,g105)
    c: Vertical(g105)
    c: Coincident(g105,g106)
    c: Coincident(g106,g107)
    c: Coincident(g107,g108)
    c: Vertical(g108)
    c: Coincident(g108,g109)
    c: Horizontal(g109)
    c: Coincident(g109,g110)
    c: Vertical(g110)
    c: Coincident(g110,g111)
    c: Coincident(g111,g112)
    c: Coincident(g112,g113)
    c: Vertical(g113)
    c: Coincident(g113,g114)
    c: Horizontal(g114)
    c: Coincident(g114,g103)
    c: Coincident(g115,g116)
    c: Coincident(g116,g117)
    c: Coincident(g117,g118)
    c: Horizontal(g118)
    c: Coincident(g118,g119)
    c: Coincident(g119,g120)
    c: Coincident(g120,g121)
    c: Horizontal(g121)
    c: Coincident(g121,g122)
    c: Coincident(g122,g123)
    c: Coincident(g123,g115)
    c: Horizontal(g124)
    c: Coincident(g124,g125)
    c: Coincident(g125,g126)
    c: Coincident(g126,g124)
    c: Horizontal(g127)
    c: Coincident(g127,g128)
    c: Vertical(g128)
    c: Coincident(g128,g129)
    c: Horizontal(g129)
    c: Coincident(g129,g130)
    c: Vertical(g130)
    c: Coincident(g130,g131)
    c: Horizontal(g131)
    c: Coincident(g131,g132)
    c: Vertical(g132)
    c: Coincident(g132,g133)
    c: Horizontal(g133)
    c: Coincident(g133,g134)
    c: Vertical(g134)
    c: Coincident(g134,g135)
    c: Coincident(g135,g136)
    c: Coincident(g136,g137)
    c: Vertical(g137)
    c: Coincident(g137,g138)
    c: Coincident(g138,g139)
    c: Coincident(g139,g140)
    c: Vertical(g140)
    c: Coincident(g140,g141)
    c: Horizontal(g141)
    c: Coincident(g141,g142)
    c: Vertical(g142)
    c: Coincident(g142,g127)
    c: Horizontal(g143)
    c: Coincident(g143,g144)
    c: Vertical(g144)
    c: Coincident(g144,g145)
    c: Horizontal(g145)
    c: Coincident(g145,g146)
    c: Vertical(g146)
    c: Coincident(g146,g143)
    c: Coincident(g147,g148)
    c: Horizontal(g148)
    c: Coincident(g148,g149)
    c: Coincident(g149,g150)
    c: Coincident(g150,g151)
    c: Coincident(g151,g152)
    c: Coincident(g152,g153)
    c: Horizontal(g153)
    c: Coincident(g153,g154)
    c: Coincident(g154,g155)
    c: Coincident(g155,g156)
    c: Coincident(g156,g147)
    c: Coincident(g157,g158)
    c: Coincident(g158,g159)
    c: Coincident(g159,g160)
    c: Coincident(g160,g157)
    c: Coincident(g161,g162)
    c: Coincident(g162,g163)
    c: Coincident(g163,g164)
    c: Coincident(g164,g161)
    c: Horizontal(g165)
    c: Coincident(g165,g166)
    c: Vertical(g166)
    c: Coincident(g166,g167)
    c: Horizontal(g167)
    c: Coincident(g167,g168)
    c: Vertical(g168)
    c: Coincident(g168,g165)
    c: Vertical(g169)
    c: Coincident(g169,g170)
    c: Horizontal(g170)
    c: Coincident(g170,g171)
    c: Vertical(g171)
    c: Coincident(g171,g172)
    c: Coincident(g172,g173)
    c: Coincident(g173,g174)
    c: Vertical(g174)
    c: Coincident(g174,g175)
    c: Horizontal(g175)
    c: Coincident(g175,g176)
    c: Vertical(g176)
    c: Coincident(g176,g177)
    c: Coincident(g177,g178)
    c: Coincident(g178,g179)
    c: Vertical(g179)
    c: Coincident(g179,g180)
    c: Horizontal(g180)
    c: Coincident(g180,g169)
    c: Vertical(g181)
    c: Coincident(g181,g182)
    c: Horizontal(g182)
    c: Coincident(g182,g183)
    c: Vertical(g183)
    c: Coincident(g183,g184)
    c: Horizontal(g184)
    c: Coincident(g184,g185)
    c: Vertical(g185)
    c: Coincident(g185,g186)
    c: Coincident(g186,g187)
    c: Coincident(g187,g188)
    c: Horizontal(g188)
    c: Coincident(g188,g189)
    c: Coincident(g189,g190)
    c: Coincident(g190,g191)
    c: Horizontal(g191)
    c: Coincident(g191,g192)
    c: Coincident(g192,g181)
FEATURE [PartDesign::Pocket] Pocket023
  BaseFeature = -> Mirrored004
  Direction = (0,0,-1)
  Length = 0.2
  Length2 = 5
  Profile = -> Sketch065
  ReferenceAxis = -> Sketch065 [N_Axis]
  Refine = true
  Reversed = true
  Suppressed = false
  Type = 0
FEATURE [PartDesign::Body] Body006  label="Stand"
  AllowCompound = false
  Group = -> [Binder012,Pad008,Mirrored003,Sketch023,Binder013,Pad009,Sketch024,Pocket006,Sketch025,Hole005,Sketch026,Hole006,Sketch027,Pocket007,Binder016,Sketch037,Pocket011,Sketch038,Pad017,Sketch039,Hole007,Binder017,Sketch040,Pocket012,Sketch041,Pocket013,Sketch042,Pocket014,Pocket015,Sketch043,Hole008,Sketch044,Sketch045,SubtractivePipe,Sketch049,Pad020,Mirrored004,Sketch065,Pocket023]
  Origin = -> Origin006
  Tip = -> Pocket023
FEATURE [Part::FeaturePython] Clone001  label="CountdownBracketR"  # Draft clone (typed FeaturePython)
  AttacherType = Attacher::AttachEngine3D
  Fuse = false
  Objects = -> [Body011]
  Scale = (1,-1,1)
FEATURE [App::Link] Rail  label="Rail001"
  LinkedObject = -> Body
FEATURE [App::FeaturePython] GroundedJoint  # Assembly grounded joint (typed FeaturePython)
  ObjectToGround = -> Rail
FEATURE [App::Link] Block  label="Block001"
  LinkPlacement = pos=(0,35.2916,0) rot=(0,0,1;0rad)
  LinkedObject = -> Body001
  Placement = pos=(0,35.2916,0) rot=(0,0,1;0rad)
FEATURE [App::FeaturePython] Joint  label="BlockSlider"  # Assembly joint (typed FeaturePython)
  Activated = true
  AngleMax = 0
  AngleMin = 0
  Detach1 = false
  Detach2 = false
  Distance = 0
  Distance2 = 0
  EnableAngleMax = false
  EnableAngleMin = false
  EnableLengthMax = true
  EnableLengthMin = true
  JointType = 3 (Slider)
  LengthMax = 300
  LengthMin = -300
  Placement1 = pos=(-6,0,4) rot=(-0.57735,-0.57735,0.57735;4.18879rad)
  Placement2 = pos=(-6,0,4) rot=(-0.57735,-0.57735,0.57735;4.18879rad)
  Reference1 = -> Assembly [Rail.Edge1,Rail.Edge1]
  Reference2 = -> Assembly [Block.Edge49,Block.Edge49]
  expr: LengthMax = <<Rail Extrusion>>.Length / 2
  expr: LengthMin = -<<Rail Extrusion>>.Length / 2
FEATURE [App::Link] Foot  label="Foot001"
  LinkPlacement = pos=(-6.38e-14,-287.5,6.26e-14) rot=(0,0,1;0rad)
  LinkedObject = -> Body002
  Placement = pos=(-6.38e-14,-287.5,6.26e-14) rot=(0,0,1;0rad)
FEATURE [App::Link] Foot001  label="Foot002"
  LinkPlacement = pos=(0,287.5,-6.53e-14) rot=(0,0,1;3.14159rad)
  LinkedObject = -> Body002
  Placement = pos=(0,287.5,-6.53e-14) rot=(0,0,1;3.14159rad)
FEATURE [App::FeaturePython] Joint001  label="FootOneFixed"  # Assembly joint (typed FeaturePython)
  Activated = true
  AngleMax = 0
  AngleMin = 0
  Detach1 = false
  Detach2 = false
  Distance = 0
  Distance2 = 0
  EnableAngleMax = false
  EnableAngleMin = false
  EnableLengthMax = false
  EnableLengthMin = false
  JointType = 0 (Fixed)
  LengthMax = 0
  LengthMin = 0
  Placement1 = pos=(0,0,-4) rot=(0,0,1;0rad)
  Placement2 = pos=(-6.38e-14,-287.5,-4) rot=(1,0,0;3.14159rad)
  Reference1 = -> Assembly [Foot.Edge65,Foot.Edge65]
  Reference2 = -> Assembly [Rail.Edge91,Rail.Edge91]
FEATURE [App::FeaturePython] Joint002  label="FootTwoFixed"  # Assembly joint (typed FeaturePython)
  Activated = true
  AngleMax = 0
  AngleMin = 0
  Detach1 = false
  Detach2 = false
  Distance = 0
  Distance2 = 0
  EnableAngleMax = false
  EnableAngleMin = false
  EnableLengthMax = false
  EnableLengthMin = false
  JointType = 0 (Fixed)
  LengthMax = 0
  LengthMin = 0
  Offset2 = pos=(0,0,0) rot=(0,0,1;3.14159rad)
  Placement1 = pos=(0,0,-4) rot=(0,0,1;0rad)
  Placement2 = pos=(0,287.5,-4) rot=(0,-1,0;3.14159rad)
  Reference1 = -> Assembly [Foot001.Edge65,Foot001.Edge65]
  Reference2 = -> Assembly [Rail.Edge114,Rail.Edge114]
FEATURE [App::Link] Stand  label="Stand001"
  LinkPlacement = pos=(-4.44e-14,-112.5,2.44e-14) rot=(0,0,1;0rad)
  LinkedObject = -> Body006
  Placement = pos=(-4.44e-14,-112.5,2.44e-14) rot=(0,0,1;0rad)
FEATURE [App::FeaturePython] Joint003  label="StandFixed"  # Assembly joint (typed FeaturePython)
  Activated = true
  AngleMax = 0
  AngleMin = 0
  Detach1 = false
  Detach2 = false
  Distance = 0
  Distance2 = 0
  EnableAngleMax = false
  EnableAngleMin = false
  EnableLengthMax = false
  EnableLengthMin = false
  JointType = 0 (Fixed)
  LengthMax = 0
  LengthMin = 0
  Placement1 = pos=(-4.44e-14,-112.5,-4) rot=(1,0,0;3.14159rad)
  Placement2 = pos=(0,0,-4) rot=(1,0,0;3.14159rad)
  Reference1 = -> Assembly [Rail.Edge98,Rail.Edge98]
  Reference2 = -> Assembly [Stand.Edge8,Stand.Edge8]
FEATURE [App::Link] Servo  label="Servo001"
  LinkPlacement = pos=(-4.39e-14,-112.5,2.53e-14) rot=(0,0,1;0rad)
  LinkedObject = -> Body007
  Placement = pos=(-4.39e-14,-112.5,2.53e-14) rot=(0,0,1;0rad)
FEATURE [App::FeaturePython] Joint004  label="ServoFixed"  # Assembly joint (typed FeaturePython)
  Activated = true
  AngleMax = 0
  AngleMin = 0
  Detach1 = false
  Detach2 = false
  Distance = 0
  Distance2 = 0
  EnableAngleMax = false
  EnableAngleMin = false
  EnableLengthMax = false
  EnableLengthMin = false
  JointType = 0 (Fixed)
  LengthMax = 0
  LengthMin = 0
  Placement1 = pos=(111.117,-23.5,14.288) rot=(0,-1,0;0.207323rad)
  Placement2 = pos=(111.117,-23.5,14.288) rot=(0,-1,0;0.207323rad)
  Reference1 = -> Assembly [Servo.Edge43,Servo.Edge43]
  Reference2 = -> Assembly [Stand.Edge298,Stand.Edge298]
FEATURE [App::Link] ElectronicsLid  label="ElectronicsLid001"
  LinkPlacement = pos=(0.057735,-112.45,6.06e-14) rot=(0,0,1;0rad)
  LinkedObject = -> Body009
  Placement = pos=(0.057735,-112.45,6.06e-14) rot=(0,0,1;0rad)
FEATURE [App::FeaturePython] Joint005  label="RackSlider"  # Assembly joint (typed FeaturePython)
  Activated = true
  AngleMax = 0
  AngleMin = 0
  Detach1 = false
  Detach2 = false
  Distance = 0
  Distance2 = 0
  EnableAngleMax = false
  EnableAngleMin = false
  EnableLengthMax = true
  EnableLengthMin = false
  JointType = 3 (Slider)
  LengthMax = 0
  LengthMin = 0
  Offset1 = pos=(0,0.25,0) rot=(0,0,1;0rad)
  Placement1 = pos=(81.262,-28.05,2) rot=(-0.707107,0,0.707107;3.14159rad)
  Placement2 = pos=(81.3197,-28,2) rot=(-0.707107,0,0.707107;3.14159rad)
  Reference1 = -> Assembly [ElectronicsLid.Edge3,ElectronicsLid.Edge3]
  Reference2 = -> Assembly [Stand.Edge713,Stand.Edge713]
FEATURE [App::Link] Pinion  label="Pinion001"
  LinkPlacement = pos=(114.179,4.17808,24.0172) rot=(0.205841,0,-0.978585;1.5708rad)
  LinkedObject = -> Body005
  Placement = pos=(114.179,4.17808,24.0172) rot=(0.205841,0,-0.978585;1.5708rad)
FEATURE [App::FeaturePython] Joint006  label="PinionRevolute"  # Assembly joint (typed FeaturePython)
  Activated = true
  AngleMax = 90
  AngleMin = -90
  Detach1 = false
  Detach2 = false
  Distance = 0
  Distance2 = 0
  EnableAngleMax = true
  EnableAngleMin = true
  EnableLengthMax = false
  EnableLengthMin = false
  JointType = 1 (Revolute)
  LengthMax = 0
  LengthMin = 0
  Placement1 = pos=(112.51,-2.84e-14,31.9532) rot=(-0.103476,0,0.994632;3.14159rad)
  Placement2 = pos=(112.51,-1.42e-14,31.9532) rot=(-0.103476,0,0.994632;3.14159rad)
  Reference1 = -> Assembly [Pinion.Edge51,Pinion.Edge51]
  Reference2 = -> Assembly [Servo.Edge31,Servo.Edge31]
FEATURE [App::Link] Rack  label="Rack001"
  LinkPlacement = pos=(0,35.2916,-5.3e-15) rot=(0,0,1;0rad)
  LinkedObject = -> Body004
  Placement = pos=(0,35.2916,-5.3e-15) rot=(0,0,1;0rad)
FEATURE [App::FeaturePython] Joint007  label="RackBlockFixed"  # Assembly joint (typed FeaturePython)
  Activated = true
  AngleMax = 0
  AngleMin = 0
  Detach1 = false
  Detach2 = false
  Distance = 0
  Distance2 = 0
  EnableAngleMax = false
  EnableAngleMin = false
  EnableLengthMax = false
  EnableLengthMin = false
  JointType = 0 (Fixed)
  LengthMax = 0
  LengthMin = 0
  Placement1 = pos=(10,-10,9) rot=(1,0,0;3.14159rad)
  Placement2 = pos=(10,-10,9) rot=(0,0,1;0rad)
  Reference1 = -> Assembly [Rack.Edge11,Rack.Edge11]
  Reference2 = -> Assembly [Block.Edge41,Block.Edge41]
FEATURE [App::Link] PicoW  label="PicoW001"
  LinkPlacement = pos=(90,-112.5,-6) rot=(0,0,1;3.14159rad)
  LinkedObject = -> Body008
  Placement = pos=(90,-112.5,-6) rot=(0,0,1;3.14159rad)
FEATURE [App::FeaturePython] Joint008  label="PicoFixed"  # Assembly joint (typed FeaturePython)
  Activated = true
  AngleMax = 0
  AngleMin = 0
  Detach1 = false
  Detach2 = false
  Distance = 0
  Distance2 = 0
  EnableAngleMax = false
  EnableAngleMin = false
  EnableLengthMax = false
  EnableLengthMin = false
  JointType = 0 (Fixed)
  LengthMax = 0
  LengthMin = 0
  Offset2 = pos=(0,0,0) rot=(0,0,1;3.14159rad)
  Placement1 = pos=(5.7,23.5,0) rot=(0,0,1;0rad)
  Placement2 = pos=(84.3,-23.5,-6) rot=(0,0,1;3.14159rad)
  Reference1 = -> Assembly [PicoW.Edge14,PicoW.Edge14]
  Reference2 = -> Assembly [Stand.Edge836,Stand.Edge836]
FEATURE [App::Link] CountdownBracket  label="CountdownBracket001"
  LinkPlacement = pos=(-0.1,244.207,1e-15) rot=(0,0,1;0rad)
  LinkedObject = -> Body011
  Placement = pos=(-0.1,244.207,1e-15) rot=(0,0,1;0rad)
FEATURE [App::FeaturePython] Joint009  label="CountdownBracketSlider"  # Assembly joint (typed FeaturePython)
  Activated = true
  AngleMax = 0
  AngleMin = 0
  Detach1 = false
  Detach2 = false
  Distance = 0
  Distance2 = 0
  EnableAngleMax = false
  EnableAngleMin = false
  EnableLengthMax = true
  EnableLengthMin = true
  JointType = 3 (Slider)
  LengthMax = -46.24
  LengthMin = -85.45
  Offset1 = pos=(-0.65,0,0) rot=(0,0,1;0rad)
  Placement1 = pos=(6.1,7.5,-3.35) rot=(-0.57735,-0.57735,0.57735;4.18879rad)
  Placement2 = pos=(6,300,-3.35) rot=(-0.57735,-0.57735,0.57735;4.18879rad)
  Reference1 = -> Assembly [CountdownBracket.Edge24,CountdownBracket.Edge24]
  Reference2 = -> Assembly [Rail.Edge41,Rail.Vertex34]
  expr: .Offset1.Base.x = -<<Rail Cross-Section>>.Constraints.radius
FEATURE [App::Link] TramCarriage  label="TramCarriage001"
  LinkPlacement = pos=(0,35.2916,-1.8e-15) rot=(0,0,1;0rad)
  LinkedObject = -> Body003
  Placement = pos=(0,35.2916,-1.8e-15) rot=(0,0,1;0rad)
FEATURE [App::FeaturePython] Joint010  label="TramCarriageFixed"  # Assembly joint (typed FeaturePython)
  Activated = true
  AngleMax = 0
  AngleMin = 0
  Detach1 = false
  Detach2 = false
  Distance = 0
  Distance2 = 0
  EnableAngleMax = false
  EnableAngleMin = false
  EnableLengthMax = false
  EnableLengthMin = false
  JointType = 0 (Fixed)
  LengthMax = 0
  LengthMin = 0
  Placement1 = pos=(-10,-10,9) rot=(1,0,0;3.14159rad)
  Placement2 = pos=(-10,-10,9) rot=(0,0,1;0rad)
  Reference1 = -> Assembly [TramCarriage.Edge7,TramCarriage.Edge7]
  Reference2 = -> Assembly [Block.Edge40,Block.Edge40]
FEATURE [Sketcher::SketchObject] Sketch066
  ArcFitTolerance = 1e-06
  FullyConstrained = false
  MakeInternals = false
  sketch-geometry (78):
    g0: BSplineCurve PolesCount=4 KnotsCount=2 Degree=3 IsPeriodic=0
    g1: BSplineCurve PolesCount=4 KnotsCount=2 Degree=3 IsPeriodic=0
    g2: BSplineCurve PolesCount=4 KnotsCount=2 Degree=3 IsPeriodic=0
    g3: BSplineCurve PolesCount=2 KnotsCount=2 Degree=1 IsPeriodic=0
    g4: BSplineCurve PolesCount=2 KnotsCount=2 Degree=1 IsPeriodic=0
    g5: BSplineCurve PolesCount=2 KnotsCount=2 Degree=1 IsPeriodic=0
    g6: BSplineCurve PolesCount=2 KnotsCount=2 Degree=1 IsPeriodic=0
    g7: BSplineCurve PolesCount=2 KnotsCount=2 Degree=1 IsPeriodic=0
    g8: BSplineCurve PolesCount=4 KnotsCount=2 Degree=3 IsPeriodic=0
    g9: BSplineCurve PolesCount=4 KnotsCount=2 Degree=3 IsPeriodic=0
    g10: BSplineCurve PolesCount=2 KnotsCount=2 Degree=1 IsPeriodic=0
    g11: BSplineCurve PolesCount=4 KnotsCount=2 Degree=3 IsPeriodic=0
    g12: BSplineCurve PolesCount=4 KnotsCount=2 Degree=3 IsPeriodic=0
    g13: BSplineCurve PolesCount=2 KnotsCount=2 Degree=1 IsPeriodic=0
    g14: BSplineCurve PolesCount=2 KnotsCount=2 Degree=1 IsPeriodic=0
    g15: BSplineCurve PolesCount=4 KnotsCount=2 Degree=3 IsPeriodic=0
    g16: BSplineCurve PolesCount=4 KnotsCount=2 Degree=3 IsPeriodic=0
    g17: BSplineCurve PolesCount=2 KnotsCount=2 Degree=1 IsPeriodic=0
    g18: BSplineCurve PolesCount=4 KnotsCount=2 Degree=3 IsPeriodic=0
    g19: BSplineCurve PolesCount=4 KnotsCount=2 Degree=3 IsPeriodic=0
    g20: BSplineCurve PolesCount=2 KnotsCount=2 Degree=1 IsPeriodic=0
    g21: BSplineCurve PolesCount=2 KnotsCount=2 Degree=1 IsPeriodic=0
    g22: BSplineCurve PolesCount=2 KnotsCount=2 Degree=1 IsPeriodic=0
    g23: BSplineCurve PolesCount=2 KnotsCount=2 Degree=1 IsPeriodic=0
    g24: BSplineCurve PolesCount=2 KnotsCount=2 Degree=1 IsPeriodic=0
    g25: BSplineCurve PolesCount=2 KnotsCount=2 Degree=1 IsPeriodic=0
    g26: BSplineCurve PolesCount=2 KnotsCount=2 Degree=1 IsPeriodic=0
    g27: BSplineCurve PolesCount=2 KnotsCount=2 Degree=1 IsPeriodic=0
    g28: BSplineCurve PolesCount=2 KnotsCount=2 Degree=1 IsPeriodic=0
    g29: BSplineCurve PolesCount=4 KnotsCount=2 Degree=3 IsPeriodic=0
    g30: BSplineCurve PolesCount=4 KnotsCount=2 Degree=3 IsPeriodic=0
    g31: BSplineCurve PolesCount=2 KnotsCount=2 Degree=1 IsPeriodic=0
    g32: BSplineCurve PolesCount=4 KnotsCount=2 Degree=3 IsPeriodic=0
    g33: BSplineCurve PolesCount=4 KnotsCount=2 Degree=3 IsPeriodic=0
    g34: BSplineCurve PolesCount=2 KnotsCount=2 Degree=1 IsPeriodic=0
    g35: BSplineCurve PolesCount=2 KnotsCount=2 Degree=1 IsPeriodic=0
    g36: BSplineCurve PolesCount=4 KnotsCount=2 Degree=3 IsPeriodic=0
    g37: BSplineCurve PolesCount=4 KnotsCount=2 Degree=3 IsPeriodic=0
    g38: BSplineCurve PolesCount=2 KnotsCount=2 Degree=1 IsPeriodic=0
    g39: BSplineCurve PolesCount=4 KnotsCount=2 Degree=3 IsPeriodic=0
    g40: BSplineCurve PolesCount=4 KnotsCount=2 Degree=3 IsPeriodic=0
    g41: BSplineCurve PolesCount=2 KnotsCount=2 Degree=1 IsPeriodic=0
    g42: BSplineCurve PolesCount=2 KnotsCount=2 Degree=1 IsPeriodic=0
    g43: BSplineCurve PolesCount=2 KnotsCount=2 Degree=1 IsPeriodic=0
    g44: BSplineCurve PolesCount=2 KnotsCount=2 Degree=1 IsPeriodic=0
    g45: BSplineCurve PolesCount=2 KnotsCount=2 Degree=1 IsPeriodic=0
    g46: BSplineCurve PolesCount=4 KnotsCount=2 Degree=3 IsPeriodic=0
    g47: BSplineCurve PolesCount=4 KnotsCount=2 Degree=3 IsPeriodic=0
    g48: BSplineCurve PolesCount=4 KnotsCount=2 Degree=3 IsPeriodic=0
    g49: BSplineCurve PolesCount=4 KnotsCount=2 Degree=3 IsPeriodic=0
    g50: BSplineCurve PolesCount=4 KnotsCount=2 Degree=3 IsPeriodic=0
    g51: BSplineCurve PolesCount=2 KnotsCount=2 Degree=1 IsPeriodic=0
    g52: BSplineCurve PolesCount=4 KnotsCount=2 Degree=3 IsPeriodic=0
    g53: BSplineCurve PolesCount=2 KnotsCount=2 Degree=1 IsPeriodic=0
    g54: BSplineCurve PolesCount=4 KnotsCount=2 Degree=3 IsPeriodic=0
    g55: BSplineCurve PolesCount=2 KnotsCount=2 Degree=1 IsPeriodic=0
    g56: BSplineCurve PolesCount=2 KnotsCount=2 Degree=1 IsPeriodic=0
    g57: BSplineCurve PolesCount=2 KnotsCount=2 Degree=1 IsPeriodic=0
    g58: BSplineCurve PolesCount=2 KnotsCount=2 Degree=1 IsPeriodic=0
    g59: BSplineCurve PolesCount=2 KnotsCount=2 Degree=1 IsPeriodic=0
    g60: BSplineCurve PolesCount=2 KnotsCount=2 Degree=1 IsPeriodic=0
    g61: BSplineCurve PolesCount=2 KnotsCount=2 Degree=1 IsPeriodic=0
    g62: BSplineCurve PolesCount=2 KnotsCount=2 Degree=1 IsPeriodic=0
    g63: BSplineCurve PolesCount=2 KnotsCount=2 Degree=1 IsPeriodic=0
    g64: BSplineCurve PolesCount=4 KnotsCount=2 Degree=3 IsPeriodic=0
    g65: BSplineCurve PolesCount=2 KnotsCount=2 Degree=1 IsPeriodic=0
    g66: BSplineCurve PolesCount=4 KnotsCount=2 Degree=3 IsPeriodic=0
    g67: BSplineCurve PolesCount=2 KnotsCount=2 Degree=1 IsPeriodic=0
    g68: BSplineCurve PolesCount=4 KnotsCount=2 Degree=3 IsPeriodic=0
    g69: BSplineCurve PolesCount=4 KnotsCount=2 Degree=3 IsPeriodic=0
    g70: BSplineCurve [constr] PolesCount=2 KnotsCount=2 Degree=1 IsPeriodic=0
    g71: BSplineCurve [constr] PolesCount=2 KnotsCount=2 Degree=1 IsPeriodic=0
    g72: BSplineCurve [constr] PolesCount=2 KnotsCount=2 Degree=1 IsPeriodic=0
    g73: BSplineCurve [constr] PolesCount=2 KnotsCount=2 Degree=1 IsPeriodic=0
    g74: Circle CenterX=44.7617 CenterY=-141.918 CenterZ=0 NormalX=0 NormalY=0 NormalZ=1 AngleXU=0 Radius=1.75
    g75: Circle CenterX=86.1598 CenterY=-141.918 CenterZ=0 NormalX=0 NormalY=0 NormalZ=1 AngleXU=0 Radius=1.75
    g76: Circle CenterX=157.367 CenterY=-141.918 CenterZ=0 NormalX=0 NormalY=0 NormalZ=1 AngleXU=0 Radius=1.75
    g77: Circle CenterX=198.797 CenterY=-141.918 CenterZ=0 NormalX=0 NormalY=0 NormalZ=1 AngleXU=0 Radius=1.75
  constraints (78):
    c: Coincident(g0,g1)
    c: Coincident(g1,g2)
    c: Coincident(g2,g3)
    c: Coincident(g3,g4)
    c: Coincident(g4,g5)
    c: Coincident(g5,g6)
    c: Coincident(g6,g7)
    c: Coincident(g7,g8)
    c: Coincident(g8,g9)
    c: Coincident(g9,g10)
    c: Coincident(g10,g11)
    c: Coincident(g11,g12)
    c: Coincident(g12,g13)
    c: Coincident(g13,g14)
    c: Coincident(g14,g15)
    c: Coincident(g15,g16)
    c: Coincident(g16,g17)
    c: Coincident(g17,g18)
    c: Coincident(g18,g19)
    c: Coincident(g19,g20)
    c: Coincident(g20,g21)
    c: Coincident(g21,g22)
    c: Coincident(g22,g23)
    c: Coincident(g23,g24)
    c: Coincident(g24,g25)
    c: Coincident(g25,g26)
    c: Coincident(g26,g27)
    c: Coincident(g27,g28)
    c: Coincident(g28,g29)
    c: Coincident(g29,g30)
    c: Coincident(g30,g31)
    c: Coincident(g31,g32)
    c: Coincident(g32,g33)
    c: Coincident(g33,g34)
    c: Coincident(g34,g35)
    c: Coincident(g35,g36)
    c: Coincident(g36,g37)
    c: Coincident(g37,g38)
    c: Coincident(g38,g39)
    c: Coincident(g39,g40)
    c: Coincident(g40,g41)
    c: Coincident(g41,g42)
    c: Coincident(g42,g43)
    c: Coincident(g43,g44)
    c: Coincident(g44,g45)
    c: Coincident(g45,g46)
    c: Coincident(g46,g47)
    c: Coincident(g47,g48)
    c: Coincident(g48,g49)
    c: Coincident(g49,g50)
    c: Coincident(g50,g51)
    c: Coincident(g51,g52)
    c: Coincident(g52,g53)
    c: Coincident(g53,g54)
    c: Coincident(g54,g55)
    c: Coincident(g55,g56)
    c: Coincident(g56,g57)
    c: Coincident(g57,g58)
    c: Coincident(g58,g59)
    c: Coincident(g59,g60)
    c: Coincident(g60,g61)
    c: Coincident(g61,g62)
    c: Coincident(g62,g63)
    c: Coincident(g63,g64)
    c: Coincident(g64,g65)
    c: Coincident(g65,g66)
    c: Coincident(g66,g67)
    c: Coincident(g67,g68)
    c: Coincident(g68,g69)
    c: Coincident(g69,g0)
    c: Coincident(g74,g70)
    c: PointOnObject(g70,g74)
    c: Coincident(g75,g71)
    c: PointOnObject(g71,g75)
    c: Coincident(g76,g72)
    c: PointOnObject(g72,g76)
    c: Coincident(g77,g73)
    c: PointOnObject(g73,g77)
FEATURE [PartDesign::Pad] Pad025
  Direction = (0,0,1)
  Length = 5
  Length2 = 10
  Profile = -> Sketch066
  ReferenceAxis = -> Sketch066 [N_Axis]
  Refine = true
  Suppressed = false
  Type = 0
FEATURE [PartDesign::Body] Body012  label="TramPlaceholder"
  AllowCompound = false
  Group = -> [Sketch066,Pad025]
  Origin = -> Origin014
  Tip = -> Pad025
FEATURE [App::Link] TramPlaceholder  label="TramPlaceholder001"
  LinkPlacement = pos=(-21.5,-86.5539,143.068) rot=(0.57735,0.57735,0.57735;2.0944rad)
  LinkedObject = -> Body012
  Placement = pos=(-21.5,-86.5539,143.068) rot=(0.57735,0.57735,0.57735;2.0944rad)
FEATURE [App::FeaturePython] Joint011  label="TramPlaceholderFixed"  # Assembly joint (typed FeaturePython)
  Activated = true
  AngleMax = 0
  AngleMin = 0
  Detach1 = false
  Detach2 = false
  Distance = 0
  Distance2 = 0
  EnableAngleMax = false
  EnableAngleMin = false
  EnableLengthMax = false
  EnableLengthMin = false
  JointType = 0 (Fixed)
  LengthMax = 0
  LengthMin = 0
  Offset2 = pos=(0,0,0) rot=(0,0,1;3.14159rad)
  Placement1 = pos=(198.797,-141.918,5) rot=(0,0,1;0rad)
  Placement2 = pos=(-16.5,76.9519,1.15) rot=(-0.57735,-0.57735,0.57735;2.0944rad)
  Reference1 = -> Assembly [TramPlaceholder.Edge213,TramPlaceholder.Edge213]
  Reference2 = -> Assembly [TramCarriage.Edge76,TramCarriage.Edge76]
FEATURE [Sketcher::SketchObject] Sketch067
  ArcFitTolerance = 1e-06
  AttachmentSupport = -> [XY_Plane015]
  FullyConstrained = true
  MakeInternals = false
  MapMode = 5
  sketch-geometry (15):
    g0: LineSegment StartX=-290 StartY=-10 StartZ=0 EndX=290 EndY=-10 EndZ=0
    g1: LineSegment StartX=290 StartY=-10 StartZ=0 EndX=290 EndY=10 EndZ=0
    g2: LineSegment StartX=290 StartY=10 StartZ=0 EndX=-290 EndY=10 EndZ=0
    g3: LineSegment StartX=-290 StartY=10 StartZ=0 EndX=-290 EndY=-10 EndZ=0
    g4: GeomPoint [constr] X=0 Y=0 Z=0
    g5: LineSegment [constr] StartX=-290 StartY=-10 StartZ=0 EndX=-285 EndY=-10 EndZ=0
    g6: LineSegment [constr] StartX=-285 StartY=-10 StartZ=0 EndX=-285 EndY=-5 EndZ=0
    g7: LineSegment [constr] StartX=-285 StartY=-5 StartZ=0 EndX=-290 EndY=-5 EndZ=0
    g8: LineSegment [constr] StartX=-290 StartY=-5 StartZ=0 EndX=-290 EndY=-10 EndZ=0
    g9: LineSegment [constr] StartX=290 StartY=-10 StartZ=0 EndX=290 EndY=-5 EndZ=0
    g10: LineSegment [constr] StartX=290 StartY=-5 StartZ=0 EndX=285 EndY=-5 EndZ=0
    g11: LineSegment [constr] StartX=285 StartY=-5 StartZ=0 EndX=285 EndY=-10 EndZ=0
    g12: LineSegment [constr] StartX=285 StartY=-10 StartZ=0 EndX=290 EndY=-10 EndZ=0
    g13: Circle CenterX=-285 CenterY=-5 CenterZ=0 NormalX=0 NormalY=0 NormalZ=1 AngleXU=0 Radius=1.75
    g14: Circle CenterX=285 CenterY=-5 CenterZ=0 NormalX=0 NormalY=0 NormalZ=1 AngleXU=0 Radius=1.75
  constraints (38):
    c: Coincident(g0,g1)
    c: Coincident(g1,g2)
    c: Coincident(g2,g3)
    c: Coincident(g3,g0)
    c: Horizontal(g0)
    c: Horizontal(g2)
    c: Vertical(g1)
    c: Vertical(g3)
    c: Symmetric(g2,g0,g4)
    c: Distance(g1,g3) = 580
    c: Distance(g0,g2) = 20
    c: Coincident(g4,g-1)
    c: Coincident(g5,g6)
    c: Coincident(g6,g7)
    c: Coincident(g7,g8)
    c: Coincident(g8,g5)
    c: Horizontal(g5)
    c: Horizontal(g7)
    c: Vertical(g6)
    c: Vertical(g8)
    c: Distance(g6,g8) = 5
    c: Distance(g5,g7) = 5
    c: Coincident(g5,g0)
    c: Coincident(g9,g10)
    c: Coincident(g10,g11)
    c: Coincident(g11,g12)
    c: Coincident(g12,g9)
    c: Vertical(g9)
    c: Vertical(g11)
    c: Horizontal(g10)
    c: Horizontal(g12)
    c: Distance(g9,g11) = 5
    c: Distance(g10,g12) = 5
    c: Coincident(g9,g0)
    c: Diameter(g13) = 3.5
    c: Coincident(g13,g6)
    c: Diameter(g14) = 3.5
    c: Coincident(g14,g10)
FEATURE [PartDesign::Pad] Pad026
  Direction = (0,0,1)
  Length = 5
  Length2 = 10
  Profile = -> Sketch067
  ReferenceAxis = -> Sketch067 [N_Axis]
  Refine = true
  Suppressed = false
  Type = 0
FEATURE [PartDesign::Body] Body013  label="CountdownPlaceholder"
  AllowCompound = false
  Group = -> [Sketch067,Pad026]
  Origin = -> Origin015
  Tip = -> Pad026
FEATURE [App::Link] CountdownPlaceholder  label="CountdownPlaceholder001"
  LinkPlacement = pos=(-34.6,26.8732,2.94616) rot=(0.57735,0.57735,0.57735;2.0944rad)
  LinkedObject = -> Body013
  Placement = pos=(-34.6,26.8732,2.94616) rot=(0.57735,0.57735,0.57735;2.0944rad)
FEATURE [App::Link] CountdownBracketOtherEnd  label="CountdownBracketOtherEnd001"
  LinkPlacement = pos=(-0.1,-190.46,-1.98e-13) rot=(0,0,1;0rad)
  LinkedObject = -> Clone001
  Placement = pos=(-0.1,-190.46,-1.98e-13) rot=(0,0,1;0rad)
FEATURE [App::FeaturePython] Joint012  label="CountdownBracketFixed"  # Assembly joint (typed FeaturePython)
  Activated = true
  AngleMax = 0
  AngleMin = 0
  Detach1 = false
  Detach2 = false
  Distance = 0
  Distance2 = 0
  EnableAngleMax = false
  EnableAngleMin = false
  EnableLengthMax = false
  EnableLengthMin = false
  JointType = 0 (Fixed)
  LengthMax = 0
  LengthMin = 0
  Offset2 = pos=(0,0,0) rot=(0,0,1;3.14159rad)
  Placement1 = pos=(285,-5,5) rot=(0,0,1;0rad)
  Placement2 = pos=(-29.5,67.6664,-2.05384) rot=(-0.57735,-0.57735,0.57735;2.0944rad)
  Reference1 = -> Assembly [CountdownPlaceholder.Edge15,CountdownPlaceholder.Edge15]
  Reference2 = -> Assembly [CountdownBracket.Edge129,CountdownBracket.Edge129]
FEATURE [App::FeaturePython] Joint013  label="CountdownOtherBracketFixed"  # Assembly joint (typed FeaturePython)
  Activated = true
  AngleMax = 0
  AngleMin = 0
  Detach1 = false
  Detach2 = false
  Distance = 0
  Distance2 = 0
  EnableAngleMax = false
  EnableAngleMin = false
  EnableLengthMax = false
  EnableLengthMin = false
  JointType = 0 (Fixed)
  LengthMax = 0
  LengthMin = 0
  Placement1 = pos=(-285,-5,5) rot=(0,0,1;0rad)
  Placement2 = pos=(-29.5,-67.6664,-2.05384) rot=(0.57735,0.57735,0.57735;2.0944rad)
  Reference1 = -> Assembly [CountdownPlaceholder.Edge18,CountdownPlaceholder.Edge18]
  Reference2 = -> Assembly [CountdownBracketOtherEnd.Edge129,CountdownBracketOtherEnd.Edge129]
FEATURE [Assembly::JointGroup] Joints
  Group = -> [GroundedJoint,Joint,Joint001,Joint002,Joint003,Joint004,Joint005,Joint006,Joint007,Joint008,Joint009,Joint010,Joint011,Joint012,Joint013]
FEATURE [Assembly::AssemblyObject] Assembly
  Group = -> [Joints,Rail,GroundedJoint,Block,Joint,Foot,Foot001,Joint001,Joint002,Stand,Joint003,Servo,Joint004,ElectronicsLid,Joint005,Pinion,Joint006,Rack,Joint007,PicoW,Joint008,CountdownBracket,Joint009,TramCarriage,Joint010,TramPlaceholder,Joint011,CountdownPlaceholder,CountdownBracketOtherEnd,Joint012,Joint013]
  Origin = -> Origin013
  Type = Assembly
